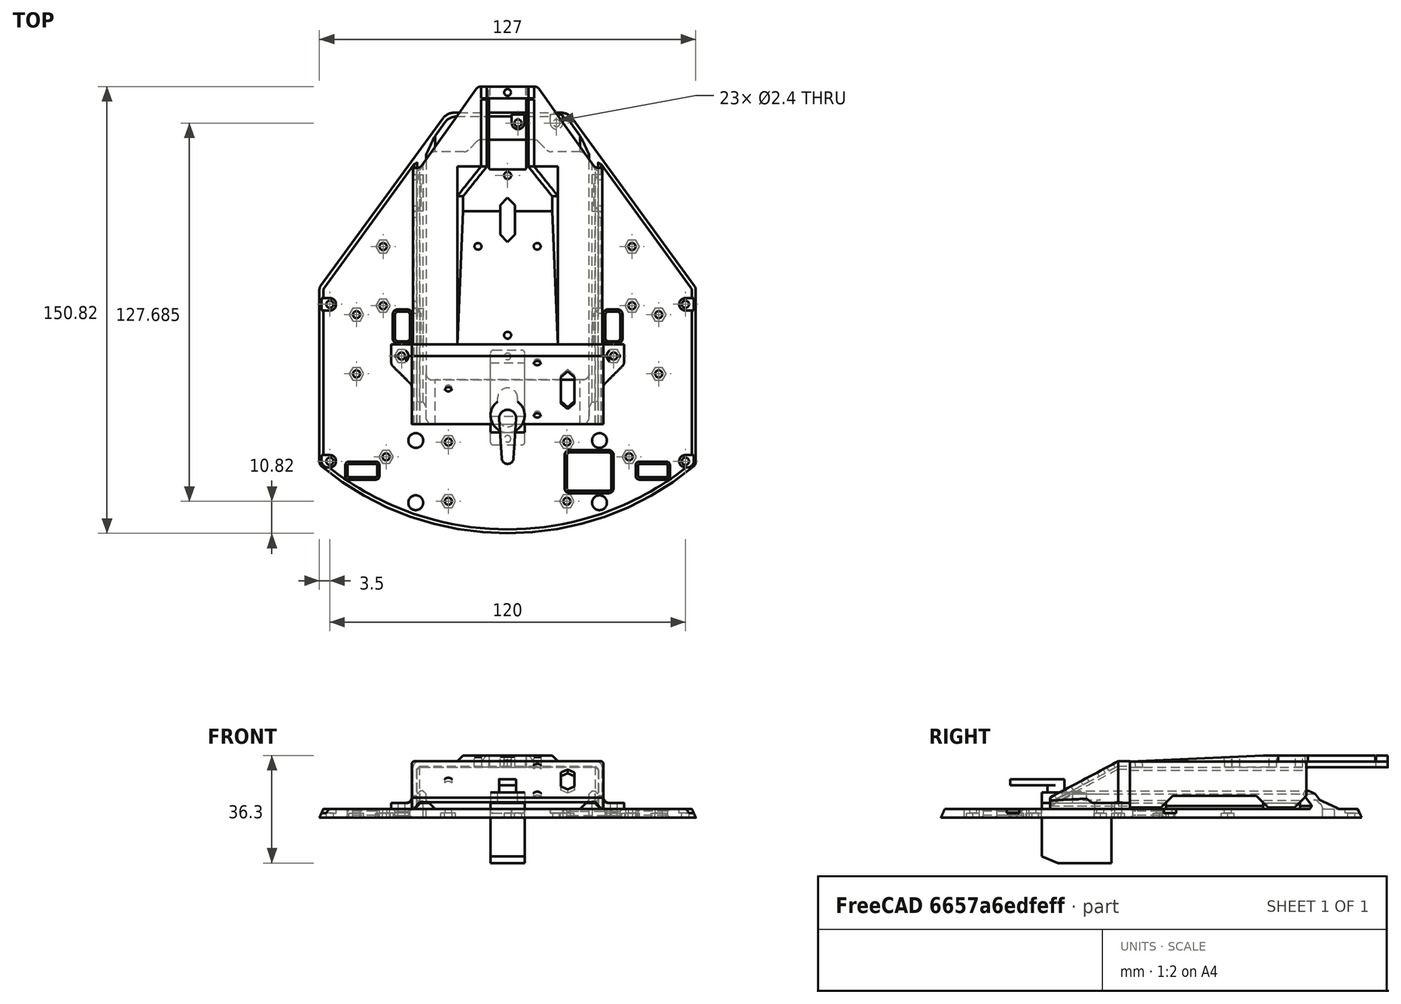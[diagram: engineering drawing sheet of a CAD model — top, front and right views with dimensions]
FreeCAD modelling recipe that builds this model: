
FCSTD DOCUMENT  (FreeCAD 0.19R24276 (Git))
Label: PB3D_TriPlate_Top
License: All rights reserved
LicenseURL: http://en.wikipedia.org/wiki/All_rights_reserved
objects: Sketcher::SketchObject×49, PartDesign::Pocket×31, PartDesign::Plane×10, PartDesign::Pad×9, PartDesign::Body×6, PartDesign::AdditiveLoft×2, PartDesign::SubtractiveLoft×2, App::Part×2, Spreadsheet::Sheet×1, PartDesign::Fillet×1, PartDesign::Chamfer×1, Mesh::Feature×1
note: 157 computed .brp shape members not serialized (recipe doc carries the construction recipe); baked Part::Feature solids carry a one-line shape summary decoded from their .brp

FEATURE [Spreadsheet::Sheet] Spreadsheet  label="params"
  cells = A2=Bottom Plate Main Params; C2=Shell Main Params; E2=Shell Top Bracket Params; G2=Sensor Mounts; A3=Plate Length; B3(plate_length)==170mm; C3=Shell Height; D3(shell_totheight)==42mm; E3=Top Brack Width; F3(shell_topbrack_width)==7mm; G3=Touch Sens Offset; H3(sens_touch_offset_leng)==25mm; I3=Gr Mt 1 W Offset; J3(grmt1_w_offset)==32mm; K3=Gr Mt CableSlot W Offset; L3(grmt_cable_slot_w_offset)==33mm; A4=Plate Width; B4(plate_width)==155mm; C4=Shell Vert Height; D4(shell_vertheight)==10mm; E4=Top Brack Front Split; F4(shell_topbrack_frontsplit)==50mm; G4=Ear Mt Hole Spacing; H4(ear_mt_hole_spacing)==82mm; I4=Gr Mt 1 L Offset; J4(grmt1_l_offset)==31mm; K4=Gr Mt CableSlot L Offset; L4(grmt_cable_slot_l_offset)==19mm; A5=Front Diameter; B5(front_diameter)==225mm; C5=Shell Overhang Length; D5(shell_overhang_leng)==14mm; E5=Top Brack Hole Offset; F5(shell_topbrack_hole_offset)==3.5mm; G5=Ear Mt Hole Loc; H5(ear_mt_holes_loc)==20mm; I5=Gr Mt 2 W Offset; J5(grmt2_w_offset)==41mm; A6=Tail Width; B6(tail_width)==50mm; C6=Shell Wall Thickness; D6(shell_wall_thick)==2mm; E6=Top Brack Fr Leng; F6(top_brack_front_leng)==10mm; G6=Ear Cable Slot Offset From Mt; H6(ear_cable_slot_offset)==2.4mm; I6=Gr Mt 2 L Offset; J6(grmt2_l_offset)==8mm; A7=Plate Thickness; B7(plate_thick)==3mm; C7=Shell Wall Slope; D7(shell_wall_slope)==(shell_totheight - shell_vertheight) / shell_overhang_leng; G7=Ear Cable Slot WidthSpace; H7(ear_cable_slot_offset_width)==8mm; C8=TopPlate Dims; E8=Rails - Shield Cover; G8=Front Cover; I8=Shield Cover; A9=Front Vert. Edge; B9(front_vert_edge)==2mm; C9=Top Thickness; D9(top_thickness)==3mm; E9=Rail Width; F9(rail_width)==3mm; G9=FrCov Leng; H9(coverfront_leng)==27mm; I9=ShCov Leng Side; J9(shieldcov_leng_side)==59.5mm; A10=Back Vert. Edge; B10(back_vert_edge)==15mm; C10=Top Chamfer Width; D10(top_chamfer_width)==top_thickness / shell_wall_slope; E10=Rail Height; F10(rail_height)==6mm; G10=FrCov Height (underneath); H10(coverfront_under_height)==coverfront_angle_leng * tan(rail_front_angle) + rail_front_vert_height + coverfront_tol; I10=SheCov Leng Tot W Tail; J10(shieldcov_leng_tot_wtail)==87mm; A11=Std. Chamfer; B11(std_chamf)==1mm; E11=Rail Front Angle; F11(rail_front_angle)=28; G11=FrCov Wall Thick; H11(coverfront_wall_thick)==1.6mm; I11=ShCov Height; J11(shieldcov_height)==12mm; A12=Std. Radius; B12(std_rad)==2mm; C12=Arduino CutOut; E12=Rail Front Offset Leng; F12(rail_front_offset_leng)==9mm; G12=FrCov Angle Leng; H12(coverfront_angle_leng)==23mm; I12=ShCov Width Inner; J12(shieldcov_width_inner)==ardcut_width + 2 * (rail_width + shieldcov_tol); A13=Wheel Well Radius; B13(wheel_well_rad)==7mm; C13=ArdCut Width; D13(ardcut_width)==55mm; E13=Rail Front Vert Height; F13(rail_front_vert_height)==2mm; G13=FrCov Std Rad; H13(coverfront_std_rad)==coverfront_wall_thick / 2; I13=ShCov Thick Top; J13(shieldcov_thick_top)==2mm; A14=Tail Radius; B14(tail_rad)==5mm; C14=ArdCut Length; D14(ardcut_length)==77mm; E14=Rail Clip Mt Width; F14(rail_clip_mt_width)==2mm; G14=FrCov Tol; H14(coverfront_tol)==0.2mm; I14=ShCov Thick Side; J14(shieldcov_thick_side)==1.2mm; C15=ArdCut Offset LEng; D15(ardcut_offset_leng)==6mm; E15=Rail Clip Mt Loc Front Y; F15(rail_clip_mt_loc_front)==rail_clip_mt_offset + shieldcov_clip_leng / 2; G15=FrCov Foot Width; H15(coverfront_foot_width)==7mm; I15=ShCov Tol; J15(shieldcov_tol)==0.2mm; A16=Wheel Well Plate Width; B16(wheel_well_plate_width)==115mm; C16=ArdCut Rear Angle Leng; D16(ardcut_rear_angle_leng)==3mm; E16=Rail Clip Mt Tol; F16(rail_clip_mt_tol)==0.3mm; G16=FrCov Foot Height; H16(coverfront_foot_height)==2mm; I16=ShCov Clip Hook Width; J16(shieldcov_clip_hook_width)==1.6mm; A17=Wheel Well Clearance; B17(wheel_well_clearance)==48mm; C17=ArdCut Cable Slot Width; D17(ardcut_cableslot_width)==18mm; E17=Rail Clip Mt Loc Back; F17(rail_clip_mt_loc_back)==rail_clip_mt_offset + shieldcov_leng_side - (shieldcov_clip_cut_height - shieldcov_clip_hook_width) - shieldcov_clip_leng / 2; G17=FrCov Foot Leng; H17(coverfront_foot_leng)==6mm; A18=Wheel Well Vert; B18(wheel_well_vert)==7mm; C18=ArdCut Cable Slot Leng; D18(ardcut_cableslot_leng)==4mm; E18=Rail Clip Mt Offset; F18(rail_clip_mt_offset)==18mm; G18=FrCov Outer Wall Width; H18(coverfront_outer_wall_width)==ardcut_width + 2 * (rail_width + coverfront_tol + coverfront_wall_thick); I18=ShCov PreSen AngLeng; J18(shieldcov_pressens_angle_leng)==45mm; E19=Rail Clip Mt Height; F19(rail_clip_mt_height)==2.75mm; G19=FrCov Outer Foot Width; H19(coverfront_outer_foot_width)==coverfront_outer_wall_width + 2 * coverfront_foot_width; I19=ShCov PresSens Height; J19(shieldcov_pressens_height)==2mm; A20=M2 Bolt Clearances; C20=M2.5 Bolt Clearances; I20=ShCov PresSens Width; J20(shieldcov_pressens_width)==30mm; A21=Hole Clear Diam; B21(m2_hole_clear_diam)==2.4mm; C21=Hole Clear Diam; D21(m25_hole_clear_diam)==2.8mm; G21=FrCov W Hole Offset; H21(coverfront_hole_offset_width)==coverfront_foot_width / 2; I21=ShCov PresSens Angle; J21(shieldcov_pressens_angle)==asin(shieldcov_pressens_height / shieldcov_pressens_angle_leng); A22=Head Clear Diam; B22(m2_head_clear_diam)==4.2mm; C22=Head Clear Diam; D22(m25_head_clear_diam)==5.3mm; G22=FrCov L Hole Offset; H22(coverfront_hole_offset_leng)==coverfront_foot_leng / 2 + 1mm; I22=ShCov PresSens Hole Offset; J22(shieldcov_pressens_hole_offset)==3mm; A23=Head Min Depth; B23(m2_head_min_depth)==1.6mm; C23=Head Min Depth; D23(m25_head_min_depth)==2.3mm; I23=ShCov PresSens Grove Cable Slot Offset; J23(shieldcov_pressens_grovecableslot_offset)==42mm; A24=Nut Clear Flat; B24(m2_nut_clear_flat)==4.3mm; C24=Nut Clear Flat; D24(m25_nut_clear_flat)==5.2mm; G24=FrCov Speaker Mt Offset; H24(frontcover_speaker_mt_offset)==3mm; A25=Nut Min Depth; B25(m2_nut_min_depth)==1.75mm; C25=Nut Min Depth; D25(m25_nut_min_depth)==2mm; I25=ShCov Servo Tail Width; J25(shieldcov_servotail_width)==18mm; G26=PlateToFrCov Offset Y; H26(plate_to_frontcov_offset_y)==9mm; I26=ShCov Servo Mt Slot Offset; J26(shieldcov_servomt_slot_offset)==57mm; A27=Std Small Chamf; +17 more cells
FEATURE [Sketcher::SketchObject] Sketch014  label="Sketch_OuterShell_Template"
  FullyConstrained = true
  MapMode = 5
  Support = -> [XY_Plane001]
  expr: Constraints[23] = <<params>>.std_rad
  expr: Constraints[61] = <<params>>.wheel_well_clearance
  expr: Constraints[30] = <<params>>.back_vert_edge
  expr: Constraints[31] = <<params>>.std_rad
  expr: Constraints[12] = <<params>>.plate_length
  expr: Constraints[29] = <<params>>.front_vert_edge
  expr: Constraints[32] = <<params>>.front_diameter
  expr: Constraints[13] = <<params>>.tail_rad
  expr: Constraints[14] = <<params>>.tail_width
  expr: Constraints[41] = <<params>>.plate_width
  expr: Constraints[59] = <<params>>.std_rad
  sketch-geometry (24):
    g0: ArcOfCircle CenterX=0 CenterY=52.6846 CenterZ=0 NormalX=0 NormalY=0 NormalZ=1 AngleXU=0 Radius=112.5 StartAngle=3.96017 EndAngle=5.4646
    g1: LineSegment StartX=-77.1162 StartY=42.1781 StartZ=0 EndX=-29.0404 EndY=108.13 EndZ=0
    g2: LineSegment StartX=-25 StartY=110.185 StartZ=0 EndX=25 EndY=110.185 EndZ=0
    g3: LineSegment StartX=29.0404 StartY=108.13 StartZ=0 EndX=77.1162 EndY=42.1781 EndZ=0
    g4: LineSegment StartX=0 StartY=0 StartZ=0 EndX=0 EndY=110.185 EndZ=0
    g5: ArcOfCircle CenterX=-25 CenterY=105.185 CenterZ=0 NormalX=0 NormalY=0 NormalZ=1 AngleXU=0 Radius=5 StartAngle=1.5708 EndAngle=2.5117
    g6: ArcOfCircle CenterX=25 CenterY=105.185 CenterZ=0 NormalX=0 NormalY=0 NormalZ=1 AngleXU=0 Radius=5 StartAngle=0.629895 EndAngle=1.5708
    g7: GeomPoint X=0 Y=-59.8154 Z=0
    g8: LineSegment StartX=77.5 StartY=26 StartZ=0 EndX=77.5 EndY=41 EndZ=0
    g9: LineSegment StartX=77.5 StartY=-26 StartZ=0 EndX=77.5 EndY=-28 EndZ=0
    g10: LineSegment StartX=-77.5 StartY=26 StartZ=0 EndX=-77.5 EndY=41 EndZ=0
    g11: ArcOfCircle CenterX=75.5 CenterY=-28 CenterZ=0 NormalX=0 NormalY=0 NormalZ=1 AngleXU=0 Radius=2 StartAngle=5.4646 EndAngle=6.28319
    g12: ArcOfCircle CenterX=-75.5 CenterY=-28 CenterZ=0 NormalX=0 NormalY=0 NormalZ=1 AngleXU=0 Radius=2 StartAngle=3.14159 EndAngle=3.96017
    g13: ArcOfCircle CenterX=75.5 CenterY=41 CenterZ=0 NormalX=0 NormalY=0 NormalZ=1 AngleXU=0 Radius=2 StartAngle=-9e-16 EndAngle=0.629895
    g14: ArcOfCircle CenterX=-75.5 CenterY=41 CenterZ=0 NormalX=0 NormalY=0 NormalZ=1 AngleXU=0 Radius=2 StartAngle=2.5117 EndAngle=3.14159
    g15: GeomPoint X=77.5 Y=0 Z=0
    g16: GeomPoint X=-77.5 Y=0 Z=0
    g17: LineSegment StartX=-77.5 StartY=-28 StartZ=0 EndX=-77.5 EndY=-26 EndZ=0
    g18: LineSegment StartX=-77.5 StartY=26 StartZ=0 EndX=-77.5 EndY=24 EndZ=0
    g19: LineSegment StartX=-77.5 StartY=24 StartZ=0 EndX=-77.5 EndY=-24 EndZ=0
    g20: LineSegment StartX=-77.5 StartY=-26 StartZ=0 EndX=-77.5 EndY=-24 EndZ=0
    g21: LineSegment StartX=77.5 StartY=26 StartZ=0 EndX=77.5 EndY=24 EndZ=0
    g22: LineSegment StartX=77.5 StartY=24 StartZ=0 EndX=77.5 EndY=-24 EndZ=0
    g23: LineSegment StartX=77.5 StartY=-24 StartZ=0 EndX=77.5 EndY=-26 EndZ=0
  constraints (62):
    c: PointOnObject(g0,g-2)
    c: Horizontal(g2)
    c: Coincident(g4,g-1)
    c: PointOnObject(g4,g-2)
    c: Tangent(g1,g5) = 1.5708
    c: Tangent(g2,g5) = 1.5708
    c: Tangent(g2,g6) = 1.5708
    c: Tangent(g3,g6) = 1.5708
    c: Equal(g6,g5)
    c: Symmetric(g2,g2,g4)
    c: PointOnObject(g7,g-2)
    c: PointOnObject(g7,g0)
    c: DistanceY(g7,g2) = 170
    c: Radius(g6) = 5
    c: DistanceX(g2,g2) = 50
    c: Vertical(g8)
    c: Vertical(g9)
    c: Vertical(g10)
    c: Equal(g1,g3)
    c: Tangent(g0,g11) = -1.5708
    c: Tangent(g9,g11) = 1.5708
    c: Tangent(g0,g12) = -1.5708
    c: Equal(g11,g12)
    c: Radius(g11) = 2
    c: Tangent(g8,g13) = -1.5708
    c: Tangent(g3,g13) = 1.5708
    c: Tangent(g1,g14) = 1.5708
    c: Tangent(g10,g14) = 1.5708
    c: Equal(g13,g14)
    c: DistanceY(g9,g9) = 2
    c: DistanceY(g8,g8) = 15
    c: Radius(g13) = 2
    c: Diameter(g0) = 225
    c: PointOnObject(g15,g-1)
    c: PointOnObject(g16,g-1)
    c: Symmetric(g10,g17,g16)
    c: Symmetric(g8,g9,g15)
    c: Coincident(g17,g12)
    c: Vertical(g17)
    c: Equal(g10,g8)
    c: Equal(g9,g17)
    c: DistanceX(g12,g9) = 155
    c: Coincident(g18,g10)
    c: Vertical(g18)
    c: Coincident(g19,g18)
    c: Vertical(g19)
    c: Coincident(g20,g17)
    c: Vertical(g20)
    c: Equal(g20,g18)
    c: Coincident(g19,g20)
    c: Tangent(g12,g17)
    c: Coincident(g21,g8)
    c: Vertical(g21)
    c: Coincident(g22,g21)
    c: Vertical(g22)
    c: Coincident(g23,g22)
    c: Coincident(g23,g9)
    c: Equal(g23,g21)
    c: Vertical(g23)
    c: DistanceY(g21,g8) = 2
    c: Equal(g18,g21)
    c: DistanceY(g22,g21) = 48
FEATURE [Sketcher::SketchObject] Sketch015  label="Sketch_TopPlate_Bot"
  FullyConstrained = true
  MapMode = 5
  Support = -> [XY_Plane001]
  expr: Constraints[59] = <<params>>.std_rad
  expr: Constraints[14] = <<params>>.tail_width
  expr: Constraints[41] = <<params>>.plate_width
  expr: Constraints[13] = <<params>>.tail_rad
  expr: Constraints[29] = <<params>>.front_vert_edge
  expr: Constraints[95] = <<params>>.shell_overhang_leng
  expr: Constraints[89] = <<params>>.shell_overhang_leng
  expr: Constraints[32] = <<params>>.front_diameter
  expr: Constraints[88] = <<params>>.shell_overhang_leng
  expr: Constraints[12] = <<params>>.plate_length
  expr: Constraints[30] = <<params>>.back_vert_edge
  expr: Constraints[31] = <<params>>.std_rad
  expr: Constraints[80] = <<params>>.shell_overhang_leng
  expr: Constraints[23] = <<params>>.std_rad
  expr: Constraints[61] = <<params>>.wheel_well_clearance
  expr: Constraints[90] = <<params>>.shell_overhang_leng
  sketch-geometry (39):
    g0: ArcOfCircle CenterX=0 CenterY=52.6846 CenterZ=0 NormalX=0 NormalY=0 NormalZ=1 AngleXU=0 Radius=112.5 StartAngle=3.96017 EndAngle=5.4646
    g1: LineSegment StartX=-77.1162 StartY=42.1781 StartZ=0 EndX=-29.0404 EndY=108.13 EndZ=0
    g2: LineSegment StartX=-25 StartY=110.185 StartZ=0 EndX=25 EndY=110.185 EndZ=0
    g3: LineSegment StartX=29.0404 StartY=108.13 StartZ=0 EndX=77.1162 EndY=42.1781 EndZ=0
    g4: LineSegment StartX=0 StartY=0 StartZ=0 EndX=0 EndY=110.185 EndZ=0
    g5: ArcOfCircle CenterX=-25 CenterY=105.185 CenterZ=0 NormalX=0 NormalY=0 NormalZ=1 AngleXU=0 Radius=5 StartAngle=1.5708 EndAngle=2.5117
    g6: ArcOfCircle CenterX=25 CenterY=105.185 CenterZ=0 NormalX=0 NormalY=0 NormalZ=1 AngleXU=0 Radius=5 StartAngle=0.629894 EndAngle=1.5708
    g7: GeomPoint X=0 Y=-59.8154 Z=0
    g8: LineSegment StartX=77.5 StartY=26 StartZ=0 EndX=77.5 EndY=41 EndZ=0
    g9: LineSegment StartX=77.5 StartY=-26 StartZ=0 EndX=77.5 EndY=-28 EndZ=0
    g10: LineSegment StartX=-77.5 StartY=26 StartZ=0 EndX=-77.5 EndY=41 EndZ=0
    g11: ArcOfCircle CenterX=75.5 CenterY=-28 CenterZ=0 NormalX=0 NormalY=0 NormalZ=1 AngleXU=0 Radius=2 StartAngle=5.4646 EndAngle=6.28319
    g12: ArcOfCircle CenterX=-75.5 CenterY=-28 CenterZ=0 NormalX=0 NormalY=0 NormalZ=1 AngleXU=0 Radius=2 StartAngle=3.14159 EndAngle=3.96017
    g13: ArcOfCircle CenterX=75.5 CenterY=41 CenterZ=0 NormalX=0 NormalY=0 NormalZ=1 AngleXU=0 Radius=2 StartAngle=-9e-16 EndAngle=0.629894
    g14: ArcOfCircle CenterX=-75.5 CenterY=41 CenterZ=0 NormalX=0 NormalY=0 NormalZ=1 AngleXU=0 Radius=2 StartAngle=2.5117 EndAngle=3.14159
    g15: GeomPoint X=77.5 Y=0 Z=0
    g16: GeomPoint X=-77.5 Y=0 Z=0
    g17: LineSegment StartX=-77.5 StartY=-28 StartZ=0 EndX=-77.5 EndY=-26 EndZ=0
    g18: LineSegment StartX=-77.5 StartY=26 StartZ=0 EndX=-77.5 EndY=24 EndZ=0
    g19: LineSegment StartX=-77.5 StartY=24 StartZ=0 EndX=-77.5 EndY=-24 EndZ=0
    g20: LineSegment StartX=-77.5 StartY=-26 StartZ=0 EndX=-77.5 EndY=-24 EndZ=0
    g21: LineSegment StartX=77.5 StartY=26 StartZ=0 EndX=77.5 EndY=24 EndZ=0
    g22: LineSegment StartX=77.5 StartY=24 StartZ=0 EndX=77.5 EndY=-24 EndZ=0
    g23: LineSegment StartX=77.5 StartY=-24 StartZ=0 EndX=77.5 EndY=-26 EndZ=0
    g24: LineSegment StartX=-17.8805 StartY=96.1846 StartZ=0 EndX=17.8805 EndY=96.1846 EndZ=0
    g25: GeomPoint X=0 Y=96.1846 Z=0
    g26: LineSegment StartX=21.921 StartY=94.1299 StartZ=0 EndX=63.1162 EndY=37.617 EndZ=0
    g27: LineSegment StartX=63.5 StartY=36.4389 StartZ=0 EndX=63.5 EndY=-21.6794 EndZ=0
    g28: LineSegment StartX=-21.921 StartY=94.1299 StartZ=0 EndX=-63.1162 EndY=37.617 EndZ=0
    g29: LineSegment StartX=-63.5 StartY=36.4389 StartZ=0 EndX=-63.5 EndY=-21.6794 EndZ=0
    g30: ArcOfCircle CenterX=-17.8805 CenterY=91.1846 CenterZ=0 NormalX=0 NormalY=0 NormalZ=1 AngleXU=0 Radius=5 StartAngle=1.5708 EndAngle=2.5117
    g31: ArcOfCircle CenterX=17.8805 CenterY=91.1846 CenterZ=0 NormalX=0 NormalY=0 NormalZ=1 AngleXU=0 Radius=5 StartAngle=0.629894 EndAngle=1.5708
    g32: ArcOfCircle CenterX=61.5 CenterY=36.4389 CenterZ=0 NormalX=0 NormalY=0 NormalZ=1 AngleXU=0 Radius=2 StartAngle=0 EndAngle=0.629894
    g33: ArcOfCircle CenterX=-61.5 CenterY=36.4389 CenterZ=0 NormalX=0 NormalY=0 NormalZ=1 AngleXU=0 Radius=2 StartAngle=2.5117 EndAngle=3.14159
    g34: ArcOfCircle CenterX=0 CenterY=52.6846 CenterZ=0 NormalX=0 NormalY=0 NormalZ=1 AngleXU=0 Radius=98.5 StartAngle=4.02139 EndAngle=5.40339
    g35: GeomPoint X=0 Y=-45.8154 Z=0
    g36: ArcOfCircle CenterX=-61.5 CenterY=-21.6794 CenterZ=0 NormalX=0 NormalY=0 NormalZ=1 AngleXU=0 Radius=2 StartAngle=3.14159 EndAngle=4.02139
    g37: ArcOfCircle CenterX=61.5 CenterY=-21.6794 CenterZ=0 NormalX=0 NormalY=0 NormalZ=1 AngleXU=0 Radius=2 StartAngle=5.40339 EndAngle=6.28319
    g38: LineSegment StartX=-21.921 StartY=94.1299 StartZ=0 EndX=-33.2342 EndY=102.377 EndZ=0
  constraints (98):
    c: PointOnObject(g0,g-2)
    c: Horizontal(g2)
    c: Coincident(g4,g-1)
    c: PointOnObject(g4,g-2)
    c: Tangent(g1,g5) = 1.5708
    c: Tangent(g2,g5) = 1.5708
    c: Tangent(g2,g6) = 1.5708
    c: Tangent(g3,g6) = 1.5708
    c: Equal(g6,g5)
    c: Symmetric(g2,g2,g4)
    c: PointOnObject(g7,g-2)
    c: PointOnObject(g7,g0)
    c: DistanceY(g7,g2) = 170
    c: Radius(g6) = 5
    c: DistanceX(g2,g2) = 50
    c: Vertical(g8)
    c: Vertical(g9)
    c: Vertical(g10)
    c: Equal(g1,g3)
    c: Tangent(g0,g11) = -1.5708
    c: Tangent(g9,g11) = 1.5708
    c: Tangent(g0,g12) = -1.5708
    c: Equal(g11,g12)
    c: Radius(g11) = 2
    c: Tangent(g8,g13) = -1.5708
    c: Tangent(g3,g13) = 1.5708
    c: Tangent(g1,g14) = 1.5708
    c: Tangent(g10,g14) = 1.5708
    c: Equal(g13,g14)
    c: DistanceY(g9,g9) = 2
    c: DistanceY(g8,g8) = 15
    c: Radius(g13) = 2
    c: Diameter(g0) = 225
    c: PointOnObject(g15,g-1)
    c: PointOnObject(g16,g-1)
    c: Symmetric(g10,g17,g16)
    c: Symmetric(g8,g9,g15)
    c: Coincident(g17,g12)
    c: Vertical(g17)
    c: Equal(g10,g8)
    c: Equal(g9,g17)
    c: DistanceX(g12,g9) = 155
    c: Coincident(g18,g10)
    c: Vertical(g18)
    c: Coincident(g19,g18)
    c: Vertical(g19)
    c: Coincident(g20,g17)
    c: Vertical(g20)
    c: Equal(g20,g18)
    c: Coincident(g19,g20)
    c: Tangent(g12,g17)
    c: Coincident(g21,g8)
    c: Vertical(g21)
    c: Coincident(g22,g21)
    c: Vertical(g22)
    c: Coincident(g23,g22)
    c: Coincident(g23,g9)
    c: Equal(g23,g21)
    c: Vertical(g23)
    c: DistanceY(g21,g8) = 2
    c: Equal(g18,g21)
    c: DistanceY(g22,g21) = 48
    c: Horizontal(g24)
    c: PointOnObject(g25,g-2)
    c: Vertical(g27)
    c: Vertical(g29)
    c: Tangent(g28,g30) = -1.5708
    c: Tangent(g24,g30) = 1.5708
    c: Tangent(g24,g31) = 1.5708
    c: Tangent(g26,g31) = 1.5708
    c: Tangent(g27,g32) = 1.5708
    c: Tangent(g26,g32) = 1.5708
    c: Tangent(g29,g33) = -1.5708
    c: Tangent(g28,g33) = -1.5708
    c: PointOnObject(g35,g-2)
    c: PointOnObject(g35,g34)
    c: Tangent(g34,g36) = -1.5708
    c: Tangent(g29,g36) = -1.5708
    c: Tangent(g34,g37) = -1.5708
    c: Tangent(g27,g37) = 1.5708
    c: DistanceY(g7,g35) = 14
    c: Equal(g11,g37)
    c: Equal(g37,g32)
    c: Equal(g36,g37)
    c: Equal(g36,g33)
    c: Equal(g30,g31)
    c: Equal(g31,g6)
    c: Symmetric(g24,g24,g25)
    c: DistanceY(g25,g4) = 14
    c: DistanceX(g27,g15) = 14
    c: DistanceX(g16,g29) = 14
    c: Coincident(g38,g28)
    c: PointOnObject(g38,g1)
    c: Perpendicular(g1,g38)
    c: Perpendicular(g28,g38)
    c: Distance(g38) = 14
    c: Parallel(g26,g3)
    c: Coincident(g34,g0)
FEATURE [PartDesign::Plane] DatumPlane  label="Datum_TopOfPlate"
  AttachmentOffset = pos=(0,0,3) rot=(0,0,1;0rad)
  Length = 153.84
  MapMode = 5
  Placement = pos=(0,0,3) rot=(0,0,1;0rad)
  ResizeMode = 0
  Support = -> [XY_Plane001]
  Width = 168.645
  expr: .AttachmentOffset.Base.z = <<params>>.top_thickness
FEATURE [Sketcher::SketchObject] Sketch016  label="Sketch_TopPlate_Top"
  FullyConstrained = true
  MapMode = 5
  Placement = pos=(0,0,3) rot=(0,0,1;0rad)
  Support = -> [DatumPlane]
  expr: Constraints[90] = <<params>>.shell_overhang_leng + <<params>>.top_chamfer_width
  expr: Constraints[32] = <<params>>.front_diameter
  expr: Constraints[89] = <<params>>.shell_overhang_leng + <<params>>.top_chamfer_width
  expr: Constraints[95] = <<params>>.shell_overhang_leng + <<params>>.top_chamfer_width
  expr: Constraints[29] = <<params>>.front_vert_edge
  expr: Constraints[23] = <<params>>.std_rad
  expr: Constraints[61] = <<params>>.wheel_well_clearance
  expr: Constraints[80] = <<params>>.shell_overhang_leng + <<params>>.top_chamfer_width
  expr: Constraints[30] = <<params>>.back_vert_edge
  expr: Constraints[31] = <<params>>.std_rad
  expr: Constraints[12] = <<params>>.plate_length
  expr: Constraints[88] = <<params>>.shell_overhang_leng + <<params>>.top_chamfer_width
  expr: Constraints[13] = <<params>>.tail_rad
  expr: Constraints[14] = <<params>>.tail_width
  expr: Constraints[41] = <<params>>.plate_width
  expr: Constraints[59] = <<params>>.std_rad
  sketch-geometry (39):
    g0: ArcOfCircle CenterX=0 CenterY=52.6846 CenterZ=0 NormalX=0 NormalY=0 NormalZ=1 AngleXU=0 Radius=112.5 StartAngle=3.96017 EndAngle=5.4646
    g1: LineSegment StartX=-77.1162 StartY=42.1781 StartZ=0 EndX=-29.0404 EndY=108.13 EndZ=0
    g2: LineSegment StartX=-25 StartY=110.185 StartZ=0 EndX=25 EndY=110.185 EndZ=0
    g3: LineSegment StartX=29.0404 StartY=108.13 StartZ=0 EndX=77.1162 EndY=42.1781 EndZ=0
    g4: LineSegment StartX=0 StartY=0 StartZ=0 EndX=0 EndY=110.185 EndZ=0
    g5: ArcOfCircle CenterX=-25 CenterY=105.185 CenterZ=0 NormalX=0 NormalY=0 NormalZ=1 AngleXU=0 Radius=5 StartAngle=1.5708 EndAngle=2.5117
    g6: ArcOfCircle CenterX=25 CenterY=105.185 CenterZ=0 NormalX=0 NormalY=0 NormalZ=1 AngleXU=0 Radius=5 StartAngle=0.629894 EndAngle=1.5708
    g7: GeomPoint X=0 Y=-59.8154 Z=0
    g8: LineSegment StartX=77.5 StartY=26 StartZ=0 EndX=77.5 EndY=41 EndZ=0
    g9: LineSegment StartX=77.5 StartY=-26 StartZ=0 EndX=77.5 EndY=-28 EndZ=0
    g10: LineSegment StartX=-77.5 StartY=26 StartZ=0 EndX=-77.5 EndY=41 EndZ=0
    g11: ArcOfCircle CenterX=75.5 CenterY=-28 CenterZ=0 NormalX=0 NormalY=0 NormalZ=1 AngleXU=0 Radius=2 StartAngle=5.4646 EndAngle=6.28319
    g12: ArcOfCircle CenterX=-75.5 CenterY=-28 CenterZ=0 NormalX=0 NormalY=0 NormalZ=1 AngleXU=0 Radius=2 StartAngle=3.14159 EndAngle=3.96017
    g13: ArcOfCircle CenterX=75.5 CenterY=41 CenterZ=0 NormalX=0 NormalY=0 NormalZ=1 AngleXU=0 Radius=2 StartAngle=9e-16 EndAngle=0.629894
    g14: ArcOfCircle CenterX=-75.5 CenterY=41 CenterZ=0 NormalX=0 NormalY=0 NormalZ=1 AngleXU=0 Radius=2 StartAngle=2.5117 EndAngle=3.14159
    g15: GeomPoint X=77.5 Y=0 Z=0
    g16: GeomPoint X=-77.5 Y=0 Z=0
    g17: LineSegment StartX=-77.5 StartY=-28 StartZ=0 EndX=-77.5 EndY=-26 EndZ=0
    g18: LineSegment StartX=-77.5 StartY=26 StartZ=0 EndX=-77.5 EndY=24 EndZ=0
    g19: LineSegment StartX=-77.5 StartY=24 StartZ=0 EndX=-77.5 EndY=-24 EndZ=0
    g20: LineSegment StartX=-77.5 StartY=-26 StartZ=0 EndX=-77.5 EndY=-24 EndZ=0
    g21: LineSegment StartX=77.5 StartY=26 StartZ=0 EndX=77.5 EndY=24 EndZ=0
    g22: LineSegment StartX=77.5 StartY=24 StartZ=0 EndX=77.5 EndY=-24 EndZ=0
    g23: LineSegment StartX=77.5 StartY=-24 StartZ=0 EndX=77.5 EndY=-26 EndZ=0
    g24: LineSegment StartX=-17.2131 StartY=94.8721 StartZ=0 EndX=17.2131 EndY=94.8721 EndZ=0
    g25: GeomPoint X=0 Y=94.8721 Z=0
    g26: LineSegment StartX=21.2535 StartY=92.8174 StartZ=0 EndX=61.8037 EndY=37.1894 EndZ=0
    g27: LineSegment StartX=62.1875 StartY=36.0113 StartZ=0 EndX=62.1875 EndY=-21.0591 EndZ=0
    g28: LineSegment StartX=-21.2535 StartY=92.8174 StartZ=0 EndX=-61.8037 EndY=37.1894 EndZ=0
    g29: LineSegment StartX=-62.1875 StartY=36.0113 StartZ=0 EndX=-62.1875 EndY=-21.0591 EndZ=0
    g30: ArcOfCircle CenterX=-17.2131 CenterY=89.8721 CenterZ=0 NormalX=0 NormalY=0 NormalZ=1 AngleXU=0 Radius=5 StartAngle=1.5708 EndAngle=2.5117
    g31: ArcOfCircle CenterX=17.2131 CenterY=89.8721 CenterZ=0 NormalX=0 NormalY=0 NormalZ=1 AngleXU=0 Radius=5 StartAngle=0.629894 EndAngle=1.5708
    g32: ArcOfCircle CenterX=60.1875 CenterY=36.0113 CenterZ=0 NormalX=0 NormalY=0 NormalZ=1 AngleXU=0 Radius=2 StartAngle=-1.8e-15 EndAngle=0.629894
    g33: ArcOfCircle CenterX=-60.1875 CenterY=36.0113 CenterZ=0 NormalX=0 NormalY=0 NormalZ=1 AngleXU=0 Radius=2 StartAngle=2.5117 EndAngle=3.14159
    g34: ArcOfCircle CenterX=0 CenterY=52.6846 CenterZ=0 NormalX=0 NormalY=0 NormalZ=1 AngleXU=0 Radius=97.1875 StartAngle=4.02786 EndAngle=5.39691
    g35: GeomPoint X=0 Y=-44.5029 Z=0
    g36: ArcOfCircle CenterX=-60.1875 CenterY=-21.0591 CenterZ=0 NormalX=0 NormalY=0 NormalZ=1 AngleXU=0 Radius=2 StartAngle=3.14159 EndAngle=4.02786
    g37: ArcOfCircle CenterX=60.1875 CenterY=-21.0591 CenterZ=0 NormalX=0 NormalY=0 NormalZ=1 AngleXU=0 Radius=2 StartAngle=5.39691 EndAngle=6.28319
    g38: LineSegment StartX=-21.2535 StartY=92.8174 StartZ=0 EndX=-33.6274 EndY=101.837 EndZ=0
  constraints (98):
    c: PointOnObject(g0,g-2)
    c: Horizontal(g2)
    c: Coincident(g4,g-1)
    c: PointOnObject(g4,g-2)
    c: Tangent(g1,g5) = 1.5708
    c: Tangent(g2,g5) = 1.5708
    c: Tangent(g2,g6) = 1.5708
    c: Tangent(g3,g6) = 1.5708
    c: Equal(g6,g5)
    c: Symmetric(g2,g2,g4)
    c: PointOnObject(g7,g-2)
    c: PointOnObject(g7,g0)
    c: DistanceY(g7,g2) = 170
    c: Radius(g6) = 5
    c: DistanceX(g2,g2) = 50
    c: Vertical(g8)
    c: Vertical(g9)
    c: Vertical(g10)
    c: Equal(g1,g3)
    c: Tangent(g0,g11) = -1.5708
    c: Tangent(g9,g11) = 1.5708
    c: Tangent(g0,g12) = -1.5708
    c: Equal(g11,g12)
    c: Radius(g11) = 2
    c: Tangent(g8,g13) = -1.5708
    c: Tangent(g3,g13) = 1.5708
    c: Tangent(g1,g14) = 1.5708
    c: Tangent(g10,g14) = 1.5708
    c: Equal(g13,g14)
    c: DistanceY(g9,g9) = 2
    c: DistanceY(g8,g8) = 15
    c: Radius(g13) = 2
    c: Diameter(g0) = 225
    c: PointOnObject(g15,g-1)
    c: PointOnObject(g16,g-1)
    c: Symmetric(g10,g17,g16)
    c: Symmetric(g8,g9,g15)
    c: Coincident(g17,g12)
    c: Vertical(g17)
    c: Equal(g10,g8)
    c: Equal(g9,g17)
    c: DistanceX(g12,g9) = 155
    c: Coincident(g18,g10)
    c: Vertical(g18)
    c: Coincident(g19,g18)
    c: Vertical(g19)
    c: Coincident(g20,g17)
    c: Vertical(g20)
    c: Equal(g20,g18)
    c: Coincident(g19,g20)
    c: Tangent(g12,g17)
    c: Coincident(g21,g8)
    c: Vertical(g21)
    c: Coincident(g22,g21)
    c: Vertical(g22)
    c: Coincident(g23,g22)
    c: Coincident(g23,g9)
    c: Equal(g23,g21)
    c: Vertical(g23)
    c: DistanceY(g21,g8) = 2
    c: Equal(g18,g21)
    c: DistanceY(g22,g21) = 48
    c: Horizontal(g24)
    c: PointOnObject(g25,g-2)
    c: Vertical(g27)
    c: Vertical(g29)
    c: Tangent(g28,g30) = -1.5708
    c: Tangent(g24,g30) = 1.5708
    c: Tangent(g24,g31) = 1.5708
    c: Tangent(g26,g31) = 1.5708
    c: Tangent(g27,g32) = 1.5708
    c: Tangent(g26,g32) = 1.5708
    c: Tangent(g29,g33) = -1.5708
    c: Tangent(g28,g33) = -1.5708
    c: PointOnObject(g35,g-2)
    c: PointOnObject(g35,g34)
    c: Tangent(g34,g36) = -1.5708
    c: Tangent(g29,g36) = -1.5708
    c: Tangent(g34,g37) = -1.5708
    c: Tangent(g27,g37) = 1.5708
    c: DistanceY(g7,g35) = 15.3125
    c: Equal(g11,g37)
    c: Equal(g37,g32)
    c: Equal(g36,g37)
    c: Equal(g36,g33)
    c: Equal(g30,g31)
    c: Equal(g31,g6)
    c: Symmetric(g24,g24,g25)
    c: DistanceY(g25,g4) = 15.3125
    c: DistanceX(g27,g15) = 15.3125
    c: DistanceX(g16,g29) = 15.3125
    c: Coincident(g38,g28)
    c: PointOnObject(g38,g1)
    c: Perpendicular(g1,g38)
    c: Perpendicular(g28,g38)
    c: Distance(g38) = 15.3125
    c: Parallel(g26,g3)
    c: Coincident(g34,g0)
FEATURE [PartDesign::AdditiveLoft] AdditiveLoft  label="MainTopPlate_ChamfExt"
  Closed = false
  Profile = -> Sketch015
  Ruled = false
  Sections = -> [Sketch016]
FEATURE [Sketcher::SketchObject] Sketch021  label="Sketch_ShellTopMountHoles"
  FullyConstrained = true
  MapMode = 5
  Support = -> [XY_Plane001]
  expr: Constraints[91] = <<params>>.top_brack_front_leng - <<params>>.shell_topbrack_hole_offset
  expr: Constraints[86] = <<params>>.shell_topbrack_width * 2 - <<params>>.std_rad - <<params>>.shell_topbrack_hole_offset
  expr: Constraints[84] = <<params>>.m2_hole_clear_diam
  expr: Constraints[82] = <<params>>.shell_overhang_leng + <<params>>.shell_topbrack_width - <<params>>.shell_topbrack_hole_offset
  expr: Constraints[59] = <<params>>.std_rad
  expr: Constraints[14] = <<params>>.tail_width
  expr: Constraints[41] = <<params>>.plate_width
  expr: Constraints[13] = <<params>>.tail_rad
  expr: Constraints[83] = <<params>>.shell_overhang_leng + <<params>>.shell_topbrack_width - <<params>>.shell_topbrack_hole_offset
  expr: Constraints[85] = <<params>>.shell_topbrack_hole_offset + <<params>>.std_rad
  expr: Constraints[32] = <<params>>.front_diameter
  expr: Constraints[29] = <<params>>.front_vert_edge
  expr: Constraints[12] = <<params>>.plate_length
  expr: Constraints[30] = <<params>>.back_vert_edge
  expr: Constraints[31] = <<params>>.std_rad
  expr: Constraints[61] = <<params>>.wheel_well_clearance
  expr: Constraints[23] = <<params>>.std_rad
  expr: Constraints[90] = <<params>>.shell_topbrack_hole_offset
  sketch-geometry (37):
    g0: ArcOfCircle CenterX=0 CenterY=52.6846 CenterZ=0 NormalX=0 NormalY=0 NormalZ=1 AngleXU=0 Radius=112.5 StartAngle=3.96017 EndAngle=5.4646
    g1: LineSegment StartX=-77.1162 StartY=42.1781 StartZ=0 EndX=-29.0404 EndY=108.13 EndZ=0
    g2: LineSegment StartX=-25 StartY=110.185 StartZ=0 EndX=25 EndY=110.185 EndZ=0
    g3: LineSegment StartX=29.0404 StartY=108.13 StartZ=0 EndX=77.1162 EndY=42.1781 EndZ=0
    g4: LineSegment StartX=0 StartY=0 StartZ=0 EndX=0 EndY=110.185 EndZ=0
    g5: ArcOfCircle CenterX=-25 CenterY=105.185 CenterZ=0 NormalX=0 NormalY=0 NormalZ=1 AngleXU=0 Radius=5 StartAngle=1.5708 EndAngle=2.5117
    g6: ArcOfCircle CenterX=25 CenterY=105.185 CenterZ=0 NormalX=0 NormalY=0 NormalZ=1 AngleXU=0 Radius=5 StartAngle=0.629894 EndAngle=1.5708
    g7: GeomPoint X=0 Y=-59.8154 Z=0
    g8: LineSegment StartX=77.5 StartY=26 StartZ=0 EndX=77.5 EndY=41 EndZ=0
    g9: LineSegment StartX=77.5 StartY=-26 StartZ=0 EndX=77.5 EndY=-28 EndZ=0
    g10: LineSegment StartX=-77.5 StartY=26 StartZ=0 EndX=-77.5 EndY=41 EndZ=0
    g11: ArcOfCircle CenterX=75.5 CenterY=-28 CenterZ=0 NormalX=0 NormalY=0 NormalZ=1 AngleXU=0 Radius=2 StartAngle=5.4646 EndAngle=6.28319
    g12: ArcOfCircle CenterX=-75.5 CenterY=-28 CenterZ=0 NormalX=0 NormalY=0 NormalZ=1 AngleXU=0 Radius=2 StartAngle=3.1416 EndAngle=3.96017
    g13: ArcOfCircle CenterX=75.5 CenterY=41 CenterZ=0 NormalX=0 NormalY=0 NormalZ=1 AngleXU=0 Radius=2 StartAngle=1.4e-15 EndAngle=0.629894
    g14: ArcOfCircle CenterX=-75.5 CenterY=41 CenterZ=0 NormalX=0 NormalY=0 NormalZ=1 AngleXU=0 Radius=2 StartAngle=2.5117 EndAngle=3.14159
    g15: GeomPoint X=77.5 Y=0 Z=0
    g16: GeomPoint X=-77.5 Y=0 Z=0
    g17: LineSegment StartX=-77.5 StartY=-28 StartZ=0 EndX=-77.5 EndY=-26 EndZ=0
    g18: LineSegment StartX=-77.5 StartY=26 StartZ=0 EndX=-77.5 EndY=24 EndZ=0
    g19: LineSegment StartX=-77.5 StartY=24 StartZ=0 EndX=-77.5 EndY=-24 EndZ=0
    g20: LineSegment StartX=-77.5 StartY=-26 StartZ=0 EndX=-77.5 EndY=-24 EndZ=0
    g21: LineSegment StartX=77.5 StartY=26 StartZ=0 EndX=77.5 EndY=24 EndZ=0
    g22: LineSegment StartX=77.5 StartY=24 StartZ=0 EndX=77.5 EndY=-24 EndZ=0
    g23: LineSegment StartX=77.5 StartY=-24 StartZ=0 EndX=77.5 EndY=-26 EndZ=0
    g24: Circle CenterX=16.5 CenterY=92.6846 CenterZ=0 NormalX=0 NormalY=0 NormalZ=1 AngleXU=0 Radius=1.2
    g25: Circle CenterX=60 CenterY=31.5 CenterZ=0 NormalX=0 NormalY=0 NormalZ=1 AngleXU=0 Radius=1.2
    g26: Circle CenterX=-60 CenterY=31.5 CenterZ=0 NormalX=0 NormalY=0 NormalZ=1 AngleXU=0 Radius=1.2
    g27: Circle CenterX=-60 CenterY=-21.5 CenterZ=0 NormalX=0 NormalY=0 NormalZ=1 AngleXU=0 Radius=1.2
    g28: Circle CenterX=60 CenterY=-21.5 CenterZ=0 NormalX=0 NormalY=0 NormalZ=1 AngleXU=0 Radius=1.2
    g29: LineSegment StartX=-60 StartY=-21.5 StartZ=0 EndX=60 EndY=-21.5 EndZ=0
    g30: LineSegment StartX=-60 StartY=31.5 StartZ=0 EndX=60 EndY=31.5 EndZ=0
    g31: LineSegment StartX=-16.5 StartY=92.6846 StartZ=0 EndX=16.5 EndY=92.6846 EndZ=0
    g32: GeomPoint X=0 Y=92.6846 Z=0
    g33: GeomPoint X=0 Y=31.5 Z=0
    g34: GeomPoint X=0 Y=-21.5 Z=0
    g35: LineSegment StartX=-60 StartY=31.5 StartZ=0 EndX=-60 EndY=-21.5 EndZ=0
    g36: Circle CenterX=3.5 CenterY=92.6846 CenterZ=0 NormalX=0 NormalY=0 NormalZ=1 AngleXU=0 Radius=1.2
  constraints (92):
    c: PointOnObject(g0,g-2)
    c: Horizontal(g2)
    c: Coincident(g4,g-1)
    c: PointOnObject(g4,g-2)
    c: Tangent(g1,g5) = 1.5708
    c: Tangent(g2,g5) = 1.5708
    c: Tangent(g2,g6) = 1.5708
    c: Tangent(g3,g6) = 1.5708
    c: Equal(g6,g5)
    c: Symmetric(g2,g2,g4)
    c: PointOnObject(g7,g-2)
    c: PointOnObject(g7,g0)
    c: DistanceY(g7,g2) = 170
    c: Radius(g6) = 5
    c: DistanceX(g2,g2) = 50
    c: Vertical(g8)
    c: Vertical(g9)
    c: Vertical(g10)
    c: Equal(g1,g3)
    c: Tangent(g0,g11) = -1.5708
    c: Tangent(g9,g11) = 1.5708
    c: Tangent(g0,g12) = -1.5708
    c: Equal(g11,g12)
    c: Radius(g11) = 2
    c: Tangent(g8,g13) = -1.5708
    c: Tangent(g3,g13) = 1.5708
    c: Tangent(g1,g14) = 1.5708
    c: Tangent(g10,g14) = 1.5708
    c: Equal(g13,g14)
    c: DistanceY(g9,g9) = 2
    c: DistanceY(g8,g8) = 15
    c: Radius(g13) = 2
    c: Diameter(g0) = 225
    c: PointOnObject(g15,g-1)
    c: PointOnObject(g16,g-1)
    c: Symmetric(g10,g17,g16)
    c: Symmetric(g8,g9,g15)
    c: Coincident(g17,g12)
    c: Vertical(g17)
    c: Equal(g10,g8)
    c: Equal(g9,g17)
    c: DistanceX(g12,g9) = 155
    c: Coincident(g18,g10)
    c: Vertical(g18)
    c: Coincident(g19,g18)
    c: Vertical(g19)
    c: Coincident(g20,g17)
    c: Vertical(g20)
    c: Equal(g20,g18)
    c: Coincident(g19,g20)
    c: Tangent(g12,g17)
    c: Coincident(g21,g8)
    c: Vertical(g21)
    c: Coincident(g22,g21)
    c: Vertical(g22)
    c: Coincident(g23,g22)
    c: Coincident(g23,g9)
    c: Equal(g23,g21)
    c: Vertical(g23)
    c: DistanceY(g21,g8) = 2
    c: Equal(g18,g21)
    c: DistanceY(g22,g21) = 48
    c: Coincident(g29,g27)
    c: Coincident(g29,g28)
    c: Horizontal(g29)
    c: Coincident(g30,g26)
    c: Coincident(g30,g25)
    c: Horizontal(g30)
    c: Equal(g27,g28)
    c: Equal(g28,g25)
    c: Equal(g25,g24)
    c: Equal(g25,g26)
    c: Coincident(g31,g24)
    c: Horizontal(g31)
    c: PointOnObject(g32,g4)
    c: PointOnObject(g33,g4)
    c: PointOnObject(g34,g-2)
    c: Symmetric(g26,g25,g33)
    c: Symmetric(g27,g28,g34)
    c: Coincident(g35,g26)
    c: Coincident(g35,g27)
    c: Vertical(g35)
    c: DistanceX(g25,g8) = 17.5
    c: DistanceY(g24,g2) = 17.5
    c: Diameter(g28) = 2.4
    c: DistanceY(g8,g25) = 5.5
    c: DistanceX(g24,g2) = 8.5
    c: Symmetric(g31,g24,g32)
    c: PointOnObject(g36,g31)
    c: Equal(g24,g36)
    c: DistanceX(g32,g36) = 3.5
    c: DistanceY(g9,g28) = 6.5
FEATURE [Sketcher::SketchObject] Sketch  label="Sketch_ArduinoCutOut"
  FullyConstrained = true
  MapMode = 5
  Support = -> [XY_Plane001]
  expr: Constraints[55] = <<params>>.ardcut_cableslot_leng
  expr: Constraints[56] = <<params>>.ardcut_cableslot_width
  expr: Constraints[11] = <<params>>.std_rad
  expr: Constraints[30] = <<params>>.ardcut_rear_angle_leng
  expr: Constraints[31] = <<params>>.ardcut_length
  expr: Constraints[32] = <<params>>.ardcut_width
  expr: Constraints[33] = <<params>>.ardcut_offset_leng
  sketch-geometry (25):
    g0: LineSegment StartX=-26.9142 StartY=81.4142 StartZ=0 EndX=-25.9142 EndY=82.4142 EndZ=0
    g1: LineSegment StartX=-24.5 StartY=83 StartZ=0 EndX=24.5 EndY=83 EndZ=0
    g2: LineSegment StartX=25.9142 StartY=82.4142 StartZ=0 EndX=26.9142 EndY=81.4142 EndZ=0
    g3: LineSegment StartX=-27.5 StartY=80 StartZ=0 EndX=-27.5 EndY=8 EndZ=0
    g4: LineSegment StartX=-25.5 StartY=6 StartZ=0 EndX=25.5 EndY=6 EndZ=0
    g5: LineSegment StartX=27.5 StartY=8 StartZ=0 EndX=27.5 EndY=80 EndZ=0
    g6: LineSegment StartX=-27.5 StartY=80 StartZ=0 EndX=27.5 EndY=80 EndZ=0
    g7: GeomPoint X=0 Y=83 Z=0
    g8: GeomPoint X=0 Y=6 Z=0
    g9: ArcOfCircle CenterX=-25.5 CenterY=8 CenterZ=0 NormalX=0 NormalY=0 NormalZ=1 AngleXU=0 Radius=2 StartAngle=3.14159 EndAngle=4.71239
    g10: ArcOfCircle CenterX=25.5 CenterY=8 CenterZ=0 NormalX=0 NormalY=0 NormalZ=1 AngleXU=0 Radius=2 StartAngle=4.71239 EndAngle=6.28319
    g11: ArcOfCircle CenterX=-25.5 CenterY=80 CenterZ=0 NormalX=0 NormalY=0 NormalZ=1 AngleXU=0 Radius=2 StartAngle=2.35619 EndAngle=3.14159
    g12: ArcOfCircle CenterX=25.5 CenterY=80 CenterZ=0 NormalX=0 NormalY=0 NormalZ=1 AngleXU=0 Radius=2 StartAngle=1.2e-15 EndAngle=0.785398
    g13: ArcOfCircle CenterX=-24.5 CenterY=81 CenterZ=0 NormalX=0 NormalY=0 NormalZ=1 AngleXU=0 Radius=2 StartAngle=1.5708 EndAngle=2.35619
    g14: ArcOfCircle CenterX=24.5 CenterY=81 CenterZ=0 NormalX=0 NormalY=0 NormalZ=1 AngleXU=0 Radius=2 StartAngle=0.785398 EndAngle=1.5708
    g15: LineSegment StartX=-9 StartY=87 StartZ=0 EndX=9 EndY=87 EndZ=0
    g16: GeomPoint X=0 Y=87 Z=0
    g17: LineSegment StartX=-10.4142 StartY=86.4142 StartZ=0 EndX=-13.2426 EndY=83.5858 EndZ=0
    g18: LineSegment StartX=10.4142 StartY=86.4142 StartZ=0 EndX=13.2426 EndY=83.5858 EndZ=0
    g19: LineSegment StartX=-14.6569 StartY=83 StartZ=0 EndX=-24.5 EndY=83 EndZ=0
    g20: ArcOfCircle CenterX=-14.6569 CenterY=85 CenterZ=0 NormalX=0 NormalY=0 NormalZ=1 AngleXU=0 Radius=2 StartAngle=4.71239 EndAngle=5.49779
    g21: ArcOfCircle CenterX=-9 CenterY=85 CenterZ=0 NormalX=0 NormalY=0 NormalZ=1 AngleXU=0 Radius=2 StartAngle=1.5708 EndAngle=2.35619
    g22: ArcOfCircle CenterX=9 CenterY=85 CenterZ=0 NormalX=0 NormalY=0 NormalZ=1 AngleXU=0 Radius=2 StartAngle=0.785398 EndAngle=1.5708
    g23: LineSegment StartX=24.5 StartY=83 StartZ=0 EndX=14.6569 EndY=83 EndZ=0
    g24: ArcOfCircle CenterX=14.6569 CenterY=85 CenterZ=0 NormalX=0 NormalY=0 NormalZ=1 AngleXU=0 Radius=2 StartAngle=3.92699 EndAngle=4.71239
  constraints (57):
    c: Horizontal(g1)
    c: Vertical(g3)
    c: Horizontal(g4)
    c: Vertical(g5)
    c: Horizontal(g6)
    c: PointOnObject(g7,g-2)
    c: PointOnObject(g8,g-2)
    c: Tangent(g3,g9) = -1.5708
    c: Tangent(g4,g9) = -1.5708
    c: Tangent(g4,g10) = -1.5708
    c: Tangent(g5,g10) = -1.5708
    c: Radius(g10) = 2
    c: Tangent(g3,g11) = -1.5708
    c: Tangent(g0,g11) = 1.5708
    c: Tangent(g2,g12) = 1.5708
    c: Tangent(g5,g12) = -1.5708
    c: Tangent(g1,g13) = 1.5708
    c: Tangent(g0,g13) = 1.5708
    c: Tangent(g1,g14) = 1.5708
    c: Tangent(g2,g14) = 1.5708
    c: Equal(g10,g9)
    c: Equal(g10,g12)
    c: Equal(g12,g14)
    c: Equal(g14,g13)
    c: Equal(g13,g11)
    c: Coincident(g6,g5)
    c: Coincident(g6,g3)
    c: Angle(g2,g6) = 0.785398
    c: Symmetric(g1,g1,g7)
    c: Symmetric(g4,g4,g8)
    c: DistanceY(g5,g1) = 3
    c: DistanceY(g4,g1) = 77
    c: DistanceX(g3,g5) = 55
    c: DistanceY(g-1,g8) = 6
    c: Horizontal(g15)
    c: PointOnObject(g16,g-2)
    c: Coincident(g19,g13)
    c: Tangent(g17,g20) = 1.5708
    c: Tangent(g19,g20) = 1.5708
    c: Tangent(g17,g21) = -1.5708
    c: Tangent(g15,g21) = 1.5708
    c: Tangent(g15,g22) = 1.5708
    c: Tangent(g18,g22) = 1.5708
    c: Coincident(g23,g14)
    c: Tangent(g23,g24) = 1.5708
    c: Tangent(g18,g24) = -1.5708
    c: Angle(g18,g1) = 0.785398
    c: Angle(g1,g17) = 0.785398
    c: PointOnObject(g19,g1)
    c: PointOnObject(g23,g1)
    c: Equal(g14,g24)
    c: Equal(g14,g22)
    c: Equal(g14,g21)
    c: Equal(g14,g20)
    c: Symmetric(g15,g15,g16)
    c: DistanceY(g23,g15) = 4
    c: DistanceX(g15,g15) = 18
FEATURE [Sketcher::SketchObject] Sketch022  label="Sketch_ShieldCoverRails"
  FullyConstrained = true
  MapMode = 5
  Placement = pos=(0,0,0) rot=(0.57735,0.57735,0.57735;2.0944rad)
  Support = -> [YZ_Plane001]
  expr: Constraints[6] = <<params>>.rail_height
  expr: Constraints[5] = <<params>>.plate_thick
  expr: Constraints[8] = <<params>>.rail_front_offset_leng
  expr: Constraints[13] = <<params>>.rail_front_vert_height
  expr: Constraints[17] = <<params>>.rail_front_angle
  sketch-geometry (6):
    g0: LineSegment StartX=-1.47709 StartY=9 StartZ=0 EndX=98.5229 EndY=9 EndZ=0
    g1: LineSegment StartX=-9 StartY=3 StartZ=0 EndX=98.5229 EndY=3 EndZ=0
    g2: LineSegment StartX=98.5229 StartY=9 StartZ=0 EndX=98.5229 EndY=3 EndZ=0
    g3: LineSegment StartX=-9 StartY=3 StartZ=0 EndX=-9 EndY=5 EndZ=0
    g4: LineSegment StartX=-9 StartY=5 StartZ=0 EndX=-1.47709 EndY=9 EndZ=0
    g5: LineSegment StartX=-9 StartY=5 StartZ=0 EndX=98.5229 EndY=5 EndZ=0
  constraints (18):
    c: Horizontal(g0)
    c: Horizontal(g1)
    c: Coincident(g2,g0)
    c: Coincident(g2,g1)
    c: Vertical(g2)
    c: DistanceY(g-1,g1) = 3
    c: DistanceY(g1,g0) = 6
    c: DistanceX(g0,g0) = 100
    c: DistanceX(g1,g-1) = 9
    c: Coincident(g3,g1)
    c: Vertical(g3)
    c: Coincident(g4,g3)
    c: Coincident(g4,g0)
    c: DistanceY(g1,g3) = 2
    c: Coincident(g5,g3)
    c: PointOnObject(g5,g2)
    c: Horizontal(g5)
    c: Angle(g5,g4) = 0.488692
FEATURE [PartDesign::Pad] Pad  label="ShieldCoverRails"
  BaseFeature = -> AdditiveLoft
  Direction = (1,1,1)
  Length = 63
  Length2 = 100
  Midplane = true
  Profile = -> Sketch022
  Type = 0
  expr: Length = <<params>>.ardcut_width + (<<params>>.rail_width + <<params>>.std_chamf) * 2
FEATURE [Sketcher::SketchObject] Sketch023  label="Sketch_RailSubLoft_Bot"
  FullyConstrained = true
  MapMode = 5
  Placement = pos=(0,0,3) rot=(0,0,1;0rad)
  Support = -> [DatumPlane]
  expr: Constraints[59] = <<params>>.std_rad
  expr: Constraints[41] = <<params>>.plate_width
  expr: Constraints[14] = <<params>>.tail_width
  expr: Constraints[13] = <<params>>.tail_rad
  expr: Constraints[29] = <<params>>.front_vert_edge
  expr: Constraints[32] = <<params>>.front_diameter
  expr: Constraints[89] = <<params>>.shell_overhang_leng + <<params>>.top_chamfer_width
  expr: Constraints[95] = <<params>>.shell_overhang_leng + <<params>>.top_chamfer_width
  expr: Constraints[88] = <<params>>.shell_overhang_leng + <<params>>.top_chamfer_width
  expr: Constraints[12] = <<params>>.plate_length
  expr: Constraints[31] = <<params>>.std_rad
  expr: Constraints[30] = <<params>>.back_vert_edge
  expr: Constraints[80] = <<params>>.shell_overhang_leng + <<params>>.top_chamfer_width
  expr: Constraints[61] = <<params>>.wheel_well_clearance
  expr: Constraints[23] = <<params>>.std_rad
  expr: Constraints[90] = <<params>>.shell_overhang_leng + <<params>>.top_chamfer_width
  sketch-geometry (44):
    g0: ArcOfCircle CenterX=0 CenterY=52.6846 CenterZ=0 NormalX=0 NormalY=0 NormalZ=1 AngleXU=0 Radius=112.5 StartAngle=3.96017 EndAngle=5.4646
    g1: LineSegment StartX=-77.1162 StartY=42.1781 StartZ=0 EndX=-29.0404 EndY=108.13 EndZ=0
    g2: LineSegment StartX=-25 StartY=110.185 StartZ=0 EndX=25 EndY=110.185 EndZ=0
    g3: LineSegment StartX=29.0404 StartY=108.13 StartZ=0 EndX=77.1162 EndY=42.1781 EndZ=0
    g4: LineSegment StartX=0 StartY=0 StartZ=0 EndX=0 EndY=110.185 EndZ=0
    g5: ArcOfCircle CenterX=-25 CenterY=105.185 CenterZ=0 NormalX=0 NormalY=0 NormalZ=1 AngleXU=0 Radius=5 StartAngle=1.5708 EndAngle=2.5117
    g6: ArcOfCircle CenterX=25 CenterY=105.185 CenterZ=0 NormalX=0 NormalY=0 NormalZ=1 AngleXU=0 Radius=5 StartAngle=0.629894 EndAngle=1.5708
    g7: GeomPoint X=0 Y=-59.8154 Z=0
    g8: LineSegment StartX=77.5 StartY=26 StartZ=0 EndX=77.5 EndY=41 EndZ=0
    g9: LineSegment StartX=77.5 StartY=-26 StartZ=0 EndX=77.5 EndY=-28 EndZ=0
    g10: LineSegment StartX=-77.5 StartY=26 StartZ=0 EndX=-77.5 EndY=41 EndZ=0
    g11: ArcOfCircle CenterX=75.5 CenterY=-28 CenterZ=0 NormalX=0 NormalY=0 NormalZ=1 AngleXU=0 Radius=2 StartAngle=5.4646 EndAngle=6.28319
    g12: ArcOfCircle CenterX=-75.5 CenterY=-28 CenterZ=0 NormalX=0 NormalY=0 NormalZ=1 AngleXU=0 Radius=2 StartAngle=3.14159 EndAngle=3.96017
    g13: ArcOfCircle CenterX=75.5 CenterY=41 CenterZ=0 NormalX=0 NormalY=0 NormalZ=1 AngleXU=0 Radius=2 StartAngle=1.4e-15 EndAngle=0.629894
    g14: ArcOfCircle CenterX=-75.5 CenterY=41 CenterZ=0 NormalX=0 NormalY=0 NormalZ=1 AngleXU=0 Radius=2 StartAngle=2.5117 EndAngle=3.14159
    g15: GeomPoint X=77.5 Y=0 Z=0
    g16: GeomPoint X=-77.5 Y=0 Z=0
    g17: LineSegment StartX=-77.5 StartY=-28 StartZ=0 EndX=-77.5 EndY=-26 EndZ=0
    g18: LineSegment StartX=-77.5 StartY=26 StartZ=0 EndX=-77.5 EndY=24 EndZ=0
    g19: LineSegment StartX=-77.5 StartY=24 StartZ=0 EndX=-77.5 EndY=-24 EndZ=0
    g20: LineSegment StartX=-77.5 StartY=-26 StartZ=0 EndX=-77.5 EndY=-24 EndZ=0
    g21: LineSegment StartX=77.5 StartY=26 StartZ=0 EndX=77.5 EndY=24 EndZ=0
    g22: LineSegment StartX=77.5 StartY=24 StartZ=0 EndX=77.5 EndY=-24 EndZ=0
    g23: LineSegment StartX=77.5 StartY=-24 StartZ=0 EndX=77.5 EndY=-26 EndZ=0
    g24: LineSegment StartX=-17.2131 StartY=94.8721 StartZ=0 EndX=17.2131 EndY=94.8721 EndZ=0
    g25: GeomPoint X=0 Y=94.8721 Z=0
    g26: LineSegment StartX=21.2535 StartY=92.8174 StartZ=0 EndX=61.8037 EndY=37.1894 EndZ=0
    g27: LineSegment StartX=62.1875 StartY=36.0113 StartZ=0 EndX=62.1875 EndY=-21.0591 EndZ=0
    g28: LineSegment StartX=-21.2535 StartY=92.8174 StartZ=0 EndX=-61.8037 EndY=37.1894 EndZ=0
    g29: LineSegment StartX=-62.1875 StartY=36.0113 StartZ=0 EndX=-62.1875 EndY=-21.0591 EndZ=0
    g30: ArcOfCircle CenterX=-17.2131 CenterY=89.8721 CenterZ=0 NormalX=0 NormalY=0 NormalZ=1 AngleXU=0 Radius=5 StartAngle=1.5708 EndAngle=2.5117
    g31: ArcOfCircle CenterX=17.2131 CenterY=89.8721 CenterZ=0 NormalX=0 NormalY=0 NormalZ=1 AngleXU=0 Radius=5 StartAngle=0.629894 EndAngle=1.5708
    g32: ArcOfCircle CenterX=60.1875 CenterY=36.0113 CenterZ=0 NormalX=0 NormalY=0 NormalZ=1 AngleXU=0 Radius=2 StartAngle=1.6e-15 EndAngle=0.629894
    g33: ArcOfCircle CenterX=-60.1875 CenterY=36.0113 CenterZ=0 NormalX=0 NormalY=0 NormalZ=1 AngleXU=0 Radius=2 StartAngle=2.5117 EndAngle=3.14159
    g34: ArcOfCircle CenterX=0 CenterY=52.6846 CenterZ=0 NormalX=0 NormalY=0 NormalZ=1 AngleXU=0 Radius=97.1875 StartAngle=4.02786 EndAngle=5.39691
    g35: GeomPoint X=0 Y=-44.5029 Z=0
    g36: ArcOfCircle CenterX=-60.1875 CenterY=-21.0591 CenterZ=0 NormalX=0 NormalY=0 NormalZ=1 AngleXU=0 Radius=2 StartAngle=3.14159 EndAngle=4.02786
    g37: ArcOfCircle CenterX=60.1875 CenterY=-21.0591 CenterZ=0 NormalX=0 NormalY=0 NormalZ=1 AngleXU=0 Radius=2 StartAngle=5.39691 EndAngle=6.28319
    g38: LineSegment StartX=-21.2535 StartY=92.8174 StartZ=0 EndX=-33.6274 EndY=101.837 EndZ=0
    g39: LineSegment StartX=-62.1875 StartY=36.0113 StartZ=0 EndX=-77.5 EndY=36.0113 EndZ=0
    g40: LineSegment StartX=-77.5 StartY=36.0113 StartZ=0 EndX=-77.5 EndY=110.185 EndZ=0
    g41: LineSegment StartX=62.1875 StartY=36.0113 StartZ=0 EndX=77.5 EndY=36.0113 EndZ=0
    g42: LineSegment StartX=77.5 StartY=36.0113 StartZ=0 EndX=77.5 EndY=110.185 EndZ=0
    g43: LineSegment StartX=-77.5 StartY=110.185 StartZ=0 EndX=77.5 EndY=110.185 EndZ=0
  constraints (112):
    c: PointOnObject(g0,g-2)
    c: Horizontal(g2)
    c: Coincident(g4,g-1)
    c: PointOnObject(g4,g-2)
    c: Tangent(g1,g5) = 1.5708
    c: Tangent(g2,g5) = 1.5708
    c: Tangent(g2,g6) = 1.5708
    c: Tangent(g3,g6) = 1.5708
    c: Equal(g6,g5)
    c: Symmetric(g2,g2,g4)
    c: PointOnObject(g7,g-2)
    c: PointOnObject(g7,g0)
    c: DistanceY(g7,g2) = 170
    c: Radius(g6) = 5
    c: DistanceX(g2,g2) = 50
    c: Vertical(g8)
    c: Vertical(g9)
    c: Vertical(g10)
    c: Equal(g1,g3)
    c: Tangent(g0,g11) = -1.5708
    c: Tangent(g9,g11) = 1.5708
    c: Tangent(g0,g12) = -1.5708
    c: Equal(g11,g12)
    c: Radius(g11) = 2
    c: Tangent(g8,g13) = -1.5708
    c: Tangent(g3,g13) = 1.5708
    c: Tangent(g1,g14) = 1.5708
    c: Tangent(g10,g14) = 1.5708
    c: Equal(g13,g14)
    c: DistanceY(g9,g9) = 2
    c: DistanceY(g8,g8) = 15
    c: Radius(g13) = 2
    c: Diameter(g0) = 225
    c: PointOnObject(g15,g-1)
    c: PointOnObject(g16,g-1)
    c: Symmetric(g10,g17,g16)
    c: Symmetric(g8,g9,g15)
    c: Coincident(g17,g12)
    c: Vertical(g17)
    c: Equal(g10,g8)
    c: Equal(g9,g17)
    c: DistanceX(g12,g9) = 155
    c: Coincident(g18,g10)
    c: Vertical(g18)
    c: Coincident(g19,g18)
    c: Vertical(g19)
    c: Coincident(g20,g17)
    c: Vertical(g20)
    c: Equal(g20,g18)
    c: Coincident(g19,g20)
    c: Tangent(g12,g17)
    c: Coincident(g21,g8)
    c: Vertical(g21)
    c: Coincident(g22,g21)
    c: Vertical(g22)
    c: Coincident(g23,g22)
    c: Coincident(g23,g9)
    c: Equal(g23,g21)
    c: Vertical(g23)
    c: DistanceY(g21,g8) = 2
    c: Equal(g18,g21)
    c: DistanceY(g22,g21) = 48
    c: Horizontal(g24)
    c: PointOnObject(g25,g-2)
    c: Vertical(g27)
    c: Vertical(g29)
    c: Tangent(g28,g30) = -1.5708
    c: Tangent(g24,g30) = 1.5708
    c: Tangent(g24,g31) = 1.5708
    c: Tangent(g26,g31) = 1.5708
    c: Tangent(g27,g32) = 1.5708
    c: Tangent(g26,g32) = 1.5708
    c: Tangent(g29,g33) = -1.5708
    c: Tangent(g28,g33) = -1.5708
    c: PointOnObject(g35,g-2)
    c: PointOnObject(g35,g34)
    c: Tangent(g34,g36) = -1.5708
    c: Tangent(g29,g36) = -1.5708
    c: Tangent(g34,g37) = -1.5708
    c: Tangent(g27,g37) = 1.5708
    c: DistanceY(g7,g35) = 15.3125
    c: Equal(g11,g37)
    c: Equal(g37,g32)
    c: Equal(g36,g37)
    c: Equal(g36,g33)
    c: Equal(g30,g31)
    c: Equal(g31,g6)
    c: Symmetric(g24,g24,g25)
    c: DistanceY(g25,g4) = 15.3125
    c: DistanceX(g27,g15) = 15.3125
    c: DistanceX(g16,g29) = 15.3125
    c: Coincident(g38,g28)
    c: PointOnObject(g38,g1)
    c: Perpendicular(g1,g38)
    c: Perpendicular(g28,g38)
    c: Distance(g38) = 15.3125
    c: Parallel(g26,g3)
    c: Coincident(g39,g29)
    c: PointOnObject(g39,g10)
    c: Horizontal(g39)
    c: Coincident(g40,g39)
    c: Vertical(g40)
    c: Coincident(g41,g27)
    c: PointOnObject(g41,g8)
    c: Horizontal(g41)
    c: Coincident(g42,g41)
    c: Vertical(g42)
    c: Coincident(g43,g40)
    c: Coincident(g43,g42)
    c: Horizontal(g43)
    c: Tangent(g43,g5)
    c: Coincident(g34,g0)
FEATURE [PartDesign::Plane] DatumPlane001  label="Datum_TopOfRails"
  AttachmentOffset = pos=(0,0,9) rot=(0,0,1;0rad)
  Length = 153.84
  MapMode = 5
  Placement = pos=(0,0,9) rot=(0,0,1;0rad)
  ResizeMode = 0
  Support = -> [XY_Plane001]
  Width = 168.645
  expr: .AttachmentOffset.Base.z = <<params>>.rail_height + <<params>>.plate_thick
FEATURE [Sketcher::SketchObject] Sketch024  label="Sketch_RailSubLoft_Top"
  FullyConstrained = true
  MapMode = 5
  Placement = pos=(0,0,9) rot=(0,0,1;0rad)
  Support = -> [DatumPlane001]
  expr: Constraints[90] = <<params>>.shell_overhang_leng + <<params>>.top_chamfer_width + <<params>>.rail_height / <<params>>.shell_wall_slope
  expr: Constraints[95] = <<params>>.shell_overhang_leng + <<params>>.top_chamfer_width + <<params>>.rail_height / <<params>>.shell_wall_slope
  expr: Constraints[89] = <<params>>.shell_overhang_leng + <<params>>.top_chamfer_width + <<params>>.rail_height / <<params>>.shell_wall_slope
  expr: Constraints[32] = <<params>>.front_diameter
  expr: Constraints[29] = <<params>>.front_vert_edge
  expr: Constraints[61] = <<params>>.wheel_well_clearance
  expr: Constraints[23] = <<params>>.std_rad
  expr: Constraints[80] = <<params>>.shell_overhang_leng + <<params>>.top_chamfer_width + <<params>>.rail_height / <<params>>.shell_wall_slope
  expr: Constraints[31] = <<params>>.std_rad
  expr: Constraints[30] = <<params>>.back_vert_edge
  expr: Constraints[12] = <<params>>.plate_length
  expr: Constraints[88] = <<params>>.shell_overhang_leng + <<params>>.top_chamfer_width + <<params>>.rail_height / <<params>>.shell_wall_slope
  expr: Constraints[13] = <<params>>.tail_rad
  expr: Constraints[41] = <<params>>.plate_width
  expr: Constraints[14] = <<params>>.tail_width
  expr: Constraints[59] = <<params>>.std_rad
  sketch-geometry (44):
    g0: ArcOfCircle CenterX=0 CenterY=52.6846 CenterZ=0 NormalX=0 NormalY=0 NormalZ=1 AngleXU=0 Radius=112.5 StartAngle=3.96017 EndAngle=5.4646
    g1: LineSegment StartX=-77.1162 StartY=42.1781 StartZ=0 EndX=-29.0404 EndY=108.13 EndZ=0
    g2: LineSegment StartX=-25 StartY=110.185 StartZ=0 EndX=25 EndY=110.185 EndZ=0
    g3: LineSegment StartX=29.0404 StartY=108.13 StartZ=0 EndX=77.1162 EndY=42.1781 EndZ=0
    g4: LineSegment StartX=0 StartY=0 StartZ=0 EndX=0 EndY=110.185 EndZ=0
    g5: ArcOfCircle CenterX=-25 CenterY=105.185 CenterZ=0 NormalX=0 NormalY=0 NormalZ=1 AngleXU=0 Radius=5 StartAngle=1.5708 EndAngle=2.5117
    g6: ArcOfCircle CenterX=25 CenterY=105.185 CenterZ=0 NormalX=0 NormalY=0 NormalZ=1 AngleXU=0 Radius=5 StartAngle=0.629894 EndAngle=1.5708
    g7: GeomPoint X=0 Y=-59.8154 Z=0
    g8: LineSegment StartX=77.5 StartY=26 StartZ=0 EndX=77.5 EndY=41 EndZ=0
    g9: LineSegment StartX=77.5 StartY=-26 StartZ=0 EndX=77.5 EndY=-28 EndZ=0
    g10: LineSegment StartX=-77.5 StartY=26 StartZ=0 EndX=-77.5 EndY=41 EndZ=0
    g11: ArcOfCircle CenterX=75.5 CenterY=-28 CenterZ=0 NormalX=0 NormalY=0 NormalZ=1 AngleXU=0 Radius=2 StartAngle=5.4646 EndAngle=6.28319
    g12: ArcOfCircle CenterX=-75.5 CenterY=-28 CenterZ=0 NormalX=0 NormalY=0 NormalZ=1 AngleXU=0 Radius=2 StartAngle=3.14159 EndAngle=3.96017
    g13: ArcOfCircle CenterX=75.5 CenterY=41 CenterZ=0 NormalX=0 NormalY=0 NormalZ=1 AngleXU=0 Radius=2 StartAngle=1.3e-15 EndAngle=0.629894
    g14: ArcOfCircle CenterX=-75.5 CenterY=41 CenterZ=0 NormalX=0 NormalY=0 NormalZ=1 AngleXU=0 Radius=2 StartAngle=2.5117 EndAngle=3.14159
    g15: GeomPoint X=77.5 Y=0 Z=0
    g16: GeomPoint X=-77.5 Y=0 Z=0
    g17: LineSegment StartX=-77.5 StartY=-28 StartZ=0 EndX=-77.5 EndY=-26 EndZ=0
    g18: LineSegment StartX=-77.5 StartY=26 StartZ=0 EndX=-77.5 EndY=24 EndZ=0
    g19: LineSegment StartX=-77.5 StartY=24 StartZ=0 EndX=-77.5 EndY=-24 EndZ=0
    g20: LineSegment StartX=-77.5 StartY=-26 StartZ=0 EndX=-77.5 EndY=-24 EndZ=0
    g21: LineSegment StartX=77.5 StartY=26 StartZ=0 EndX=77.5 EndY=24 EndZ=0
    g22: LineSegment StartX=77.5 StartY=24 StartZ=0 EndX=77.5 EndY=-24 EndZ=0
    g23: LineSegment StartX=77.5 StartY=-24 StartZ=0 EndX=77.5 EndY=-26 EndZ=0
    g24: LineSegment StartX=-15.8782 StartY=92.2471 StartZ=0 EndX=15.8782 EndY=92.2471 EndZ=0
    g25: GeomPoint X=0 Y=92.2471 Z=0
    g26: LineSegment StartX=19.9186 StartY=90.1924 StartZ=0 EndX=59.1787 EndY=36.3342 EndZ=0
    g27: LineSegment StartX=59.5625 StartY=35.1561 StartZ=0 EndX=59.5625 EndY=-19.8025 EndZ=0
    g28: LineSegment StartX=-19.9186 StartY=90.1924 StartZ=0 EndX=-59.1787 EndY=36.3342 EndZ=0
    g29: LineSegment StartX=-59.5625 StartY=35.1561 StartZ=0 EndX=-59.5625 EndY=-19.8025 EndZ=0
    g30: ArcOfCircle CenterX=-15.8782 CenterY=87.2471 CenterZ=0 NormalX=0 NormalY=0 NormalZ=1 AngleXU=0 Radius=5 StartAngle=1.5708 EndAngle=2.5117
    g31: ArcOfCircle CenterX=15.8782 CenterY=87.2471 CenterZ=0 NormalX=0 NormalY=0 NormalZ=1 AngleXU=0 Radius=5 StartAngle=0.629894 EndAngle=1.5708
    g32: ArcOfCircle CenterX=57.5625 CenterY=35.1561 CenterZ=0 NormalX=0 NormalY=0 NormalZ=1 AngleXU=0 Radius=2 StartAngle=3e-16 EndAngle=0.629894
    g33: ArcOfCircle CenterX=-57.5625 CenterY=35.1561 CenterZ=0 NormalX=0 NormalY=0 NormalZ=1 AngleXU=0 Radius=2 StartAngle=2.5117 EndAngle=3.14159
    g34: ArcOfCircle CenterX=0 CenterY=52.6846 CenterZ=0 NormalX=0 NormalY=0 NormalZ=1 AngleXU=0 Radius=94.5625 StartAngle=4.04125 EndAngle=5.38353
    g35: GeomPoint X=0 Y=-41.8779 Z=0
    g36: ArcOfCircle CenterX=-57.5625 CenterY=-19.8025 CenterZ=0 NormalX=0 NormalY=0 NormalZ=1 AngleXU=0 Radius=2 StartAngle=3.14159 EndAngle=4.04125
    g37: ArcOfCircle CenterX=57.5625 CenterY=-19.8025 CenterZ=0 NormalX=0 NormalY=0 NormalZ=1 AngleXU=0 Radius=2 StartAngle=5.38353 EndAngle=6.28319
    g38: LineSegment StartX=-19.9186 StartY=90.1924 StartZ=0 EndX=-34.4137 EndY=100.759 EndZ=0
    g39: LineSegment StartX=-59.5625 StartY=35.1561 StartZ=0 EndX=-77.5 EndY=35.1561 EndZ=0
    g40: LineSegment StartX=-77.5 StartY=35.1561 StartZ=0 EndX=-77.5 EndY=110.185 EndZ=0
    g41: LineSegment StartX=59.5625 StartY=35.1561 StartZ=0 EndX=77.5 EndY=35.1561 EndZ=0
    g42: LineSegment StartX=77.5 StartY=35.1561 StartZ=0 EndX=77.5 EndY=110.185 EndZ=0
    g43: LineSegment StartX=-77.5 StartY=110.185 StartZ=0 EndX=77.5 EndY=110.185 EndZ=0
  constraints (112):
    c: PointOnObject(g0,g-2)
    c: Horizontal(g2)
    c: Coincident(g4,g-1)
    c: PointOnObject(g4,g-2)
    c: Tangent(g1,g5) = 1.5708
    c: Tangent(g2,g5) = 1.5708
    c: Tangent(g2,g6) = 1.5708
    c: Tangent(g3,g6) = 1.5708
    c: Equal(g6,g5)
    c: Symmetric(g2,g2,g4)
    c: PointOnObject(g7,g-2)
    c: PointOnObject(g7,g0)
    c: DistanceY(g7,g2) = 170
    c: Radius(g6) = 5
    c: DistanceX(g2,g2) = 50
    c: Vertical(g8)
    c: Vertical(g9)
    c: Vertical(g10)
    c: Equal(g1,g3)
    c: Tangent(g0,g11) = -1.5708
    c: Tangent(g9,g11) = 1.5708
    c: Tangent(g0,g12) = -1.5708
    c: Equal(g11,g12)
    c: Radius(g11) = 2
    c: Tangent(g8,g13) = -1.5708
    c: Tangent(g3,g13) = 1.5708
    c: Tangent(g1,g14) = 1.5708
    c: Tangent(g10,g14) = 1.5708
    c: Equal(g13,g14)
    c: DistanceY(g9,g9) = 2
    c: DistanceY(g8,g8) = 15
    c: Radius(g13) = 2
    c: Diameter(g0) = 225
    c: PointOnObject(g15,g-1)
    c: PointOnObject(g16,g-1)
    c: Symmetric(g10,g17,g16)
    c: Symmetric(g8,g9,g15)
    c: Coincident(g17,g12)
    c: Vertical(g17)
    c: Equal(g10,g8)
    c: Equal(g9,g17)
    c: DistanceX(g12,g9) = 155
    c: Coincident(g18,g10)
    c: Vertical(g18)
    c: Coincident(g19,g18)
    c: Vertical(g19)
    c: Coincident(g20,g17)
    c: Vertical(g20)
    c: Equal(g20,g18)
    c: Coincident(g19,g20)
    c: Tangent(g12,g17)
    c: Coincident(g21,g8)
    c: Vertical(g21)
    c: Coincident(g22,g21)
    c: Vertical(g22)
    c: Coincident(g23,g22)
    c: Coincident(g23,g9)
    c: Equal(g23,g21)
    c: Vertical(g23)
    c: DistanceY(g21,g8) = 2
    c: Equal(g18,g21)
    c: DistanceY(g22,g21) = 48
    c: Horizontal(g24)
    c: PointOnObject(g25,g-2)
    c: Vertical(g27)
    c: Vertical(g29)
    c: Tangent(g28,g30) = -1.5708
    c: Tangent(g24,g30) = 1.5708
    c: Tangent(g24,g31) = 1.5708
    c: Tangent(g26,g31) = 1.5708
    c: Tangent(g27,g32) = 1.5708
    c: Tangent(g26,g32) = 1.5708
    c: Tangent(g29,g33) = -1.5708
    c: Tangent(g28,g33) = -1.5708
    c: PointOnObject(g35,g-2)
    c: PointOnObject(g35,g34)
    c: Tangent(g34,g36) = -1.5708
    c: Tangent(g29,g36) = -1.5708
    c: Tangent(g34,g37) = -1.5708
    c: Tangent(g27,g37) = 1.5708
    c: DistanceY(g7,g35) = 17.9375
    c: Equal(g11,g37)
    c: Equal(g37,g32)
    c: Equal(g36,g37)
    c: Equal(g36,g33)
    c: Equal(g30,g31)
    c: Equal(g31,g6)
    c: Symmetric(g24,g24,g25)
    c: DistanceY(g25,g4) = 17.9375
    c: DistanceX(g27,g15) = 17.9375
    c: DistanceX(g16,g29) = 17.9375
    c: Coincident(g38,g28)
    c: PointOnObject(g38,g1)
    c: Perpendicular(g1,g38)
    c: Perpendicular(g28,g38)
    c: Distance(g38) = 17.9375
    c: Parallel(g26,g3)
    c: Coincident(g39,g29)
    c: PointOnObject(g39,g10)
    c: Horizontal(g39)
    c: Coincident(g40,g39)
    c: Vertical(g40)
    c: Coincident(g41,g27)
    c: PointOnObject(g41,g8)
    c: Horizontal(g41)
    c: Coincident(g42,g41)
    c: Vertical(g42)
    c: Coincident(g43,g40)
    c: Coincident(g43,g42)
    c: Horizontal(g43)
    c: Tangent(g43,g5)
    c: Coincident(g34,g0)
FEATURE [PartDesign::SubtractiveLoft] SubtractiveLoft  label="TrimRails"
  BaseFeature = -> Pad
  Closed = false
  Profile = -> Sketch023
  Ruled = false
  Sections = -> [Sketch024]
FEATURE [PartDesign::Pocket] Pocket  label="ArduinoCutOut"
  BaseFeature = -> SubtractiveLoft
  Length = 5
  Length2 = 100
  Profile = -> Sketch
  Reversed = true
  Type = 1
FEATURE [PartDesign::Pocket] Pocket001  label="ShellMountHoles"
  BaseFeature = -> Pocket
  Length = 5
  Length2 = 100
  Midplane = true
  Profile = -> Sketch021
  Reversed = true
  Type = 1
FEATURE [Sketcher::SketchObject] Sketch025
  FullyConstrained = true
  MapMode = 5
  Placement = pos=(0,0,0) rot=(1,0,0;1.5708rad)
  Support = -> [XZ_Plane001]
  expr: Constraints[50] = <<params>>.std_chamf
  expr: Constraints[14] = <<params>>.std_chamf * 3
  expr: Constraints[49] = <<params>>.rail_height
  expr: Constraints[15] = <<params>>.ardcut_width
  expr: Constraints[48] = <<params>>.rail_height * 2
  expr: Constraints[16] = <<params>>.plate_thick
  expr: Constraints[68] = <<params>>.std_chamf
  expr: Constraints[47] = <<params>>.rail_width
  expr: Constraints[67] = <<params>>.std_chamf
  sketch-geometry (26):
    g0: LineSegment StartX=-24.5 StartY=3 StartZ=0 EndX=24.5 EndY=3 EndZ=0
    g1: LineSegment StartX=24.5 StartY=3 StartZ=0 EndX=27.5 EndY=6 EndZ=0
    g2: LineSegment StartX=-24.5 StartY=3 StartZ=0 EndX=-27.5 EndY=6 EndZ=0
    g3: LineSegment StartX=-27.5 StartY=6 StartZ=0 EndX=-27.5 EndY=8 EndZ=0
    g4: LineSegment StartX=27.5 StartY=8 StartZ=0 EndX=27.5 EndY=6 EndZ=0
    g5: LineSegment StartX=-27.5 StartY=6 StartZ=0 EndX=27.5 EndY=6 EndZ=0
    g6: GeomPoint X=0 Y=3 Z=0
    g7: LineSegment StartX=-27.5 StartY=8 StartZ=0 EndX=27.5 EndY=8 EndZ=0
    g8: LineSegment StartX=-29.5 StartY=9 StartZ=0 EndX=-30.5 EndY=8 EndZ=0
    g9: LineSegment StartX=-30.5 StartY=8 StartZ=0 EndX=-30.5 EndY=4 EndZ=0
    g10: LineSegment StartX=-30.5 StartY=4 StartZ=0 EndX=-31.5 EndY=3 EndZ=0
    g11: LineSegment StartX=-31.5 StartY=3 StartZ=0 EndX=-31.5 EndY=15 EndZ=0
    g12: LineSegment StartX=29.5 StartY=9 StartZ=0 EndX=30.5 EndY=8 EndZ=0
    g13: LineSegment StartX=30.5 StartY=8 StartZ=0 EndX=30.5 EndY=4 EndZ=0
    g14: LineSegment StartX=30.5 StartY=4 StartZ=0 EndX=31.5 EndY=3 EndZ=0
    g15: LineSegment StartX=31.5 StartY=3 StartZ=0 EndX=31.5 EndY=15 EndZ=0
    g16: LineSegment StartX=-31.5 StartY=15 StartZ=0 EndX=31.5 EndY=15 EndZ=0
    g17: LineSegment StartX=24.5 StartY=3 StartZ=0 EndX=31.5 EndY=3 EndZ=0
    g18: LineSegment StartX=30.5 StartY=8 StartZ=0 EndX=27.5 EndY=8 EndZ=0
    g19: LineSegment StartX=-30.5 StartY=8 StartZ=0 EndX=-27.5 EndY=8 EndZ=0
    g20: LineSegment StartX=-31.5 StartY=3 StartZ=0 EndX=-24.5 EndY=3 EndZ=0
    g21: LineSegment StartX=-29.5 StartY=9 StartZ=0 EndX=-28.5 EndY=9 EndZ=0
    g22: LineSegment StartX=-28.5 StartY=9 StartZ=0 EndX=-27.5 EndY=8 EndZ=0
    g23: LineSegment StartX=27.5 StartY=8 StartZ=0 EndX=28.5 EndY=9 EndZ=0
    g24: LineSegment StartX=28.5 StartY=9 StartZ=0 EndX=29.5 EndY=9 EndZ=0
    g25: LineSegment StartX=-28.5 StartY=9 StartZ=0 EndX=28.5 EndY=9 EndZ=0
  constraints (71):
    c: Horizontal(g0)
    c: Coincident(g1,g0)
    c: Coincident(g2,g0)
    c: Coincident(g3,g2)
    c: Vertical(g3)
    c: Coincident(g4,g1)
    c: Vertical(g4)
    c: Coincident(g5,g2)
    c: Coincident(g5,g1)
    c: Horizontal(g5)
    c: Angle(g2,g5) = 0.785398
    c: Angle(g5,g1) = 0.785398
    c: PointOnObject(g6,g-2)
    c: Symmetric(g0,g0,g6)
    c: DistanceY(g0,g1) = 3
    c: DistanceX(g2,g1) = 55
    c: DistanceY(g-1,g6) = 3
    c: Coincident(g7,g3)
    c: Coincident(g7,g4)
    c: Horizontal(g7)
    c: Coincident(g9,g8)
    c: Vertical(g9)
    c: Coincident(g10,g9)
    c: Coincident(g11,g10)
    c: Vertical(g11)
    c: Vertical(g13)
    c: Coincident(g14,g13)
    c: Coincident(g15,g14)
    c: Vertical(g15)
    c: Coincident(g16,g11)
    c: Coincident(g16,g15)
    c: Horizontal(g16)
    c: Coincident(g17,g0)
    c: Horizontal(g17)
    c: Coincident(g17,g14)
    c: Coincident(g18,g13)
    c: PointOnObject(g18,g4)
    c: Horizontal(g18)
    c: Coincident(g19,g8)
    c: PointOnObject(g19,g3)
    c: Horizontal(g19)
    c: Coincident(g20,g10)
    c: Coincident(g20,g0)
    c: Horizontal(g20)
    c: Coincident(g12,g13)
    c: Angle(g12,g18) = 0.785398
    c: Angle(g19,g8) = 0.785398
    c: DistanceX(g4,g12) = 3
    c: DistanceY(g14,g15) = 12
    c: DistanceY(g14,g12) = 6
    c: DistanceY(g12,g12) = 1
    c: Equal(g8,g12)
    c: Coincident(g21,g8)
    c: Horizontal(g21)
    c: Coincident(g22,g21)
    c: Coincident(g22,g3)
    c: PointOnObject(g3,g19)
    c: Equal(g22,g8)
    c: Coincident(g23,g4)
    c: Coincident(g24,g23)
    c: Coincident(g24,g12)
    c: Horizontal(g24)
    c: PointOnObject(g4,g18)
    c: Equal(g12,g23)
    c: Coincident(g25,g23)
    c: Coincident(g25,g21)
    c: Equal(g20,g17)
    c: DistanceY(g14,g13) = 1
    c: DistanceY(g10,g9) = 1
    c: Angle(g20,g10) = 0.785398
    c: Angle(g14,g17) = 0.785398
FEATURE [PartDesign::Pocket] Pocket002  label="SculptRails"
  BaseFeature = -> Pocket001
  Length = 5
  Length2 = 100
  Midplane = true
  Profile = -> Sketch025
  Type = 1
FEATURE [Sketcher::SketchObject] Sketch026  label="Sketch_TouchSensMount"
  FullyConstrained = true
  MapMode = 5
  Support = -> [XY_Plane001]
  expr: Constraints[21] = <<params>>.m2_hole_clear_diam
  expr: Constraints[56] = <<params>>.std_rad / 2
  expr: Constraints[64] = <<params>>.sens_touch_offset_leng
  sketch-geometry (28):
    g0: LineSegment StartX=-20 StartY=-15 StartZ=0 EndX=20 EndY=-15 EndZ=0
    g1: LineSegment StartX=20 StartY=-15 StartZ=0 EndX=20 EndY=-35 EndZ=0
    g2: LineSegment StartX=20 StartY=-35 StartZ=0 EndX=-20 EndY=-35 EndZ=0
    g3: LineSegment StartX=-20 StartY=-35 StartZ=0 EndX=-20 EndY=-15 EndZ=0
    g4: LineSegment StartX=0 StartY=0 StartZ=0 EndX=0 EndY=-15 EndZ=0
    g5: Circle CenterX=20 CenterY=-15 CenterZ=0 NormalX=0 NormalY=0 NormalZ=1 AngleXU=0 Radius=1.2
    g6: Circle CenterX=20 CenterY=-35 CenterZ=0 NormalX=0 NormalY=0 NormalZ=1 AngleXU=0 Radius=1.2
    g7: Circle CenterX=-20 CenterY=-35 CenterZ=0 NormalX=0 NormalY=0 NormalZ=1 AngleXU=0 Radius=1.2
    g8: Circle CenterX=-20 CenterY=-15 CenterZ=0 NormalX=0 NormalY=0 NormalZ=1 AngleXU=0 Radius=1.2
    g9: GeomPoint X=-1.1e-15 Y=-25 Z=0
    g10: LineSegment StartX=-31 StartY=-14.5 StartZ=0 EndX=31 EndY=-14.5 EndZ=0
    g11: LineSegment StartX=31 StartY=-14.5 StartZ=0 EndX=31 EndY=-35.5 EndZ=0
    g12: LineSegment StartX=31 StartY=-35.5 StartZ=0 EndX=-31 EndY=-35.5 EndZ=0
    g13: LineSegment StartX=-31 StartY=-35.5 StartZ=0 EndX=-31 EndY=-14.5 EndZ=0
    g14: Circle CenterX=-31 CenterY=-14.5 CenterZ=0 NormalX=0 NormalY=0 NormalZ=1 AngleXU=0 Radius=2.5
    g15: Circle CenterX=31 CenterY=-14.5 CenterZ=0 NormalX=0 NormalY=0 NormalZ=1 AngleXU=0 Radius=2.5
    g16: Circle CenterX=31 CenterY=-35.5 CenterZ=0 NormalX=0 NormalY=0 NormalZ=1 AngleXU=0 Radius=2.5
    g17: Circle CenterX=-31 CenterY=-35.5 CenterZ=0 NormalX=0 NormalY=0 NormalZ=1 AngleXU=0 Radius=2.5
    g18: LineSegment StartX=21 StartY=-18.5 StartZ=0 EndX=34 EndY=-18.5 EndZ=0
    g19: LineSegment StartX=35 StartY=-19.5 StartZ=0 EndX=35 EndY=-30.5 EndZ=0
    g20: LineSegment StartX=34 StartY=-31.5 StartZ=0 EndX=21 EndY=-31.5 EndZ=0
    g21: LineSegment StartX=20 StartY=-30.5 StartZ=0 EndX=20 EndY=-19.5 EndZ=0
    g22: ArcOfCircle CenterX=21 CenterY=-19.5 CenterZ=0 NormalX=0 NormalY=0 NormalZ=1 AngleXU=0 Radius=1 StartAngle=1.5708 EndAngle=3.14159
    g23: ArcOfCircle CenterX=34 CenterY=-19.5 CenterZ=0 NormalX=0 NormalY=0 NormalZ=1 AngleXU=0 Radius=1 StartAngle=5e-16 EndAngle=1.5708
    g24: ArcOfCircle CenterX=34 CenterY=-30.5 CenterZ=0 NormalX=0 NormalY=0 NormalZ=1 AngleXU=0 Radius=1 StartAngle=4.71239 EndAngle=6.28319
    g25: ArcOfCircle CenterX=21 CenterY=-30.5 CenterZ=0 NormalX=0 NormalY=0 NormalZ=1 AngleXU=0 Radius=1 StartAngle=3.14159 EndAngle=4.71239
    g26: GeomPoint X=20 Y=-25 Z=0
    g27: LineSegment StartX=-1.1e-15 StartY=-25 StartZ=0 EndX=20 EndY=-25 EndZ=0
  constraints (65):
    c: Coincident(g0,g1)
    c: Coincident(g1,g2)
    c: Coincident(g2,g3)
    c: Coincident(g3,g0)
    c: Horizontal(g0)
    c: Horizontal(g2)
    c: Vertical(g1)
    c: Vertical(g3)
    c: Coincident(g4,g-1)
    c: PointOnObject(g4,g-2)
    c: Symmetric(g0,g0,g4)
    c: Distance(g1) = 20
    c: Distance(g0) = 40
    c: Coincident(g5,g0)
    c: Coincident(g6,g1)
    c: Coincident(g7,g2)
    c: Coincident(g8,g0)
    c: Symmetric(g5,g7,g9)
    c: Equal(g5,g8)
    c: Equal(g8,g7)
    c: Equal(g7,g6)
    c: Diameter(g5) = 2.4
    c: Coincident(g10,g11)
    c: Coincident(g11,g12)
    c: Coincident(g12,g13)
    c: Coincident(g13,g10)
    c: Horizontal(g10)
    c: Horizontal(g12)
    c: Vertical(g11)
    c: Vertical(g13)
    c: Symmetric(g12,g10,g9)
    c: Distance(g10) = 62
    c: Distance(g11) = 21
    c: Coincident(g14,g10)
    c: Coincident(g15,g10)
    c: Coincident(g16,g11)
    c: Coincident(g17,g12)
    c: Equal(g15,g16)
    c: Equal(g16,g17)
    c: Equal(g17,g14)
    c: Diameter(g15) = 5
    c: Horizontal(g18)
    c: Horizontal(g20)
    c: Vertical(g19)
    c: Vertical(g21)
    c: Tangent(g21,g22) = 1.5708
    c: Tangent(g18,g22) = 1.5708
    c: Tangent(g18,g23) = 1.5708
    c: Tangent(g19,g23) = 1.5708
    c: Tangent(g19,g24) = 1.5708
    c: Tangent(g20,g24) = 1.5708
    c: Tangent(g20,g25) = 1.5708
    c: Tangent(g21,g25) = 1.5708
    c: Equal(g24,g23)
    c: Equal(g24,g25)
    c: Equal(g25,g22)
    c: Radius(g23) = 1
    c: DistanceX(g21,g19) = 15
    c: DistanceY(g20,g18) = 13
    c: Symmetric(g21,g21,g26)
    c: Coincident(g27,g9)
    c: Coincident(g27,g26)
    c: Horizontal(g27)
    c: Distance(g27) = 20
    c: DistanceY(g9,g-1) = 25
FEATURE [PartDesign::Pocket] Pocket003  label="TouchSens_HoleMts"
  BaseFeature = -> Pocket002
  Length = 5
  Length2 = 100
  Profile = -> Sketch026
  Reversed = true
  Type = 1
FEATURE [PartDesign::Plane] DatumPlane002  label="Datum_ChamfRailSlope"
  AttachmentOffset = pos=(0,5,9) rot=(1,0,0;0.488692rad)
  Length = 150.716
  MapMode = 5
  Placement = pos=(0,-9,5) rot=(1,0,0;2.05949rad)
  ResizeMode = 0
  Support = -> [XZ_Plane001]
  Width = 134.437
  expr: .AttachmentOffset.Base.z = <<params>>.rail_front_offset_leng
  expr: .AttachmentOffset.Rotation.Roll = <<params>>.rail_front_angle
  expr: .AttachmentOffset.Base.y = <<params>>.plate_thick + <<params>>.rail_front_vert_height
FEATURE [Sketcher::SketchObject] Sketch027  label="Sketch_ChamfFrontRail"
  FullyConstrained = true
  MapMode = 5
  Placement = pos=(0,-9,5) rot=(1,0,0;2.05949rad)
  Support = -> [DatumPlane002]
  expr: Constraints[14] = <<params>>.ardcut_width + <<params>>.rail_width * 2
  expr: Constraints[27] = <<params>>.rail_width
  expr: Constraints[15] = <<params>>.std_chamf
  expr: Constraints[16] = <<params>>.rail_height
  sketch-geometry (12):
    g0: LineSegment StartX=-29.5 StartY=0 StartZ=0 EndX=-30.5 EndY=-1 EndZ=0
    g1: LineSegment StartX=-30.5 StartY=-1 StartZ=0 EndX=-30.5 EndY=5 EndZ=0
    g2: LineSegment StartX=-30.5 StartY=5 StartZ=0 EndX=30.5 EndY=5 EndZ=0
    g3: LineSegment StartX=30.5 StartY=5 StartZ=0 EndX=30.5 EndY=-1 EndZ=0
    g4: LineSegment StartX=30.5 StartY=-1 StartZ=0 EndX=29.5 EndY=0 EndZ=0
    g5: LineSegment StartX=-30.5 StartY=-1 StartZ=0 EndX=30.5 EndY=-1 EndZ=0
    g6: LineSegment StartX=-29.5 StartY=0 StartZ=0 EndX=-28.5 EndY=0 EndZ=0
    g7: LineSegment StartX=-28.5 StartY=0 StartZ=0 EndX=-27.5 EndY=-1 EndZ=0
    g8: LineSegment StartX=29.5 StartY=0 StartZ=0 EndX=28.5 EndY=0 EndZ=0
    g9: LineSegment StartX=28.5 StartY=0 StartZ=0 EndX=27.5 EndY=-1 EndZ=0
    g10: LineSegment StartX=27.5 StartY=-1 StartZ=0 EndX=-27.5 EndY=-1 EndZ=0
    g11: LineSegment StartX=28.5 StartY=0 StartZ=0 EndX=-28.5 EndY=0 EndZ=0
  constraints (33):
    c: Coincident(g1,g0)
    c: Vertical(g1)
    c: Coincident(g2,g1)
    c: Horizontal(g2)
    c: Coincident(g3,g2)
    c: Vertical(g3)
    c: Coincident(g4,g3)
    c: PointOnObject(g4,g-1)
    c: Coincident(g5,g0)
    c: Coincident(g5,g3)
    c: Horizontal(g5)
    c: Angle(g4,g5) = 0.785398
    c: Angle(g5,g0) = 0.785398
    c: Symmetric(g0,g4,g-1)
    c: DistanceX(g0,g3) = 61
    c: DistanceY(g3,g4) = 1
    c: DistanceY(g3,g2) = 6
    c: Coincident(g6,g0)
    c: PointOnObject(g6,g-1)
    c: Coincident(g7,g6)
    c: PointOnObject(g7,g5)
    c: Coincident(g8,g4)
    c: PointOnObject(g8,g-1)
    c: Coincident(g9,g8)
    c: PointOnObject(g9,g5)
    c: Coincident(g10,g9)
    c: Coincident(g10,g7)
    c: DistanceX(g9,g3) = 3
    c: Equal(g9,g4)
    c: Equal(g7,g0)
    c: Equal(g6,g8)
    c: Coincident(g11,g8)
    c: Coincident(g11,g6)
FEATURE [PartDesign::Pocket] Pocket004  label="ChamfFrontOfRail"
  BaseFeature = -> Pocket003
  Length = 50
  Length2 = 1
  Profile = -> Sketch027
  Type = 4
FEATURE [PartDesign::Plane] DatumPlane003  label="Datum_AngleEnd"
  AttachmentOffset = pos=(0,0,-23) rot=(0,0,1;0rad)
  Length = 91.1379
  MapMode = 5
  Placement = pos=(0,23,5.1e-15) rot=(1,0,0;1.5708rad)
  ResizeMode = 0
  Support = -> [XZ_Plane002]
  Width = 62.5379
  expr: .AttachmentOffset.Base.z = Spreadsheet.coverfront_angle_leng * -1
FEATURE [Sketcher::SketchObject] Sketch028  label="Sketch_Cover_Front"
  FullyConstrained = true
  MapMode = 5
  Placement = pos=(0,0,0) rot=(1,0,0;1.5708rad)
  Support = -> [XZ_Plane003]
  expr: Constraints[38] = Spreadsheet.coverfront_std_rad
  expr: Constraints[39] = Spreadsheet.coverfront_std_rad
  expr: Constraints[64] = Spreadsheet.coverfront_foot_width
  expr: Constraints[63] = <<params>>.ardcut_width + (<<params>>.rail_width + Spreadsheet.coverfront_tol) * 2
  expr: Constraints[40] = <<params>>.std_chamf
  expr: Constraints[59] = <<params>>.std_chamf
  expr: Constraints[42] = Spreadsheet.coverfront_wall_thick
  expr: Constraints[43] = <<params>>.coverfront_wall_thick
  expr: Constraints[46] = <<params>>.front_vert_edge + <<params>>.coverfront_tol
  expr: Constraints[41] = Spreadsheet.coverfront_foot_height
  sketch-geometry (30):
    g0: LineSegment StartX=-39.3 StartY=0 StartZ=0 EndX=-39.3 EndY=1.2 EndZ=0
    g1: LineSegment StartX=-38.5 StartY=2 StartZ=0 EndX=-33.1 EndY=2 EndZ=0
    g2: LineSegment StartX=-32.3 StartY=2.8 StartZ=0 EndX=-32.3 EndY=3 EndZ=0
    g3: LineSegment StartX=-31.5 StartY=3.8 StartZ=0 EndX=31.5 EndY=3.8 EndZ=0
    g4: LineSegment StartX=32.3 StartY=3 StartZ=0 EndX=32.3 EndY=2.8 EndZ=0
    g5: LineSegment StartX=33.1 StartY=2 StartZ=0 EndX=38.5 EndY=2 EndZ=0
    g6: LineSegment StartX=39.3 StartY=1.2 StartZ=0 EndX=39.3 EndY=0 EndZ=0
    g7: LineSegment StartX=-39.3 StartY=0 StartZ=0 EndX=-31.7 EndY=0 EndZ=0
    g8: LineSegment StartX=31.7 StartY=0 StartZ=0 EndX=39.3 EndY=0 EndZ=0
    g9: ArcOfCircle CenterX=-31.5 CenterY=3 CenterZ=0 NormalX=0 NormalY=0 NormalZ=1 AngleXU=0 Radius=0.8 StartAngle=1.5708 EndAngle=3.14159
    g10: ArcOfCircle CenterX=31.5 CenterY=3 CenterZ=0 NormalX=0 NormalY=0 NormalZ=1 AngleXU=0 Radius=0.8 StartAngle=0 EndAngle=1.5708
    g11: ArcOfCircle CenterX=38.5 CenterY=1.2 CenterZ=0 NormalX=0 NormalY=0 NormalZ=1 AngleXU=0 Radius=0.8 StartAngle=0 EndAngle=1.5708
    g12: ArcOfCircle CenterX=-38.5 CenterY=1.2 CenterZ=0 NormalX=0 NormalY=0 NormalZ=1 AngleXU=0 Radius=0.8 StartAngle=1.5708 EndAngle=3.14159
    g13: ArcOfCircle CenterX=-33.1 CenterY=2.8 CenterZ=0 NormalX=0 NormalY=0 NormalZ=1 AngleXU=0 Radius=0.8 StartAngle=4.71239 EndAngle=6.28319
    g14: ArcOfCircle CenterX=33.1 CenterY=2.8 CenterZ=0 NormalX=0 NormalY=0 NormalZ=1 AngleXU=0 Radius=0.8 StartAngle=3.14159 EndAngle=4.71239
    g15: LineSegment StartX=-30.7 StartY=1.2 StartZ=0 EndX=-29.7 EndY=2.2 EndZ=0
    g16: LineSegment StartX=-29.7 StartY=2.2 StartZ=0 EndX=29.7 EndY=2.2 EndZ=0
    g17: LineSegment StartX=29.7 StartY=2.2 StartZ=0 EndX=30.7 EndY=1.2 EndZ=0
    g18: LineSegment StartX=-30.7 StartY=1.2 StartZ=0 EndX=30.7 EndY=1.2 EndZ=0
    g19: GeomPoint X=0 Y=3.8 Z=0
    g20: GeomPoint X=-1.1e-15 Y=2.2 Z=0
    g21: LineSegment StartX=-30.7 StartY=1.2 StartZ=0 EndX=-30.7 EndY=1 EndZ=0
    g22: LineSegment StartX=-31.7 StartY=0 StartZ=0 EndX=-30.7 EndY=1 EndZ=0
    g23: LineSegment StartX=31.7 StartY=0 StartZ=0 EndX=30.7 EndY=1 EndZ=0
    g24: LineSegment StartX=30.7 StartY=1 StartZ=0 EndX=30.7 EndY=1.2 EndZ=0
    g25: LineSegment StartX=-30.7 StartY=1 StartZ=0 EndX=30.7 EndY=1 EndZ=0
    g26: LineSegment StartX=-39.3 StartY=1.2 StartZ=0 EndX=-39.3 EndY=2 EndZ=0
    g27: LineSegment StartX=-38.5 StartY=2 StartZ=0 EndX=-39.3 EndY=2 EndZ=0
    g28: LineSegment StartX=38.5 StartY=2 StartZ=0 EndX=39.3 EndY=2 EndZ=0
    g29: LineSegment StartX=39.3 StartY=1.2 StartZ=0 EndX=39.3 EndY=2 EndZ=0
  constraints (75):
    c: PointOnObject(g0,g-1)
    c: Vertical(g0)
    c: Horizontal(g1)
    c: Vertical(g2)
    c: Horizontal(g3)
    c: Vertical(g4)
    c: Horizontal(g5)
    c: PointOnObject(g6,g-1)
    c: Vertical(g6)
    c: Coincident(g7,g0)
    c: PointOnObject(g7,g-1)
    c: Coincident(g8,g6)
    c: Symmetric(g7,g8,g-1)
    c: Tangent(g2,g9) = 1.5708
    c: Tangent(g3,g9) = 1.5708
    c: Tangent(g4,g10) = 1.5708
    c: Tangent(g3,g10) = 1.5708
    c: Tangent(g5,g11) = 1.5708
    c: Tangent(g6,g11) = 1.5708
    c: Tangent(g0,g12) = 1.5708
    c: Tangent(g1,g12) = 1.5708
    c: Tangent(g1,g13) = -1.5708
    c: Tangent(g2,g13) = -1.5708
    c: Tangent(g5,g14) = -1.5708
    c: Tangent(g4,g14) = -1.5708
    c: Coincident(g16,g15)
    c: Horizontal(g16)
    c: Coincident(g17,g16)
    c: Horizontal(g18)
    c: Angle(g18,g15) = 0.785398
    c: Angle(g17,g18) = 0.785398
    c: PointOnObject(g19,g-2)
    c: Symmetric(g15,g16,g20)
    c: Symmetric(g3,g3,g19)
    c: Equal(g9,g10)
    c: Equal(g14,g11)
    c: Equal(g13,g12)
    c: Equal(g13,g14)
    c: Radius(g11) = 0.8
    c: Radius(g10) = 0.8
    c: DistanceY(g17,g16) = 1
    c: DistanceY(g6,g5) = 2
    c: DistanceX(g17,g4) = 1.6
    c: DistanceY(g20,g19) = 1.6
    c: Equal(g6,g0)
    c: Equal(g5,g1)
    c: DistanceY(g-1,g20) = 2.2
    c: Coincident(g18,g17)
    c: Coincident(g15,g18)
    c: Coincident(g21,g15)
    c: Vertical(g21)
    c: Coincident(g22,g7)
    c: Coincident(g22,g21)
    c: Coincident(g23,g8)
    c: Coincident(g24,g23)
    c: Coincident(g24,g17)
    c: Vertical(g24)
    c: Angle(g23,g-1) = 0.785398
    c: Angle(g-1,g22) = 0.785398
    c: DistanceY(g7,g21) = 1
    c: Coincident(g25,g21)
    c: Coincident(g25,g23)
    c: Horizontal(g25)
    c: DistanceX(g21,g23) = 61.4
    c: DistanceX(g4,g6) = 7
    c: Coincident(g26,g0)
    c: Vertical(g26)
    c: Coincident(g27,g1)
    c: Coincident(g27,g26)
    c: Horizontal(g27)
    c: Coincident(g28,g5)
    c: Horizontal(g28)
    c: Coincident(g29,g6)
    c: Coincident(g29,g28)
    c: Vertical(g29)
FEATURE [Sketcher::SketchObject] Sketch029  label="Sketch_Cover_Back"
  FullyConstrained = true
  MapMode = 5
  Placement = pos=(0,23,5.1e-15) rot=(1,0,0;1.5708rad)
  Support = -> [DatumPlane003]
  expr: Constraints[39] = Spreadsheet.coverfront_foot_height
  expr: Constraints[62] = Spreadsheet.coverfront_foot_width
  expr: Constraints[44] = <<params>>.coverfront_under_height
  expr: Constraints[57] = <<params>>.std_chamf
  expr: Constraints[41] = Spreadsheet.coverfront_wall_thick
  expr: Constraints[40] = Spreadsheet.coverfront_wall_thick
  expr: Constraints[38] = <<params>>.std_chamf
  expr: Constraints[61] = <<params>>.ardcut_width + (<<params>>.rail_width + Spreadsheet.coverfront_tol) * 2
  expr: Constraints[73] = <<params>>.std_rad
  expr: Constraints[37] = Spreadsheet.coverfront_std_rad
  expr: Constraints[36] = Spreadsheet.coverfront_std_rad
  sketch-geometry (30):
    g0: LineSegment StartX=-39.3 StartY=0 StartZ=0 EndX=-39.3 EndY=1.2 EndZ=0
    g1: LineSegment StartX=-38.5 StartY=2 StartZ=0 EndX=-34.3 EndY=2 EndZ=0
    g2: LineSegment StartX=-32.3 StartY=4 StartZ=0 EndX=-32.3 EndY=15.2293 EndZ=0
    g3: LineSegment StartX=-31.5 StartY=16.0293 StartZ=0 EndX=31.5 EndY=16.0293 EndZ=0
    g4: LineSegment StartX=32.3 StartY=15.2293 StartZ=0 EndX=32.3 EndY=4 EndZ=0
    g5: LineSegment StartX=34.3 StartY=2 StartZ=0 EndX=38.5 EndY=2 EndZ=0
    g6: LineSegment StartX=39.3 StartY=1.2 StartZ=0 EndX=39.3 EndY=0 EndZ=0
    g7: LineSegment StartX=-39.3 StartY=0 StartZ=0 EndX=-31.7 EndY=0 EndZ=0
    g8: LineSegment StartX=31.7 StartY=0 StartZ=0 EndX=39.3 EndY=0 EndZ=0
    g9: ArcOfCircle CenterX=-31.5 CenterY=15.2293 CenterZ=0 NormalX=0 NormalY=0 NormalZ=1 AngleXU=0 Radius=0.8 StartAngle=1.5708 EndAngle=3.14159
    g10: ArcOfCircle CenterX=31.5 CenterY=15.2293 CenterZ=0 NormalX=0 NormalY=0 NormalZ=1 AngleXU=0 Radius=0.8 StartAngle=8e-16 EndAngle=1.5708
    g11: ArcOfCircle CenterX=38.5 CenterY=1.2 CenterZ=0 NormalX=0 NormalY=0 NormalZ=1 AngleXU=0 Radius=0.8 StartAngle=0 EndAngle=1.5708
    g12: ArcOfCircle CenterX=-38.5 CenterY=1.2 CenterZ=0 NormalX=0 NormalY=0 NormalZ=1 AngleXU=0 Radius=0.8 StartAngle=1.5708 EndAngle=3.14159
    g13: ArcOfCircle CenterX=-34.3 CenterY=4 CenterZ=0 NormalX=0 NormalY=0 NormalZ=1 AngleXU=0 Radius=2 StartAngle=4.71239 EndAngle=6.28319
    g14: ArcOfCircle CenterX=34.3 CenterY=4 CenterZ=0 NormalX=0 NormalY=0 NormalZ=1 AngleXU=0 Radius=2 StartAngle=3.14159 EndAngle=4.71239
    g15: LineSegment StartX=-30.7 StartY=13.4293 StartZ=0 EndX=-29.7 EndY=14.4293 EndZ=0
    g16: LineSegment StartX=-29.7 StartY=14.4293 StartZ=0 EndX=29.7 EndY=14.4293 EndZ=0
    g17: LineSegment StartX=29.7 StartY=14.4293 StartZ=0 EndX=30.7 EndY=13.4293 EndZ=0
    g18: LineSegment StartX=-30.7 StartY=13.4293 StartZ=0 EndX=30.7 EndY=13.4293 EndZ=0
    g19: GeomPoint X=0 Y=16.0293 Z=0
    g20: GeomPoint X=-4e-16 Y=14.4293 Z=0
    g21: LineSegment StartX=-30.7 StartY=13.4293 StartZ=0 EndX=-30.7 EndY=1 EndZ=0
    g22: LineSegment StartX=-31.7 StartY=0 StartZ=0 EndX=-30.7 EndY=1 EndZ=0
    g23: LineSegment StartX=31.7 StartY=0 StartZ=0 EndX=30.7 EndY=1 EndZ=0
    g24: LineSegment StartX=30.7 StartY=1 StartZ=0 EndX=30.7 EndY=13.4293 EndZ=0
    g25: LineSegment StartX=-30.7 StartY=1 StartZ=0 EndX=30.7 EndY=1 EndZ=0
    g26: LineSegment StartX=-39.3 StartY=1.2 StartZ=0 EndX=-39.3 EndY=2 EndZ=0
    g27: LineSegment StartX=-38.5 StartY=2 StartZ=0 EndX=-39.3 EndY=2 EndZ=0
    g28: LineSegment StartX=39.3 StartY=1.2 StartZ=0 EndX=39.3 EndY=2 EndZ=0
    g29: LineSegment StartX=38.5 StartY=2 StartZ=0 EndX=39.3 EndY=2 EndZ=0
  constraints (75):
    c: PointOnObject(g0,g-1)
    c: Vertical(g0)
    c: Horizontal(g1)
    c: Vertical(g2)
    c: Horizontal(g3)
    c: Vertical(g4)
    c: Horizontal(g5)
    c: PointOnObject(g6,g-1)
    c: Vertical(g6)
    c: Coincident(g7,g0)
    c: PointOnObject(g7,g-1)
    c: Coincident(g8,g6)
    c: Symmetric(g7,g8,g-1)
    c: Tangent(g2,g9) = 1.5708
    c: Tangent(g3,g9) = 1.5708
    c: Tangent(g4,g10) = 1.5708
    c: Tangent(g3,g10) = 1.5708
    c: Tangent(g5,g11) = 1.5708
    c: Tangent(g6,g11) = 1.5708
    c: Tangent(g0,g12) = 1.5708
    c: Tangent(g1,g12) = 1.5708
    c: Tangent(g1,g13) = -1.5708
    c: Tangent(g2,g13) = -1.5708
    c: Tangent(g5,g14) = -1.5708
    c: Tangent(g4,g14) = -1.5708
    c: Coincident(g16,g15)
    c: Horizontal(g16)
    c: Coincident(g17,g16)
    c: Horizontal(g18)
    c: Angle(g18,g15) = 0.785398
    c: Angle(g17,g18) = 0.785398
    c: PointOnObject(g19,g-2)
    c: Symmetric(g15,g16,g20)
    c: Symmetric(g3,g3,g19)
    c: Equal(g9,g10)
    c: Equal(g13,g14)
    c: Radius(g11) = 0.8
    c: Radius(g10) = 0.8
    c: DistanceY(g17,g16) = 1
    c: DistanceY(g6,g5) = 2
    c: DistanceX(g17,g4) = 1.6
    c: DistanceY(g20,g19) = 1.6
    c: Equal(g6,g0)
    c: Equal(g5,g1)
    c: DistanceY(g-1,g20) = 14.4293
    c: Coincident(g18,g17)
    c: Coincident(g15,g18)
    c: Coincident(g21,g15)
    c: Vertical(g21)
    c: Coincident(g22,g7)
    c: Coincident(g22,g21)
    c: Coincident(g23,g8)
    c: Coincident(g24,g23)
    c: Coincident(g24,g17)
    c: Vertical(g24)
    c: Angle(g23,g-1) = 0.785398
    c: Angle(g-1,g22) = 0.785398
    c: DistanceY(g7,g21) = 1
    c: Coincident(g25,g21)
    c: Coincident(g25,g23)
    c: Horizontal(g25)
    c: DistanceX(g21,g23) = 61.4
    c: DistanceX(g4,g6) = 7
    c: Coincident(g26,g0)
    c: Tangent(g26,g12)
    c: Coincident(g27,g1)
    c: Coincident(g27,g26)
    c: Horizontal(g27)
    c: Coincident(g28,g6)
    c: Vertical(g28)
    c: Coincident(g29,g5)
    c: Coincident(g29,g28)
    c: Horizontal(g29)
    c: Radius(g14) = 2
    c: Equal(g9,g12)
FEATURE [PartDesign::AdditiveLoft] AdditiveLoft001  label="MainAngledLoft"
  Closed = false
  Placement = pos=(0,0,0) rot=(1,0,0;1.5708rad)
  Profile = -> Sketch028
  Ruled = false
  Sections = -> [Sketch029]
FEATURE [Sketcher::SketchObject] Sketch030  label="Sketch_Cover_Back_Str"
  FullyConstrained = true
  MapMode = 5
  Placement = pos=(0,23,5.1e-15) rot=(1,0,0;1.5708rad)
  Support = -> [DatumPlane003]
  expr: Constraints[36] = Spreadsheet.coverfront_std_rad
  expr: Constraints[73] = <<params>>.std_rad
  expr: Constraints[37] = Spreadsheet.coverfront_std_rad
  expr: Constraints[62] = Spreadsheet.coverfront_foot_width
  expr: Constraints[39] = Spreadsheet.coverfront_foot_height
  expr: Constraints[57] = <<params>>.std_chamf
  expr: Constraints[44] = Spreadsheet.coverfront_under_height
  expr: Constraints[61] = <<params>>.ardcut_width + (<<params>>.rail_width + Spreadsheet.coverfront_tol) * 2
  expr: Constraints[38] = <<params>>.std_chamf
  expr: Constraints[40] = Spreadsheet.coverfront_wall_thick
  expr: Constraints[41] = Spreadsheet.coverfront_wall_thick
  sketch-geometry (30):
    g0: LineSegment StartX=-39.3 StartY=0 StartZ=0 EndX=-39.3 EndY=1.2 EndZ=0
    g1: LineSegment StartX=-38.5 StartY=2 StartZ=0 EndX=-34.3 EndY=2 EndZ=0
    g2: LineSegment StartX=-32.3 StartY=4 StartZ=0 EndX=-32.3 EndY=15.2293 EndZ=0
    g3: LineSegment StartX=-31.5 StartY=16.0293 StartZ=0 EndX=31.5 EndY=16.0293 EndZ=0
    g4: LineSegment StartX=32.3 StartY=15.2293 StartZ=0 EndX=32.3 EndY=4 EndZ=0
    g5: LineSegment StartX=34.3 StartY=2 StartZ=0 EndX=38.5 EndY=2 EndZ=0
    g6: LineSegment StartX=39.3 StartY=1.2 StartZ=0 EndX=39.3 EndY=0 EndZ=0
    g7: LineSegment StartX=-39.3 StartY=0 StartZ=0 EndX=-31.7 EndY=0 EndZ=0
    g8: LineSegment StartX=31.7 StartY=0 StartZ=0 EndX=39.3 EndY=0 EndZ=0
    g9: ArcOfCircle CenterX=-31.5 CenterY=15.2293 CenterZ=0 NormalX=0 NormalY=0 NormalZ=1 AngleXU=0 Radius=0.8 StartAngle=1.5708 EndAngle=3.14159
    g10: ArcOfCircle CenterX=31.5 CenterY=15.2293 CenterZ=0 NormalX=0 NormalY=0 NormalZ=1 AngleXU=0 Radius=0.8 StartAngle=0 EndAngle=1.5708
    g11: ArcOfCircle CenterX=38.5 CenterY=1.2 CenterZ=0 NormalX=0 NormalY=0 NormalZ=1 AngleXU=0 Radius=0.8 StartAngle=0 EndAngle=1.5708
    g12: ArcOfCircle CenterX=-38.5 CenterY=1.2 CenterZ=0 NormalX=0 NormalY=0 NormalZ=1 AngleXU=0 Radius=0.8 StartAngle=1.5708 EndAngle=3.14159
    g13: ArcOfCircle CenterX=-34.3 CenterY=4 CenterZ=0 NormalX=0 NormalY=0 NormalZ=1 AngleXU=0 Radius=2 StartAngle=4.71239 EndAngle=6.28319
    g14: ArcOfCircle CenterX=34.3 CenterY=4 CenterZ=0 NormalX=0 NormalY=0 NormalZ=1 AngleXU=0 Radius=2 StartAngle=3.14159 EndAngle=4.71239
    g15: LineSegment StartX=-30.7 StartY=13.4293 StartZ=0 EndX=-29.7 EndY=14.4293 EndZ=0
    g16: LineSegment StartX=-29.7 StartY=14.4293 StartZ=0 EndX=29.7 EndY=14.4293 EndZ=0
    g17: LineSegment StartX=29.7 StartY=14.4293 StartZ=0 EndX=30.7 EndY=13.4293 EndZ=0
    g18: LineSegment StartX=-30.7 StartY=13.4293 StartZ=0 EndX=30.7 EndY=13.4293 EndZ=0
    g19: GeomPoint X=0 Y=16.0293 Z=0
    g20: GeomPoint X=5e-16 Y=14.4293 Z=0
    g21: LineSegment StartX=-30.7 StartY=13.4293 StartZ=0 EndX=-30.7 EndY=1 EndZ=0
    g22: LineSegment StartX=-31.7 StartY=0 StartZ=0 EndX=-30.7 EndY=1 EndZ=0
    g23: LineSegment StartX=31.7 StartY=0 StartZ=0 EndX=30.7 EndY=1 EndZ=0
    g24: LineSegment StartX=30.7 StartY=1 StartZ=0 EndX=30.7 EndY=13.4293 EndZ=0
    g25: LineSegment StartX=-30.7 StartY=1 StartZ=0 EndX=30.7 EndY=1 EndZ=0
    g26: LineSegment StartX=-39.3 StartY=1.2 StartZ=0 EndX=-39.3 EndY=2 EndZ=0
    g27: LineSegment StartX=-38.5 StartY=2 StartZ=0 EndX=-39.3 EndY=2 EndZ=0
    g28: LineSegment StartX=39.3 StartY=1.2 StartZ=0 EndX=39.3 EndY=2 EndZ=0
    g29: LineSegment StartX=38.5 StartY=2 StartZ=0 EndX=39.3 EndY=2 EndZ=0
  constraints (75):
    c: PointOnObject(g0,g-1)
    c: Vertical(g0)
    c: Horizontal(g1)
    c: Vertical(g2)
    c: Horizontal(g3)
    c: Vertical(g4)
    c: Horizontal(g5)
    c: PointOnObject(g6,g-1)
    c: Vertical(g6)
    c: Coincident(g7,g0)
    c: PointOnObject(g7,g-1)
    c: Coincident(g8,g6)
    c: Symmetric(g7,g8,g-1)
    c: Tangent(g2,g9) = 1.5708
    c: Tangent(g3,g9) = 1.5708
    c: Tangent(g4,g10) = 1.5708
    c: Tangent(g3,g10) = 1.5708
    c: Tangent(g5,g11) = 1.5708
    c: Tangent(g6,g11) = 1.5708
    c: Tangent(g0,g12) = 1.5708
    c: Tangent(g1,g12) = 1.5708
    c: Tangent(g1,g13) = -1.5708
    c: Tangent(g2,g13) = -1.5708
    c: Tangent(g5,g14) = -1.5708
    c: Tangent(g4,g14) = -1.5708
    c: Coincident(g16,g15)
    c: Horizontal(g16)
    c: Coincident(g17,g16)
    c: Horizontal(g18)
    c: Angle(g18,g15) = 0.785398
    c: Angle(g17,g18) = 0.785398
    c: PointOnObject(g19,g-2)
    c: Symmetric(g15,g16,g20)
    c: Symmetric(g3,g3,g19)
    c: Equal(g9,g10)
    c: Equal(g13,g14)
    c: Radius(g11) = 0.8
    c: Radius(g10) = 0.8
    c: DistanceY(g17,g16) = 1
    c: DistanceY(g6,g5) = 2
    c: DistanceX(g17,g4) = 1.6
    c: DistanceY(g20,g19) = 1.6
    c: Equal(g6,g0)
    c: Equal(g5,g1)
    c: DistanceY(g-1,g20) = 14.4293
    c: Coincident(g18,g17)
    c: Coincident(g15,g18)
    c: Coincident(g21,g15)
    c: Vertical(g21)
    c: Coincident(g22,g7)
    c: Coincident(g22,g21)
    c: Coincident(g23,g8)
    c: Coincident(g24,g23)
    c: Coincident(g24,g17)
    c: Vertical(g24)
    c: Angle(g23,g-1) = 0.785398
    c: Angle(g-1,g22) = 0.785398
    c: DistanceY(g7,g21) = 1
    c: Coincident(g25,g21)
    c: Coincident(g25,g23)
    c: Horizontal(g25)
    c: DistanceX(g21,g23) = 61.4
    c: DistanceX(g4,g6) = 7
    c: Coincident(g26,g0)
    c: Vertical(g26)
    c: Coincident(g27,g1)
    c: Coincident(g27,g26)
    c: Horizontal(g27)
    c: Coincident(g28,g6)
    c: Vertical(g28)
    c: Coincident(g29,g5)
    c: Coincident(g29,g28)
    c: Horizontal(g29)
    c: Radius(g14) = 2
    c: Equal(g12,g9)
FEATURE [PartDesign::Pad] Pad001  label="MainStrExt"
  BaseFeature = -> AdditiveLoft001
  Direction = (1,1,1)
  Length = 4
  Length2 = 100
  Placement = pos=(0,0,0) rot=(1,0,0;1.5708rad)
  Profile = -> Sketch030
  Reversed = true
  Type = 0
  expr: Length = Spreadsheet.coverfront_leng - Spreadsheet.coverfront_angle_leng
FEATURE [Sketcher::SketchObject] Sketch031
  FullyConstrained = true
  MapMode = 5
  Support = -> [XY_Plane002]
  expr: Constraints[54] = <<params>>.coverfront_foot_leng
  expr: Constraints[53] = <<params>>.coverfront_leng
  expr: Constraints[52] = <<params>>.coverfront_foot_width
  expr: Constraints[41] = <<params>>.coverfront_foot_width
  expr: Constraints[39] = <<params>>.std_rad
  expr: Constraints[10] = Spreadsheet.coverfront_outer_wall_width
  sketch-geometry (21):
    g0: LineSegment StartX=-32.3 StartY=0 StartZ=0 EndX=32.3 EndY=0 EndZ=0
    g1: LineSegment StartX=32.3 StartY=0 StartZ=0 EndX=32.3 EndY=12.3431 EndZ=0
    g2: LineSegment StartX=32.8858 StartY=13.7574 StartZ=0 EndX=38.7142 EndY=19.5858 EndZ=0
    g3: LineSegment StartX=46.3 StartY=-10 StartZ=0 EndX=-46.3 EndY=-10 EndZ=0
    g4: LineSegment StartX=-32.3 StartY=0 StartZ=0 EndX=-32.3 EndY=12.3431 EndZ=0
    g5: LineSegment StartX=-32.8858 StartY=13.7574 StartZ=0 EndX=-38.7142 EndY=19.5858 EndZ=0
    g6: LineSegment StartX=-34.3 StartY=12.3431 StartZ=0 EndX=34.3 EndY=12.3431 EndZ=0
    g7: LineSegment StartX=-37.3 StartY=21 StartZ=0 EndX=37.3 EndY=21 EndZ=0
    g8: LineSegment StartX=-39.3 StartY=21 StartZ=0 EndX=-39.3 EndY=27 EndZ=0
    g9: LineSegment StartX=39.3 StartY=21 StartZ=0 EndX=39.3 EndY=27 EndZ=0
    g10: LineSegment StartX=39.3 StartY=27 StartZ=0 EndX=-39.3 EndY=27 EndZ=0
    g11: LineSegment StartX=-39.3 StartY=27 StartZ=0 EndX=-46.3 EndY=27 EndZ=0
    g12: LineSegment StartX=39.3 StartY=27 StartZ=0 EndX=46.3 EndY=27 EndZ=0
    g13: LineSegment StartX=46.3 StartY=27 StartZ=0 EndX=46.3 EndY=-10 EndZ=0
    g14: LineSegment StartX=-46.3 StartY=27 StartZ=0 EndX=-46.3 EndY=-10 EndZ=0
    g15: ArcOfCircle CenterX=34.3 CenterY=12.3431 CenterZ=0 NormalX=0 NormalY=0 NormalZ=1 AngleXU=0 Radius=2 StartAngle=2.35619 EndAngle=3.14159
    g16: ArcOfCircle CenterX=37.3 CenterY=21 CenterZ=0 NormalX=0 NormalY=0 NormalZ=1 AngleXU=0 Radius=2 StartAngle=5.49779 EndAngle=6.28319
    g17: ArcOfCircle CenterX=-37.3 CenterY=21 CenterZ=0 NormalX=0 NormalY=0 NormalZ=1 AngleXU=0 Radius=2 StartAngle=3.14159 EndAngle=3.92699
    g18: ArcOfCircle CenterX=-34.3 CenterY=12.3431 CenterZ=0 NormalX=0 NormalY=0 NormalZ=1 AngleXU=0 Radius=2 StartAngle=0 EndAngle=0.785398
    g19: LineSegment StartX=32.8858 StartY=13.7574 StartZ=0 EndX=46.3 EndY=13.7574 EndZ=0
    g20: LineSegment StartX=-32.8858 StartY=13.7574 StartZ=0 EndX=-46.3 EndY=13.7574 EndZ=0
  constraints (55):
    c: Horizontal(g0)
    c: Coincident(g1,g0)
    c: Vertical(g1)
    c: Horizontal(g3)
    c: Coincident(g4,g0)
    c: Vertical(g4)
    c: Horizontal(g6)
    c: Horizontal(g7)
    c: Symmetric(g0,g0,g-1)
    c: DistanceY(g3,g0) = 10
    c: DistanceX(g0,g0) = 64.6
    c: Vertical(g8)
    c: Vertical(g9)
    c: Coincident(g10,g9)
    c: Coincident(g10,g8)
    c: Horizontal(g10)
    c: Coincident(g11,g8)
    c: Horizontal(g11)
    c: Coincident(g12,g9)
    c: Horizontal(g12)
    c: Coincident(g13,g12)
    c: Vertical(g13)
    c: Coincident(g14,g11)
    c: Vertical(g14)
    c: Coincident(g3,g14)
    c: Coincident(g3,g13)
    c: Equal(g12,g11)
    c: Tangent(g1,g15) = 1.5708
    c: Tangent(g2,g15) = 1.5708
    c: Tangent(g2,g16) = -1.5708
    c: Tangent(g9,g16) = -1.5708
    c: Tangent(g5,g17) = 1.5708
    c: Tangent(g8,g17) = 1.5708
    c: Tangent(g4,g18) = -1.5708
    c: Tangent(g5,g18) = -1.5708
    c: Coincident(g7,g17)
    c: Equal(g15,g16)
    c: Equal(g15,g18)
    c: Equal(g18,g17)
    c: Radius(g16) = 2
    c: Coincident(g7,g16)
    c: DistanceX(g1,g9) = 7
    c: Coincident(g19,g2)
    c: PointOnObject(g19,g13)
    c: Horizontal(g19)
    c: Coincident(g6,g18)
    c: Coincident(g6,g15)
    c: Coincident(g20,g5)
    c: PointOnObject(g20,g14)
    c: Horizontal(g20)
    c: Angle(g5,g20) = 0.785398
    c: Angle(g19,g2) = 0.785398
    c: DistanceX(g9,g12) = 7
    c: DistanceY(g-1,g12) = 27
    c: DistanceY(g9,g9) = 6
FEATURE [PartDesign::Pocket] Pocket005  label="AngledTrimFeet"
  BaseFeature = -> Pad001
  Length = 5
  Length2 = 100
  Placement = pos=(0,0,0) rot=(1,0,0;1.5708rad)
  Profile = -> Sketch031
  Reversed = true
  Type = 1
FEATURE [Sketcher::SketchObject] Sketch032  label="Sketch_FeetMt"
  FullyConstrained = true
  MapMode = 5
  Support = -> [XY_Plane002]
  expr: Constraints[3] = Spreadsheet.coverfront_leng - Spreadsheet.coverfront_hole_offset_leng
  expr: Constraints[4] = Spreadsheet.coverfront_outer_foot_width - 2 * Spreadsheet.coverfront_hole_offset_width
  expr: Constraints[8] = <<params>>.m2_hole_clear_diam
  sketch-geometry (4):
    g0: LineSegment StartX=-35.8 StartY=23 StartZ=0 EndX=35.8 EndY=23 EndZ=0
    g1: GeomPoint X=0 Y=23 Z=0
    g2: Circle CenterX=35.8 CenterY=23 CenterZ=0 NormalX=0 NormalY=0 NormalZ=1 AngleXU=0 Radius=1.2
    g3: Circle CenterX=-35.8 CenterY=23 CenterZ=0 NormalX=0 NormalY=0 NormalZ=1 AngleXU=0 Radius=1.2
  constraints (9):
    c: Horizontal(g0)
    c: PointOnObject(g1,g-2)
    c: Symmetric(g0,g0,g1)
    c: DistanceY(g-1,g1) = 23
    c: DistanceX(g0,g0) = 71.6
    c: Coincident(g2,g0)
    c: Coincident(g3,g0)
    c: Equal(g2,g3)
    c: Diameter(g2) = 2.4
FEATURE [PartDesign::Pocket] Pocket006  label="MtHoles"
  BaseFeature = -> Pocket005
  Length = 5
  Length2 = 100
  Placement = pos=(0,0,0) rot=(1,0,0;1.5708rad)
  Profile = -> Sketch032
  Reversed = true
  Type = 1
FEATURE [Sketcher::SketchObject] Sketch033  label="Sketch_ShieldCover"
  FullyConstrained = true
  MapMode = 5
  Placement = pos=(0,0,0) rot=(1,0,0;1.5708rad)
  Support = -> [XZ_Plane003]
  expr: Constraints[56] = <<params>>.shieldcov_height
  expr: Constraints[49] = <<params>>.shieldcov_thick_top
  expr: Constraints[51] = <<params>>.shieldcov_thick_side
  expr: Constraints[55] = <<params>>.shieldcov_clip_hook_width
  expr: Constraints[57] = <<params>>.shieldcov_width_inner
  expr: Constraints[54] = <<params>>.std_chamf
  expr: Constraints[53] = <<params>>.shieldcov_thick_side / 2
  expr: Constraints[50] = <<params>>.shieldcov_clip_hook_width
  expr: Constraints[46] = <<params>>.std_rad
  sketch-geometry (24):
    g0: LineSegment StartX=-30.7 StartY=11 StartZ=0 EndX=30.7 EndY=11 EndZ=0
    g1: LineSegment StartX=-30.7 StartY=11 StartZ=0 EndX=-30.7 EndY=0 EndZ=0
    g2: LineSegment StartX=30.7 StartY=11 StartZ=0 EndX=30.7 EndY=0 EndZ=0
    g3: LineSegment StartX=-30.7 StartY=0 StartZ=0 EndX=-29.1 EndY=0 EndZ=0
    g4: LineSegment StartX=30.7 StartY=0 StartZ=0 EndX=29.1 EndY=0 EndZ=0
    g5: LineSegment StartX=29.1 StartY=0 StartZ=0 EndX=30.7 EndY=-1.6 EndZ=0
    g6: LineSegment StartX=30.7 StartY=-1.6 StartZ=0 EndX=31.3 EndY=-1.6 EndZ=0
    g7: LineSegment StartX=31.9 StartY=-1 StartZ=0 EndX=31.9 EndY=12 EndZ=0
    g8: LineSegment StartX=-29.1 StartY=0 StartZ=0 EndX=-30.7 EndY=-1.6 EndZ=0
    g9: LineSegment StartX=-30.7 StartY=-1.6 StartZ=0 EndX=-31.3 EndY=-1.6 EndZ=0
    g10: LineSegment StartX=-31.9 StartY=-1 StartZ=0 EndX=-31.9 EndY=12 EndZ=0
    g11: LineSegment StartX=-29.9 StartY=14 StartZ=0 EndX=29.9 EndY=14 EndZ=0
    g12: LineSegment StartX=-30.7 StartY=11 StartZ=0 EndX=-29.7 EndY=12 EndZ=0
    g13: LineSegment StartX=-29.7 StartY=12 StartZ=0 EndX=29.7 EndY=12 EndZ=0
    g14: LineSegment StartX=29.7 StartY=12 StartZ=0 EndX=30.7 EndY=11 EndZ=0
    g15: ArcOfCircle CenterX=-31.3 CenterY=-1 CenterZ=0 NormalX=0 NormalY=0 NormalZ=1 AngleXU=0 Radius=0.6 StartAngle=3.14159 EndAngle=4.71239
    g16: ArcOfCircle CenterX=-29.9 CenterY=12 CenterZ=0 NormalX=0 NormalY=0 NormalZ=1 AngleXU=0 Radius=2 StartAngle=1.5708 EndAngle=3.14159
    g17: ArcOfCircle CenterX=29.9 CenterY=12 CenterZ=0 NormalX=0 NormalY=0 NormalZ=1 AngleXU=0 Radius=2 StartAngle=0 EndAngle=1.5708
    g18: LineSegment StartX=30.7 StartY=0 StartZ=0 EndX=31.9 EndY=0 EndZ=0
    g19: LineSegment StartX=-30.7 StartY=0 StartZ=0 EndX=-31.9 EndY=0 EndZ=0
    g20: ArcOfCircle CenterX=31.3 CenterY=-1 CenterZ=0 NormalX=0 NormalY=0 NormalZ=1 AngleXU=0 Radius=0.6 StartAngle=4.71239 EndAngle=6.28319
    g21: GeomPoint X=-1e-16 Y=12 Z=0
    g22: GeomPoint X=1.7e-15 Y=14 Z=0
    g23: LineSegment StartX=30.7 StartY=-1.6 StartZ=0 EndX=-30.7 EndY=-1.6 EndZ=0
  constraints (61):
    c: Horizontal(g0)
    c: Coincident(g1,g0)
    c: PointOnObject(g1,g-1)
    c: Vertical(g1)
    c: Coincident(g2,g0)
    c: PointOnObject(g2,g-1)
    c: Vertical(g2)
    c: Coincident(g3,g1)
    c: Horizontal(g3)
    c: Coincident(g4,g2)
    c: Coincident(g5,g4)
    c: Coincident(g6,g5)
    c: Horizontal(g6)
    c: Vertical(g7)
    c: Coincident(g8,g3)
    c: Coincident(g9,g8)
    c: Horizontal(g9)
    c: Vertical(g10)
    c: Horizontal(g11)
    c: Coincident(g12,g1)
    c: Coincident(g13,g12)
    c: Horizontal(g13)
    c: Coincident(g14,g13)
    c: Coincident(g14,g2)
    c: Tangent(g9,g15) = 1.5708
    c: Tangent(g10,g15) = 1.5708
    c: Tangent(g11,g16) = 1.5708
    c: Tangent(g10,g16) = 1.5708
    c: Tangent(g7,g17) = -1.5708
    c: Tangent(g11,g17) = 1.5708
    c: Symmetric(g3,g4,g-1)
    c: Equal(g4,g3)
    c: Coincident(g18,g2)
    c: PointOnObject(g18,g7)
    c: Horizontal(g18)
    c: Coincident(g19,g1)
    c: PointOnObject(g19,g10)
    c: Horizontal(g19)
    c: Tangent(g6,g20) = -1.5708
    c: Tangent(g7,g20) = -1.5708
    c: Equal(g20,g15)
    c: Equal(g9,g6)
    c: Equal(g18,g19)
    c: Equal(g12,g14)
    c: Equal(g17,g16)
    c: Angle(g14,g0) = 0.785398
    c: Radius(g17) = 2
    c: Symmetric(g11,g11,g22)
    c: Symmetric(g12,g13,g21)
    c: DistanceY(g21,g22) = 2
    c: DistanceX(g4,g2) = 1.6
    c: DistanceX(g2,g18) = 1.2
    c: Angle(g5,g4) = 0.785398
    c: Radius(g20) = 0.6
    c: DistanceY(g2,g13) = 1
    c: DistanceY(g6,g2) = 1.6
    c: DistanceY(g-1,g21) = 12
    c: DistanceX(g1,g2) = 61.4
    c: Coincident(g23,g5)
    c: Coincident(g23,g8)
    c: Horizontal(g23)
FEATURE [PartDesign::Pad] Pad002  label="MainDoubleExt"
  Direction = (1,1,1)
  Length = 119
  Length2 = 100
  Placement = pos=(0,0,0) rot=(1,0,0;1.5708rad)
  Profile = -> Sketch033
  Reversed = true
  Type = 0
  expr: Length = Spreadsheet.shieldcov_leng_side * 2
FEATURE [Sketcher::SketchObject] Sketch034  label="Sketch_PresSens_Servo_Wedge"
  FullyConstrained = true
  MapMode = 5
  Placement = pos=(0,0,0) rot=(0.57735,0.57735,0.57735;2.0944rad)
  Support = -> [YZ_Plane003]
  expr: Constraints[11] = Spreadsheet.shieldcov_leng_side * 2
  expr: Constraints[10] = <<params>>.shieldcov_pressens_height
  expr: Constraints[9] = <<params>>.shieldcov_height + <<params>>.shieldcov_thick_top
  expr: Constraints[8] = <<params>>.shieldcov_pressens_angle_leng
  sketch-geometry (4):
    g0: LineSegment StartX=0 StartY=14 StartZ=0 EndX=119 EndY=14 EndZ=0
    g1: LineSegment StartX=0 StartY=14 StartZ=0 EndX=44.9555 EndY=16 EndZ=0
    g2: LineSegment StartX=44.9555 StartY=16 StartZ=0 EndX=119 EndY=16 EndZ=0
    g3: LineSegment StartX=119 StartY=16 StartZ=0 EndX=119 EndY=14 EndZ=0
  constraints (12):
    c: PointOnObject(g0,g-2)
    c: Horizontal(g0)
    c: Coincident(g1,g0)
    c: Coincident(g2,g1)
    c: Horizontal(g2)
    c: Coincident(g3,g2)
    c: Coincident(g3,g0)
    c: Vertical(g3)
    c: Distance(g1) = 45
    c: DistanceY(g-1,g0) = 14
    c: DistanceY(g0,g1) = 2
    c: DistanceX(g0,g0) = 119
FEATURE [PartDesign::Pad] Pad003  label="Wedge_PresSens_Servo_Mt"
  BaseFeature = -> Pad002
  Direction = (1,1,1)
  Length = 34
  Length2 = 100
  Midplane = true
  Placement = pos=(0,0,0) rot=(1,0,0;1.5708rad)
  Profile = -> Sketch034
  Type = 0
  expr: Length = <<params>>.shieldcov_pressens_width + 2 * <<params>>.shieldcov_pressens_height
FEATURE [Sketcher::SketchObject] Sketch035
  FullyConstrained = true
  MapMode = 5
  Support = -> [XY_Plane006]
  sketch-geometry (4):
    g0: Circle CenterX=0 CenterY=13.9 CenterZ=0 NormalX=0 NormalY=0 NormalZ=1 AngleXU=0 Radius=1.1
    g1: Circle CenterX=0 CenterY=-13.9 CenterZ=0 NormalX=0 NormalY=0 NormalZ=1 AngleXU=0 Radius=1.1
    g2: GeomPoint X=0 Y=12.8 Z=0
    g3: GeomPoint X=0 Y=-12.8 Z=0
  constraints (9):
    c: PointOnObject(g0,g-2)
    c: Symmetric(g0,g1,g-1)
    c: Equal(g0,g1)
    c: Diameter(g0) = 2.2
    c: PointOnObject(g2,g-2)
    c: PointOnObject(g3,g-2)
    c: PointOnObject(g2,g0)
    c: PointOnObject(g3,g1)
    c: DistanceY(g3,g2) = 25.6
FEATURE [Sketcher::SketchObject] Sketch036
  FullyConstrained = true
  MapMode = 5
  Support = -> [XY_Plane004]
  sketch-geometry (1):
    g0: Circle CenterX=0 CenterY=0 CenterZ=0 NormalX=0 NormalY=0 NormalZ=1 AngleXU=0 Radius=2.9
  constraints (2):
    c: Coincident(g0,g-1)
    c: Diameter(g0) = 5.8
FEATURE [Sketcher::SketchObject] Sketch037
  FullyConstrained = true
  MapMode = 5
  Placement = pos=(0,0,0) rot=(0.57735,0.57735,0.57735;2.0944rad)
  Support = -> [YZ_Plane006]
  sketch-geometry (17):
    g0: LineSegment StartX=-16 StartY=0 StartZ=0 EndX=-16 EndY=1.6 EndZ=0
    g1: LineSegment StartX=-16 StartY=1.6 StartZ=0 EndX=-11.75 EndY=1.6 EndZ=0
    g2: LineSegment StartX=-11.75 StartY=1.6 StartZ=0 EndX=-11.75 EndY=5 EndZ=0
    g3: LineSegment StartX=-11.75 StartY=5 StartZ=0 EndX=11.75 EndY=5 EndZ=0
    g4: LineSegment StartX=11.75 StartY=5 StartZ=0 EndX=11.75 EndY=1.6 EndZ=0
    g5: LineSegment StartX=11.75 StartY=1.6 StartZ=0 EndX=16 EndY=1.6 EndZ=0
    g6: LineSegment StartX=16 StartY=1.6 StartZ=0 EndX=16 EndY=0 EndZ=0
    g7: LineSegment StartX=-16 StartY=0 StartZ=0 EndX=-11.75 EndY=0 EndZ=0
    g8: LineSegment StartX=-11.75 StartY=1.6 StartZ=0 EndX=11.75 EndY=1.6 EndZ=0
    g9: LineSegment StartX=-11.75 StartY=0 StartZ=0 EndX=-11.75 EndY=-13 EndZ=0
    g10: LineSegment StartX=-11.75 StartY=-13 StartZ=0 EndX=-6.25 EndY=-15.3 EndZ=0
    g11: LineSegment StartX=-6.25 StartY=-15.3 StartZ=0 EndX=11.75 EndY=-15.3 EndZ=0
    g12: LineSegment StartX=16 StartY=0 StartZ=0 EndX=11.75 EndY=0 EndZ=0
    g13: LineSegment StartX=11.75 StartY=-15.3 StartZ=0 EndX=11.75 EndY=0 EndZ=0
    g14: LineSegment StartX=-11.75 StartY=0 StartZ=0 EndX=-11.75 EndY=1.6 EndZ=0
    g15: LineSegment StartX=11.75 StartY=0 StartZ=0 EndX=11.75 EndY=1.6 EndZ=0
    g16: LineSegment StartX=0 StartY=0 StartZ=0 EndX=0 EndY=5 EndZ=0
  constraints (47):
    c: PointOnObject(g0,g-1)
    c: Vertical(g0)
    c: Coincident(g1,g0)
    c: Horizontal(g1)
    c: Coincident(g2,g1)
    c: Vertical(g2)
    c: Coincident(g3,g2)
    c: Horizontal(g3)
    c: Coincident(g4,g3)
    c: Vertical(g4)
    c: Coincident(g5,g4)
    c: Horizontal(g5)
    c: Coincident(g6,g5)
    c: PointOnObject(g6,g-1)
    c: Vertical(g6)
    c: Coincident(g7,g0)
    c: PointOnObject(g7,g-1)
    c: Coincident(g8,g1)
    c: Coincident(g8,g4)
    c: Horizontal(g8)
    c: Coincident(g9,g7)
    c: Vertical(g9)
    c: Coincident(g10,g9)
    c: Coincident(g11,g10)
    c: Horizontal(g11)
    c: Coincident(g12,g6)
    c: PointOnObject(g12,g-1)
    c: Coincident(g13,g11)
    c: Coincident(g13,g12)
    c: Vertical(g13)
    c: Coincident(g14,g7)
    c: Coincident(g14,g1)
    c: Coincident(g15,g12)
    c: Coincident(g15,g4)
    c: Vertical(g14)
    c: Vertical(g15)
    c: Coincident(g16,g-1)
    c: PointOnObject(g16,g-2)
    c: Symmetric(g2,g3,g16)
    c: Equal(g1,g5)
    c: DistanceX(g0,g5) = 32
    c: DistanceY(g11,g3) = 20.3
    c: DistanceY(g6,g5) = 1.6
    c: DistanceY(g12,g3) = 5
    c: DistanceX(g2,g3) = 23.5
    c: DistanceY(g9,g2) = 18
    c: DistanceX(g10,g11) = 18
FEATURE [PartDesign::Pad] Pad004  label="Body_MainPad001"
  Direction = (1,1,1)
  Length = 11.6
  Length2 = 100
  Midplane = true
  Placement = pos=(0,0,0) rot=(0.57735,0.57735,0.57735;2.0944rad)
  Profile = -> Sketch037
  Type = 0
FEATURE [Sketcher::SketchObject] Sketch038
  FullyConstrained = true
  MapMode = 5
  Support = -> [XY_Plane004]
  sketch-geometry (6):
    g0: ArcOfCircle CenterX=0 CenterY=0 CenterZ=0 NormalX=0 NormalY=0 NormalZ=1 AngleXU=0 Radius=2.9 StartAngle=1.50358 EndAngle=4.7796
    g1: ArcOfCircle CenterX=13.4 CenterY=0 CenterZ=0 NormalX=0 NormalY=0 NormalZ=1 AngleXU=0 Radius=2 StartAngle=4.7796 EndAngle=7.78677
    g2: LineSegment StartX=0.194784 StartY=2.89345 StartZ=0 EndX=13.5343 EndY=1.99548 EndZ=0
    g3: LineSegment StartX=0.194775 StartY=-2.89345 StartZ=0 EndX=13.5343 EndY=-1.99548 EndZ=0
    g4: GeomPoint X=-2.9 Y=0 Z=0
    g5: GeomPoint X=15.4 Y=0 Z=0
  constraints (17):
    c: Coincident(g0,g-1)
    c: PointOnObject(g1,g-1)
    c: Coincident(g2,g0)
    c: Coincident(g2,g1)
    c: Coincident(g3,g0)
    c: Coincident(g3,g1)
    c: Tangent(g2,g0)
    c: Tangent(g0,g3)
    c: Tangent(g3,g1)
    c: Tangent(g2,g1)
    c: Diameter(g1) = 4
    c: Diameter(g0) = 5.8
    c: PointOnObject(g4,g-1)
    c: PointOnObject(g4,g0)
    c: PointOnObject(g5,g-1)
    c: PointOnObject(g5,g1)
    c: DistanceX(g4,g5) = 18.3
FEATURE [PartDesign::Pad] Pad005
  Direction = (1,1,1)
  Length = 2
  Length2 = 100
  Profile = -> Sketch038
  Type = 0
FEATURE [PartDesign::Pad] Pad006
  BaseFeature = -> Pad005
  Direction = (1,1,1)
  Length = 2.6
  Length2 = 100
  Profile = -> Sketch036
  Reversed = true
  Type = 0
FEATURE [PartDesign::Plane] DatumPlane004  label="DatumTop001"
  AttachmentOffset = pos=(0,0,5) rot=(0,0,1;0rad)
  Length = 60
  MapMode = 5
  Placement = pos=(0,0,5) rot=(0,0,1;0rad)
  ResizeMode = 0
  Support = -> [XY_Plane006]
  Width = 60
FEATURE [Sketcher::SketchObject] Sketch006
  FullyConstrained = true
  MapMode = 5
  Placement = pos=(0,0,5) rot=(0,0,1;0rad)
  Support = -> [DatumPlane004]
  sketch-geometry (6):
    g0: GeomPoint X=0 Y=-11.75 Z=0
    g1: LineSegment StartX=-3.35 StartY=-1.32667 StartZ=0 EndX=-3.35 EndY=-0.0999999 EndZ=0
    g2: LineSegment StartX=3.35 StartY=-1.32667 StartZ=0 EndX=3.35 EndY=-0.1 EndZ=0
    g3: ArcOfCircle CenterX=0 CenterY=-0.1 CenterZ=0 NormalX=0 NormalY=0 NormalZ=1 AngleXU=0 Radius=3.35 StartAngle=6.28319 EndAngle=9.42478
    g4: GeomPoint X=0 Y=3.25 Z=0
    g5: ArcOfCircle CenterX=0 CenterY=-6 CenterZ=0 NormalX=0 NormalY=0 NormalZ=1 AngleXU=0 Radius=5.75 StartAngle=2.19273 EndAngle=7.23205
  constraints (18):
    c: PointOnObject(g0,g-2)
    c: DistanceY(g0,g-1) = 11.75
    c: Vertical(g1)
    c: Vertical(g2)
    c: PointOnObject(g3,g-2)
    c: Coincident(g3,g1)
    c: Coincident(g3,g2)
    c: Tangent(g2,g3)
    c: Tangent(g1,g3)
    c: DistanceX(g1,g2) = 6.7
    c: PointOnObject(g4,g-2)
    c: PointOnObject(g4,g3)
    c: DistanceY(g0,g4) = 15
    c: Coincident(g5,g1)
    c: Coincident(g5,g2)
    c: PointOnObject(g0,g5)
    c: Diameter(g5) = 11.5
    c: PointOnObject(g5,g-2)
FEATURE [PartDesign::Pad] Pad007  label="GearRound001"
  BaseFeature = -> Pad004
  Direction = (1,1,1)
  Length = 3.5
  Length2 = 100
  Placement = pos=(0,0,0) rot=(0.57735,0.57735,0.57735;2.0944rad)
  Profile = -> Sketch006
  Type = 0
FEATURE [PartDesign::Pocket] Pocket014
  BaseFeature = -> Pad007
  Length = 5
  Length2 = 100
  Midplane = true
  Placement = pos=(0,0,0) rot=(0.57735,0.57735,0.57735;2.0944rad)
  Profile = -> Sketch035
  Type = 0
FEATURE [PartDesign::Fillet] Fillet001
  Base = -> Pocket014 [Edge27,Edge17,Edge4,Edge3]
  BaseFeature = -> Pocket014
  Placement = pos=(0,0,0) rot=(0.57735,0.57735,0.57735;2.0944rad)
  Radius = 1
  SupportTransform = false
FEATURE [PartDesign::Body] Body003  label="Servo_Arm001"
  Group = -> [Sketch038,Pad005,Sketch036,Pad006]
  Origin = -> Origin005
  Placement = pos=(0,-7,11) rot=(0,0,-1;1.5708rad)
  Tip = -> Pad006
FEATURE [PartDesign::Body] Body004  label="Servo_Body001"
  Group = -> [Sketch037,Pad004,DatumPlane004,Sketch006,Pad007,Sketch035,Pocket014,Fillet001]
  Origin = -> Origin006
  Tip = -> Fillet001
FEATURE [App::Part] Part001  label="Grove_Servo001"
  Group = -> [Body004,Body003]
  Origin = -> Origin004
  Placement = pos=(1.09e-14,89,22) rot=(0,0,1;3.14159rad)
FEATURE [PartDesign::Plane] DatumPlane005  label="Datum_PresSensWedge"
  AttachmentOffset = pos=(0,0,14) rot=(1,0,0;0.044459rad)
  Length = 80.865
  MapMode = 5
  Placement = pos=(0,0,14) rot=(1,0,0;0.044459rad)
  ResizeMode = 0
  Support = -> [XY_Plane003]
  Width = 131.177
  expr: .AttachmentOffset.Rotation.Roll = <<params>>.shieldcov_pressens_angle
  expr: .AttachmentOffset.Base.z = <<params>>.shieldcov_height + <<params>>.shieldcov_thick_top
FEATURE [Sketcher::SketchObject] Sketch039  label="Sketch_ChamfWedge"
  FullyConstrained = true
  MapMode = 5
  Placement = pos=(0,0,0) rot=(1,0,0;1.5708rad)
  Support = -> [XZ_Plane003]
  expr: Constraints[27] = <<params>>.shieldcov_height + <<params>>.shieldcov_thick_top
  expr: Constraints[26] = <<params>>.shieldcov_pressens_height
  expr: Constraints[25] = <<params>>.shieldcov_height
  expr: Constraints[24] = <<params>>.shieldcov_pressens_width
  expr: Constraints[23] = <<params>>.shieldcov_width_inner + 2 * <<params>>.shieldcov_thick_side
  sketch-geometry (11):
    g0: LineSegment StartX=-17 StartY=14 StartZ=0 EndX=-15 EndY=16 EndZ=0
    g1: LineSegment StartX=-15 StartY=16 StartZ=0 EndX=15 EndY=16 EndZ=0
    g2: LineSegment StartX=15 StartY=16 StartZ=0 EndX=17 EndY=14 EndZ=0
    g3: LineSegment StartX=17 StartY=14 StartZ=0 EndX=31.9 EndY=14 EndZ=0
    g4: LineSegment StartX=31.9 StartY=14 StartZ=0 EndX=31.9 EndY=26 EndZ=0
    g5: LineSegment StartX=31.9 StartY=26 StartZ=0 EndX=-31.9 EndY=26 EndZ=0
    g6: LineSegment StartX=-31.9 StartY=26 StartZ=0 EndX=-31.9 EndY=14 EndZ=0
    g7: LineSegment StartX=-31.9 StartY=14 StartZ=0 EndX=-17 EndY=14 EndZ=0
    g8: LineSegment StartX=-17 StartY=14 StartZ=0 EndX=17 EndY=14 EndZ=0
    g9: GeomPoint X=0 Y=14 Z=0
    g10: GeomPoint X=0 Y=16 Z=0
  constraints (28):
    c: Coincident(g1,g0)
    c: Horizontal(g1)
    c: Coincident(g2,g1)
    c: Coincident(g3,g2)
    c: Horizontal(g3)
    c: Coincident(g4,g3)
    c: Vertical(g4)
    c: Coincident(g5,g4)
    c: Horizontal(g5)
    c: Coincident(g6,g5)
    c: Vertical(g6)
    c: Coincident(g7,g6)
    c: Coincident(g7,g0)
    c: Horizontal(g7)
    c: Coincident(g8,g2)
    c: Horizontal(g8)
    c: PointOnObject(g9,g-2)
    c: PointOnObject(g10,g-2)
    c: Equal(g3,g7)
    c: Angle(g2,g8) = 0.785398
    c: Coincident(g8,g0)
    c: Symmetric(g0,g2,g9)
    c: Symmetric(g0,g1,g10)
    c: DistanceX(g6,g3) = 63.8
    c: DistanceX(g0,g1) = 30
    c: Distance(g4) = 12
    c: DistanceY(g2,g1) = 2
    c: DistanceY(g-1,g9) = 14
FEATURE [PartDesign::Pocket] Pocket015  label="Chamf_PresSensWedge"
  BaseFeature = -> Pad003
  Length = 5
  Length2 = 100
  Placement = pos=(0,0,0) rot=(1,0,0;1.5708rad)
  Profile = -> Sketch039
  Type = 1
FEATURE [Sketcher::SketchObject] Sketch040  label="Sketch_PresSensMtHoles"
  FullyConstrained = true
  MapMode = 5
  Placement = pos=(0,0,14) rot=(1,0,0;0.044459rad)
  Support = -> [DatumPlane005]
  expr: Constraints[22] = <<params>>.m2_hole_clear_diam
  expr: Constraints[16] = <<params>>.shieldcov_pressens_hole_offset
  sketch-geometry (9):
    g0: LineSegment StartX=-10 StartY=43 StartZ=0 EndX=10 EndY=43 EndZ=0
    g1: LineSegment StartX=10 StartY=43 StartZ=0 EndX=10 EndY=3 EndZ=0
    g2: LineSegment StartX=10 StartY=3 StartZ=0 EndX=-10 EndY=3 EndZ=0
    g3: LineSegment StartX=-10 StartY=3 StartZ=0 EndX=-10 EndY=43 EndZ=0
    g4: LineSegment StartX=-10 StartY=33 StartZ=0 EndX=10 EndY=33 EndZ=0
    g5: GeomPoint X=0 Y=3 Z=0
    g6: Circle CenterX=-10 CenterY=33 CenterZ=0 NormalX=0 NormalY=0 NormalZ=1 AngleXU=0 Radius=1.2
    g7: Circle CenterX=10 CenterY=33 CenterZ=0 NormalX=0 NormalY=0 NormalZ=1 AngleXU=0 Radius=1.2
    g8: Circle CenterX=0 CenterY=3 CenterZ=0 NormalX=0 NormalY=0 NormalZ=1 AngleXU=0 Radius=1.2
  constraints (23):
    c: Coincident(g0,g1)
    c: Coincident(g1,g2)
    c: Coincident(g2,g3)
    c: Coincident(g3,g0)
    c: Horizontal(g0)
    c: Horizontal(g2)
    c: Vertical(g1)
    c: Vertical(g3)
    c: PointOnObject(g4,g3)
    c: PointOnObject(g4,g1)
    c: Horizontal(g4)
    c: PointOnObject(g5,g-2)
    c: Symmetric(g2,g1,g5)
    c: DistanceY(g4,g0) = 10
    c: DistanceX(g2,g1) = 20
    c: DistanceY(g2,g0) = 40
    c: DistanceY(g-1,g5) = 3
    c: Coincident(g6,g4)
    c: Coincident(g7,g4)
    c: Coincident(g8,g5)
    c: Equal(g6,g7)
    c: Equal(g7,g8)
    c: Diameter(g8) = 2.4
FEATURE [PartDesign::Pocket] Pocket016  label="PresSens_MtHoles"
  BaseFeature = -> Pocket015
  Length = 5
  Length2 = 100
  Placement = pos=(0,0,0) rot=(1,0,0;1.5708rad)
  Profile = -> Sketch040
  Type = 1
FEATURE [Sketcher::SketchObject] Sketch041  label="Sketch_GroveCableSlot"
  FullyConstrained = true
  MapMode = 5
  Support = -> [XY_Plane003]
  expr: Constraints[22] = <<params>>.shieldcov_pressens_grovecableslot_offset
  sketch-geometry (9):
    g0: LineSegment StartX=0 StartY=49.5 StartZ=0 EndX=-2.5 EndY=47 EndZ=0
    g1: LineSegment StartX=0 StartY=49.5 StartZ=0 EndX=2.5 EndY=47 EndZ=0
    g2: LineSegment StartX=-2.5 StartY=47 StartZ=0 EndX=-2.5 EndY=37 EndZ=0
    g3: LineSegment StartX=2.5 StartY=47 StartZ=0 EndX=2.5 EndY=37 EndZ=0
    g4: LineSegment StartX=-2.5 StartY=37 StartZ=0 EndX=0 EndY=34.5 EndZ=0
    g5: LineSegment StartX=0 StartY=34.5 StartZ=0 EndX=2.5 EndY=37 EndZ=0
    g6: LineSegment StartX=-2.5 StartY=47 StartZ=0 EndX=2.5 EndY=47 EndZ=0
    g7: LineSegment StartX=-2.5 StartY=37 StartZ=0 EndX=2.5 EndY=37 EndZ=0
    g8: GeomPoint X=0 Y=42 Z=0
  constraints (23):
    c: Coincident(g1,g0)
    c: Coincident(g2,g0)
    c: Vertical(g2)
    c: Coincident(g3,g1)
    c: Vertical(g3)
    c: Coincident(g4,g2)
    c: Coincident(g5,g4)
    c: Coincident(g5,g3)
    c: Coincident(g6,g0)
    c: Coincident(g6,g1)
    c: Horizontal(g6)
    c: Coincident(g7,g2)
    c: Coincident(g7,g3)
    c: Horizontal(g7)
    c: PointOnObject(g0,g-2)
    c: PointOnObject(g4,g-2)
    c: Symmetric(g1,g2,g8)
    c: PointOnObject(g8,g-2)
    c: Angle(g0,g1) = 1.5708
    c: Angle(g5,g4) = 1.5708
    c: DistanceY(g3,g1) = 10
    c: DistanceX(g0,g1) = 5
    c: DistanceY(g-1,g8) = 42
FEATURE [PartDesign::Pocket] Pocket017  label="PresSens_GroveCableSlot"
  BaseFeature = -> Pocket016
  Length = 5
  Length2 = 100
  Placement = pos=(0,0,0) rot=(1,0,0;1.5708rad)
  Profile = -> Sketch041
  Reversed = true
  Type = 1
FEATURE [Sketcher::SketchObject] Sketch043  label="Sketch_WedgeTailCut"
  FullyConstrained = true
  MapMode = 5
  Support = -> [XY_Plane003]
  expr: Constraints[35] = <<params>>.shieldcov_leng_side
  expr: Constraints[34] = <<params>>.shieldcov_leng_tot_wtail
  expr: Constraints[33] = <<params>>.shieldcov_servotail_width
  expr: Constraints[31] = <<params>>.shieldcov_width_inner / 2
  expr: Constraints[30] = <<params>>.shieldcov_width_inner
  expr: Constraints[32] = <<params>>.shieldcov_leng_side
  expr: Constraints[26] = <<params>>.std_rad
  sketch-geometry (15):
    g0: LineSegment StartX=-9 StartY=87 StartZ=0 EndX=9 EndY=87 EndZ=0
    g1: LineSegment StartX=10.6275 StartY=86.1624 StartZ=0 EndX=29.0725 EndY=60.3376 EndZ=0
    g2: LineSegment StartX=30.7 StartY=59.5 StartZ=0 EndX=61.4 EndY=59.5 EndZ=0
    g3: LineSegment StartX=-10.6275 StartY=86.1624 StartZ=0 EndX=-29.0725 EndY=60.3376 EndZ=0
    g4: LineSegment StartX=-30.7 StartY=59.5 StartZ=0 EndX=-61.4 EndY=59.5 EndZ=0
    g5: LineSegment StartX=-61.4 StartY=59.5 StartZ=0 EndX=-61.4 EndY=119 EndZ=0
    g6: LineSegment StartX=-61.4 StartY=119 StartZ=0 EndX=61.4 EndY=119 EndZ=0
    g7: LineSegment StartX=61.4 StartY=119 StartZ=0 EndX=61.4 EndY=59.5 EndZ=0
    g8: ArcOfCircle CenterX=-9 CenterY=85 CenterZ=0 NormalX=0 NormalY=0 NormalZ=1 AngleXU=0 Radius=2 StartAngle=1.5708 EndAngle=2.52138
    g9: ArcOfCircle CenterX=9 CenterY=85 CenterZ=0 NormalX=0 NormalY=0 NormalZ=1 AngleXU=0 Radius=2 StartAngle=0.620215 EndAngle=1.5708
    g10: ArcOfCircle CenterX=30.7 CenterY=61.5 CenterZ=0 NormalX=0 NormalY=0 NormalZ=1 AngleXU=0 Radius=2 StartAngle=3.76181 EndAngle=4.71239
    g11: ArcOfCircle CenterX=-30.7 CenterY=61.5 CenterZ=0 NormalX=0 NormalY=0 NormalZ=1 AngleXU=0 Radius=2 StartAngle=4.71239 EndAngle=5.66297
    g12: GeomPoint X=0 Y=87 Z=0
    g13: GeomPoint X=0 Y=59.5 Z=0
    g14: LineSegment StartX=-29.0725 StartY=60.3376 StartZ=0 EndX=29.0725 EndY=60.3376 EndZ=0
  constraints (36):
    c: Horizontal(g0)
    c: Horizontal(g2)
    c: Horizontal(g4)
    c: Coincident(g5,g4)
    c: Vertical(g5)
    c: Coincident(g6,g5)
    c: Horizontal(g6)
    c: Coincident(g7,g6)
    c: Coincident(g7,g2)
    c: Vertical(g7)
    c: Tangent(g3,g8) = -1.5708
    c: Tangent(g0,g8) = 1.5708
    c: Tangent(g0,g9) = 1.5708
    c: Tangent(g1,g9) = 1.5708
    c: Tangent(g1,g10) = -1.5708
    c: Tangent(g2,g10) = -1.5708
    c: Tangent(g3,g11) = 1.5708
    c: Tangent(g4,g11) = 1.5708
    c: PointOnObject(g12,g-2)
    c: PointOnObject(g13,g-2)
    c: Equal(g2,g4)
    c: Symmetric(g4,g2,g13)
    c: Symmetric(g0,g0,g12)
    c: Equal(g10,g9)
    c: Equal(g9,g8)
    c: Equal(g8,g11)
    c: Radius(g9) = 2
    c: Coincident(g14,g3)
    c: Coincident(g14,g1)
    c: Horizontal(g14)
    c: DistanceX(g4,g2) = 61.4
    c: Distance(g2) = 30.7
    c: Distance(g7) = 59.5
    c: DistanceX(g0,g0) = 18
    c: DistanceY(g-1,g0) = 87
    c: DistanceY(g-1,g2) = 59.5
FEATURE [PartDesign::Pocket] Pocket018  label="Servo_WedgeTailCut"
  BaseFeature = -> Pocket017
  Length = 5
  Length2 = 100
  Midplane = true
  Placement = pos=(0,0,0) rot=(1,0,0;1.5708rad)
  Profile = -> Sketch043
  Reversed = true
  Type = 1
FEATURE [Sketcher::SketchObject] Sketch044  label="Sketch_ServoMt"
  FullyConstrained = true
  MapMode = 5
  Support = -> [XY_Plane003]
  expr: Constraints[18] = <<params>>.shieldcov_servomt_slot_offset
  expr: Constraints[19] = <<params>>.shieldcov_servomt_slot_width
  expr: Constraints[17] = <<params>>.m2_hole_clear_diam
  expr: Constraints[16] = <<params>>.shieldcov_leng_side
  expr: Constraints[15] = <<params>>.std_rad / 4
  sketch-geometry (8):
    g0: LineSegment StartX=-6.25 StartY=119 StartZ=0 EndX=6.25 EndY=119 EndZ=0
    g1: LineSegment StartX=6.25 StartY=119 StartZ=0 EndX=6.25 EndY=59.5 EndZ=0
    g2: LineSegment StartX=5.75 StartY=59 StartZ=0 EndX=-5.75 EndY=59 EndZ=0
    g3: LineSegment StartX=-6.25 StartY=59.5 StartZ=0 EndX=-6.25 EndY=119 EndZ=0
    g4: ArcOfCircle CenterX=-5.75 CenterY=59.5 CenterZ=0 NormalX=0 NormalY=0 NormalZ=1 AngleXU=0 Radius=0.5 StartAngle=3.14159 EndAngle=4.71239
    g5: ArcOfCircle CenterX=5.75 CenterY=59.5 CenterZ=0 NormalX=0 NormalY=0 NormalZ=1 AngleXU=0 Radius=0.5 StartAngle=4.71239 EndAngle=6.28319
    g6: Circle CenterX=0 CenterY=57 CenterZ=0 NormalX=0 NormalY=0 NormalZ=1 AngleXU=0 Radius=1.2
    g7: GeomPoint X=0 Y=59 Z=0
  constraints (20):
    c: Coincident(g0,g1)
    c: Coincident(g3,g0)
    c: Horizontal(g0)
    c: Horizontal(g2)
    c: Vertical(g1)
    c: Vertical(g3)
    c: Tangent(g2,g4) = 1.5708
    c: Tangent(g3,g4) = 1.5708
    c: Tangent(g2,g5) = 1.5708
    c: Tangent(g1,g5) = 1.5708
    c: PointOnObject(g6,g-2)
    c: PointOnObject(g7,g-2)
    c: Symmetric(g2,g2,g7)
    c: Equal(g5,g4)
    c: DistanceY(g6,g7) = 2
    c: Radius(g5) = 0.5
    c: Distance(g1) = 59.5
    c: Diameter(g6) = 2.4
    c: DistanceY(g-1,g6) = 57
    c: DistanceX(g3,g1) = 12.5
FEATURE [PartDesign::Pocket] Pocket019  label="Servo_SlotAndMtHole"
  BaseFeature = -> Pocket018
  Length = 5
  Length2 = 100
  Midplane = true
  Placement = pos=(0,0,0) rot=(1,0,0;1.5708rad)
  Profile = -> Sketch044
  Type = 1
FEATURE [PartDesign::Plane] DatumPlane006  label="Datum_SculptServoMt_Start"
  AttachmentOffset = pos=(0,0,-50) rot=(0,0,1;0rad)
  Length = 75.096
  MapMode = 5
  Placement = pos=(0,50,1.11e-14) rot=(1,0,0;1.5708rad)
  ResizeMode = 0
  Support = -> [XZ_Plane003]
  Width = 61.296
  expr: .AttachmentOffset.Base.z = -1 * <<params>>.shieldcov_servomt_sculpt_start
FEATURE [PartDesign::Plane] DatumPlane007  label="Datum_SculptServoMt_End"
  AttachmentOffset = pos=(0,0,-60) rot=(0,0,1;0rad)
  Length = 75.096
  MapMode = 5
  Placement = pos=(0,60,1.33e-14) rot=(1,0,0;1.5708rad)
  ResizeMode = 0
  Support = -> [XZ_Plane003]
  Width = 61.296
  expr: .AttachmentOffset.Base.z = -1 * (<<params>>.shieldcov_servomt_sculpt_start + <<params>>.shieldcov_servomt_sculpt_leng)
FEATURE [Sketcher::SketchObject] Sketch045  label="Sketch_SculptServoMt_Start"
  FullyConstrained = true
  MapMode = 5
  Placement = pos=(0,50,1.11e-14) rot=(1,0,0;1.5708rad)
  Support = -> [DatumPlane006]
  expr: Constraints[23] = <<params>>.shieldcov_width_inner + 2 * <<params>>.shieldcov_thick_side
  expr: Constraints[24] = <<params>>.shieldcov_pressens_width
  expr: Constraints[25] = <<params>>.shieldcov_height
  expr: Constraints[26] = <<params>>.shieldcov_pressens_height
  expr: Constraints[27] = <<params>>.shieldcov_height + <<params>>.shieldcov_thick_top
  sketch-geometry (11):
    g0: LineSegment StartX=-17 StartY=14 StartZ=0 EndX=-15 EndY=16 EndZ=0
    g1: LineSegment StartX=-15 StartY=16 StartZ=0 EndX=15 EndY=16 EndZ=0
    g2: LineSegment StartX=15 StartY=16 StartZ=0 EndX=17 EndY=14 EndZ=0
    g3: LineSegment StartX=17 StartY=14 StartZ=0 EndX=31.9 EndY=14 EndZ=0
    g4: LineSegment StartX=31.9 StartY=14 StartZ=0 EndX=31.9 EndY=26 EndZ=0
    g5: LineSegment StartX=31.9 StartY=26 StartZ=0 EndX=-31.9 EndY=26 EndZ=0
    g6: LineSegment StartX=-31.9 StartY=26 StartZ=0 EndX=-31.9 EndY=14 EndZ=0
    g7: LineSegment StartX=-31.9 StartY=14 StartZ=0 EndX=-17 EndY=14 EndZ=0
    g8: LineSegment StartX=-17 StartY=14 StartZ=0 EndX=17 EndY=14 EndZ=0
    g9: GeomPoint X=0 Y=14 Z=0
    g10: GeomPoint X=0 Y=16 Z=0
  constraints (28):
    c: Coincident(g1,g0)
    c: Horizontal(g1)
    c: Coincident(g2,g1)
    c: Coincident(g3,g2)
    c: Horizontal(g3)
    c: Coincident(g4,g3)
    c: Vertical(g4)
    c: Coincident(g5,g4)
    c: Horizontal(g5)
    c: Coincident(g6,g5)
    c: Vertical(g6)
    c: Coincident(g7,g6)
    c: Coincident(g7,g0)
    c: Horizontal(g7)
    c: Coincident(g8,g2)
    c: Horizontal(g8)
    c: PointOnObject(g9,g-2)
    c: PointOnObject(g10,g-2)
    c: Equal(g3,g7)
    c: Angle(g2,g8) = 0.785398
    c: Coincident(g8,g0)
    c: Symmetric(g0,g2,g9)
    c: Symmetric(g0,g1,g10)
    c: DistanceX(g6,g3) = 63.8
    c: DistanceX(g0,g1) = 30
    c: Distance(g4) = 12
    c: DistanceY(g2,g1) = 2
    c: DistanceY(g-1,g9) = 14
FEATURE [Sketcher::SketchObject] Sketch046  label="Sketch_SculptServoMt_End"
  FullyConstrained = true
  MapMode = 5
  Placement = pos=(0,60,1.33e-14) rot=(1,0,0;1.5708rad)
  Support = -> [DatumPlane007]
  expr: Constraints[27] = <<params>>.shieldcov_servotail_width
  expr: Constraints[26] = <<params>>.shieldcov_height + <<params>>.shieldcov_thick_top
  expr: Constraints[25] = <<params>>.shieldcov_pressens_height
  expr: Constraints[24] = <<params>>.shieldcov_height
  expr: Constraints[23] = <<params>>.shieldcov_width_inner + 2 * <<params>>.shieldcov_thick_side
  sketch-geometry (11):
    g0: LineSegment StartX=-9 StartY=14 StartZ=0 EndX=-7 EndY=16 EndZ=0
    g1: LineSegment StartX=-7 StartY=16 StartZ=0 EndX=7 EndY=16 EndZ=0
    g2: LineSegment StartX=7 StartY=16 StartZ=0 EndX=9 EndY=14 EndZ=0
    g3: LineSegment StartX=9 StartY=14 StartZ=0 EndX=31.9 EndY=14 EndZ=0
    g4: LineSegment StartX=31.9 StartY=14 StartZ=0 EndX=31.9 EndY=26 EndZ=0
    g5: LineSegment StartX=31.9 StartY=26 StartZ=0 EndX=-31.9 EndY=26 EndZ=0
    g6: LineSegment StartX=-31.9 StartY=26 StartZ=0 EndX=-31.9 EndY=14 EndZ=0
    g7: LineSegment StartX=-31.9 StartY=14 StartZ=0 EndX=-9 EndY=14 EndZ=0
    g8: LineSegment StartX=-9 StartY=14 StartZ=0 EndX=9 EndY=14 EndZ=0
    g9: GeomPoint X=0 Y=14 Z=0
    g10: GeomPoint X=0 Y=16 Z=0
  constraints (28):
    c: Coincident(g1,g0)
    c: Horizontal(g1)
    c: Coincident(g2,g1)
    c: Coincident(g3,g2)
    c: Horizontal(g3)
    c: Coincident(g4,g3)
    c: Vertical(g4)
    c: Coincident(g5,g4)
    c: Horizontal(g5)
    c: Coincident(g6,g5)
    c: Vertical(g6)
    c: Coincident(g7,g6)
    c: Coincident(g7,g0)
    c: Horizontal(g7)
    c: Coincident(g8,g2)
    c: Horizontal(g8)
    c: PointOnObject(g9,g-2)
    c: PointOnObject(g10,g-2)
    c: Equal(g3,g7)
    c: Angle(g2,g8) = 0.785398
    c: Coincident(g8,g0)
    c: Symmetric(g0,g2,g9)
    c: Symmetric(g0,g1,g10)
    c: DistanceX(g6,g3) = 63.8
    c: Distance(g4) = 12
    c: DistanceY(g2,g1) = 2
    c: DistanceY(g-1,g9) = 14
    c: DistanceX(g0,g2) = 18
FEATURE [Sketcher::SketchObject] Sketch047  label="Sketch_SculptServoMt_EndExt"
  FullyConstrained = true
  MapMode = 5
  Placement = pos=(0,60,1.33e-14) rot=(1,0,0;1.5708rad)
  Support = -> [DatumPlane007]
  expr: Constraints[23] = <<params>>.shieldcov_width_inner + 2 * <<params>>.shieldcov_thick_side
  expr: Constraints[24] = <<params>>.shieldcov_height
  expr: Constraints[25] = <<params>>.shieldcov_pressens_height
  expr: Constraints[26] = <<params>>.shieldcov_height + <<params>>.shieldcov_thick_top
  expr: Constraints[27] = <<params>>.shieldcov_servotail_width
  sketch-geometry (11):
    g0: LineSegment StartX=-9 StartY=14 StartZ=0 EndX=-7 EndY=16 EndZ=0
    g1: LineSegment StartX=-7 StartY=16 StartZ=0 EndX=7 EndY=16 EndZ=0
    g2: LineSegment StartX=7 StartY=16 StartZ=0 EndX=9 EndY=14 EndZ=0
    g3: LineSegment StartX=9 StartY=14 StartZ=0 EndX=31.9 EndY=14 EndZ=0
    g4: LineSegment StartX=31.9 StartY=14 StartZ=0 EndX=31.9 EndY=26 EndZ=0
    g5: LineSegment StartX=31.9 StartY=26 StartZ=0 EndX=-31.9 EndY=26 EndZ=0
    g6: LineSegment StartX=-31.9 StartY=26 StartZ=0 EndX=-31.9 EndY=14 EndZ=0
    g7: LineSegment StartX=-31.9 StartY=14 StartZ=0 EndX=-9 EndY=14 EndZ=0
    g8: LineSegment StartX=-9 StartY=14 StartZ=0 EndX=9 EndY=14 EndZ=0
    g9: GeomPoint X=0 Y=14 Z=0
    g10: GeomPoint X=0 Y=16 Z=0
  constraints (28):
    c: Coincident(g1,g0)
    c: Horizontal(g1)
    c: Coincident(g2,g1)
    c: Coincident(g3,g2)
    c: Horizontal(g3)
    c: Coincident(g4,g3)
    c: Vertical(g4)
    c: Coincident(g5,g4)
    c: Horizontal(g5)
    c: Coincident(g6,g5)
    c: Vertical(g6)
    c: Coincident(g7,g6)
    c: Coincident(g7,g0)
    c: Horizontal(g7)
    c: Coincident(g8,g2)
    c: Horizontal(g8)
    c: PointOnObject(g9,g-2)
    c: PointOnObject(g10,g-2)
    c: Equal(g3,g7)
    c: Angle(g2,g8) = 0.785398
    c: Coincident(g8,g0)
    c: Symmetric(g0,g2,g9)
    c: Symmetric(g0,g1,g10)
    c: DistanceX(g6,g3) = 63.8
    c: Distance(g4) = 12
    c: DistanceY(g2,g1) = 2
    c: DistanceY(g-1,g9) = 14
    c: DistanceX(g0,g2) = 18
FEATURE [PartDesign::SubtractiveLoft] SubtractiveLoft001  label="SubtractiveLoft_AngledChamf"
  BaseFeature = -> Pocket019
  Closed = false
  Placement = pos=(0,0,0) rot=(1,0,0;1.5708rad)
  Profile = -> Sketch045
  Ruled = false
  Sections = -> [Sketch046]
FEATURE [PartDesign::Pocket] Pocket020  label="Pocket_ServoSlotStraightChamf"
  BaseFeature = -> SubtractiveLoft001
  Length = 5
  Length2 = 100
  Placement = pos=(0,0,0) rot=(1,0,0;1.5708rad)
  Profile = -> Sketch047
  Type = 1
FEATURE [Sketcher::SketchObject] Sketch048  label="Sketch_ServoPlateClear"
  FullyConstrained = true
  MapMode = 5
  Placement = pos=(0,0,0) rot=(0.57735,0.57735,0.57735;2.0944rad)
  Support = -> [YZ_Plane003]
  expr: Constraints[11] = <<params>>.shieldcov_height + <<params>>.shieldcov_thick_top
  expr: Constraints[10] = <<params>>.shieldcov_pressens_height
  expr: Constraints[9] = <<params>>.shieldcov_servoplate_ext_leng + 0.3mm
  expr: Constraints[8] = <<params>>.shieldcov_leng_tot_wtail
  sketch-geometry (4):
    g0: LineSegment StartX=87 StartY=16 StartZ=0 EndX=82.7 EndY=16 EndZ=0
    g1: LineSegment StartX=82.7 StartY=16 StartZ=0 EndX=82.7 EndY=14 EndZ=0
    g2: LineSegment StartX=82.7 StartY=14 StartZ=0 EndX=87 EndY=14 EndZ=0
    g3: LineSegment StartX=87 StartY=14 StartZ=0 EndX=87 EndY=16 EndZ=0
  constraints (12):
    c: Coincident(g0,g1)
    c: Coincident(g1,g2)
    c: Coincident(g2,g3)
    c: Coincident(g3,g0)
    c: Horizontal(g0)
    c: Horizontal(g2)
    c: Vertical(g1)
    c: Vertical(g3)
    c: DistanceX(g-1,g2) = 87
    c: DistanceX(g0,g0) = 4.3
    c: DistanceY(g2,g0) = 2
    c: DistanceY(g-1,g1) = 14
FEATURE [PartDesign::Pocket] Pocket021  label="Pocket_ClearServoMtPlate"
  BaseFeature = -> Pocket020
  Length = 5
  Length2 = 100
  Midplane = true
  Placement = pos=(0,0,0) rot=(1,0,0;1.5708rad)
  Profile = -> Sketch048
  Type = 1
FEATURE [Sketcher::SketchObject] Sketch049  label="Sketch_MainExt"
  FullyConstrained = true
  MapMode = 5
  Placement = pos=(0,0,0) rot=(1,0,0;1.5708rad)
  Support = -> [XZ_Plane007]
  expr: Constraints[23] = <<params>>.shieldcov_servotail_width
  expr: Constraints[22] = <<params>>.shieldcov_servoplate_inner_width
  expr: Constraints[21] = <<params>>.shieldcov_pressens_height
  expr: Constraints[20] = <<params>>.shieldcov_thick_top
  sketch-geometry (10):
    g0: LineSegment StartX=-6 StartY=0 StartZ=0 EndX=6 EndY=0 EndZ=0
    g1: LineSegment StartX=6 StartY=0 StartZ=0 EndX=6 EndY=2 EndZ=0
    g2: LineSegment StartX=6 StartY=2 StartZ=0 EndX=9 EndY=2 EndZ=0
    g3: LineSegment StartX=-6 StartY=0 StartZ=0 EndX=-6 EndY=2 EndZ=0
    g4: LineSegment StartX=-6 StartY=2 StartZ=0 EndX=-9 EndY=2 EndZ=0
    g5: LineSegment StartX=-9 StartY=2 StartZ=0 EndX=-7 EndY=4 EndZ=0
    g6: LineSegment StartX=-7 StartY=4 StartZ=0 EndX=7 EndY=4 EndZ=0
    g7: LineSegment StartX=7 StartY=4 StartZ=0 EndX=9 EndY=2 EndZ=0
    g8: LineSegment StartX=-6 StartY=2 StartZ=0 EndX=6 EndY=2 EndZ=0
    g9: GeomPoint X=0 Y=4 Z=0
  constraints (26):
    c: Horizontal(g0)
    c: Coincident(g1,g0)
    c: Vertical(g1)
    c: Coincident(g2,g1)
    c: Horizontal(g2)
    c: Coincident(g3,g0)
    c: Vertical(g3)
    c: Coincident(g4,g3)
    c: Horizontal(g4)
    c: Coincident(g5,g4)
    c: Coincident(g6,g5)
    c: Horizontal(g6)
    c: Coincident(g7,g6)
    c: Coincident(g7,g2)
    c: Coincident(g8,g3)
    c: Coincident(g8,g1)
    c: Horizontal(g8)
    c: Symmetric(g0,g0,g-1)
    c: Angle(g7,g2) = 0.785398
    c: Angle(g4,g5) = 0.785398
    c: DistanceY(g0,g1) = 2
    c: DistanceY(g1,g6) = 2
    c: DistanceX(g0,g0) = 12
    c: DistanceX(g4,g2) = 18
    c: PointOnObject(g9,g-2)
    c: Symmetric(g5,g6,g9)
FEATURE [PartDesign::Pad] Pad008  label="MainExt"
  Direction = (1,1,1)
  Length = 4
  Length2 = 100
  Midplane = true
  Placement = pos=(0,0,0) rot=(1,0,0;1.5708rad)
  Profile = -> Sketch049
  Type = 0
  expr: Length = <<params>>.shieldcov_servoplate_ext_leng
FEATURE [Sketcher::SketchObject] Sketch050
  FullyConstrained = true
  MapMode = 5
  Support = -> [XY_Plane007]
  expr: Constraints[1] = <<params>>.m2_hole_clear_diam - 0.1mm
  sketch-geometry (1):
    g0: Circle CenterX=0 CenterY=0 CenterZ=0 NormalX=0 NormalY=0 NormalZ=1 AngleXU=0 Radius=1.15
  constraints (2):
    c: Coincident(g0,g-1)
    c: Diameter(g0) = 2.3
FEATURE [PartDesign::Pocket] Pocket022  label="MtHole"
  BaseFeature = -> Pad008
  Length = 5
  Length2 = 100
  Placement = pos=(0,0,0) rot=(1,0,0;1.5708rad)
  Profile = -> Sketch050
  Reversed = true
  Type = 1
FEATURE [PartDesign::Body] Body005  label="PB3D_Triplate_Top_ServoPlate"
  Group = -> [Sketch049,Pad008,Sketch050,Pocket022]
  Origin = -> Origin007
  Placement = pos=(0,103,17) rot=(0,0,1;0rad)
  Tip = -> Pocket022
FEATURE [Sketcher::SketchObject] Sketch051  label="Sketch_TrimSideClips"
  FullyConstrained = true
  MapMode = 5
  Placement = pos=(0,0,0) rot=(0.57735,0.57735,0.57735;2.0944rad)
  Support = -> [YZ_Plane003]
  expr: Constraints[39] = <<params>>.shieldcov_clip_leng
  expr: Constraints[38] = <<params>>.shieldcov_clip_leng
  expr: Constraints[29] = <<params>>.shieldcov_clip_cut_height
  expr: Constraints[31] = <<params>>.shieldcov_leng_side
  expr: Constraints[21] = <<params>>.shieldcov_clip_hook_width
  expr: Constraints[23] = <<params>>.shieldcov_clip_cut_height
  expr: Constraints[22] = <<params>>.shieldcov_height
  sketch-geometry (15):
    g0: LineSegment StartX=0 StartY=-1.6 StartZ=0 EndX=10.4 EndY=-1.6 EndZ=0
    g1: LineSegment StartX=10.4 StartY=-1.6 StartZ=0 EndX=14.4 EndY=2.4 EndZ=0
    g2: LineSegment StartX=14.4 StartY=2.4 StartZ=0 EndX=42.7 EndY=2.4 EndZ=0
    g3: LineSegment StartX=42.7 StartY=2.4 StartZ=0 EndX=46.7 EndY=-1.6 EndZ=0
    g4: LineSegment StartX=46.7 StartY=-1.6 StartZ=0 EndX=55.5 EndY=-1.6 EndZ=0
    g5: LineSegment StartX=55.5 StartY=-1.6 StartZ=0 EndX=59.5 EndY=2.4 EndZ=0
    g6: LineSegment StartX=63.5 StartY=-13.6 StartZ=0 EndX=0 EndY=-13.6 EndZ=0
    g7: LineSegment StartX=0 StartY=-13.6 StartZ=0 EndX=0 EndY=-1.6 EndZ=0
    g8: LineSegment StartX=10.4 StartY=-1.6 StartZ=0 EndX=46.7 EndY=-1.6 EndZ=0
    g9: LineSegment StartX=42.7 StartY=2.4 StartZ=0 EndX=59.5 EndY=2.4 EndZ=0
    g10: LineSegment StartX=59.5 StartY=2.4 StartZ=0 EndX=63.5 EndY=2.4 EndZ=0
    g11: LineSegment StartX=63.5 StartY=2.4 StartZ=0 EndX=63.5 EndY=-13.6 EndZ=0
    g12: GeomPoint X=12 Y=0 Z=0
    g13: GeomPoint X=45.1 Y=0 Z=0
    g14: GeomPoint X=57.1 Y=0 Z=0
  constraints (40):
    c: PointOnObject(g0,g-2)
    c: Horizontal(g0)
    c: Coincident(g1,g0)
    c: Coincident(g2,g1)
    c: Horizontal(g2)
    c: Coincident(g3,g2)
    c: Coincident(g4,g3)
    c: Horizontal(g4)
    c: Coincident(g5,g4)
    c: PointOnObject(g6,g-2)
    c: Horizontal(g6)
    c: Coincident(g7,g6)
    c: Coincident(g7,g0)
    c: Coincident(g8,g0)
    c: Coincident(g8,g3)
    c: Horizontal(g8)
    c: Angle(g8,g1) = 0.785398
    c: Angle(g3,g8) = 0.785398
    c: Coincident(g9,g2)
    c: Coincident(g9,g5)
    c: Horizontal(g9)
    c: DistanceY(g0,g-1) = 1.6
    c: DistanceY(g6,g0) = 12
    c: DistanceY(g4,g5) = 4
    c: Coincident(g10,g5)
    c: Horizontal(g10)
    c: Coincident(g11,g10)
    c: Vertical(g11)
    c: Coincident(g6,g11)
    c: Distance(g10) = 4
    c: Angle(g9,g5) = 0.785398
    c: DistanceX(g-1,g5) = 59.5
    c: PointOnObject(g12,g1)
    c: PointOnObject(g12,g-1)
    c: PointOnObject(g13,g-1)
    c: PointOnObject(g14,g-1)
    c: PointOnObject(g13,g3)
    c: PointOnObject(g14,g5)
    c: DistanceX(g13,g14) = 12
    c: DistanceX(g-1,g12) = 12
FEATURE [PartDesign::Pocket] Pocket023  label="TrimSideClips"
  BaseFeature = -> Pocket021
  Length = 5
  Length2 = 100
  Midplane = true
  Placement = pos=(0,0,0) rot=(1,0,0;1.5708rad)
  Profile = -> Sketch051
  Type = 1
FEATURE [Sketcher::SketchObject] Sketch052
  FullyConstrained = true
  MapMode = 5
  Support = -> [XY_Plane003]
  expr: Constraints[61] = <<params>>.shieldcov_clip_leng
  expr: Constraints[60] = <<params>>.shieldcov_clip_leng
  expr: Constraints[63] = <<params>>.shieldcov_clip_loc_back
  expr: Constraints[58] = <<params>>.shieldcov_width_inner
  expr: Constraints[55] = <<params>>.shieldcov_clip_hook_width
  expr: Constraints[59] = <<params>>.shieldcov_clip_leng
  sketch-geometry (25):
    g0: LineSegment StartX=-29.1 StartY=10.4 StartZ=0 EndX=29.1 EndY=10.4 EndZ=0
    g1: LineSegment StartX=29.1 StartY=10.4 StartZ=0 EndX=30.7 EndY=12 EndZ=0
    g2: LineSegment StartX=30.7 StartY=12 StartZ=0 EndX=30.7 EndY=45.1 EndZ=0
    g3: LineSegment StartX=30.7 StartY=45.1 StartZ=0 EndX=29.1 EndY=46.7 EndZ=0
    g4: LineSegment StartX=29.1 StartY=46.7 StartZ=0 EndX=29.1 EndY=55.5 EndZ=0
    g5: LineSegment StartX=29.1 StartY=55.5 StartZ=0 EndX=30.7 EndY=57.1 EndZ=0
    g6: LineSegment StartX=30.7 StartY=57.1 StartZ=0 EndX=30.7 EndY=69.1 EndZ=0
    g7: LineSegment StartX=30.7 StartY=69.1 StartZ=0 EndX=-30.7 EndY=69.1 EndZ=0
    g8: LineSegment StartX=-29.1 StartY=10.4 StartZ=0 EndX=-30.7 EndY=12 EndZ=0
    g9: LineSegment StartX=-30.7 StartY=12 StartZ=0 EndX=-30.7 EndY=45.1 EndZ=0
    g10: LineSegment StartX=-30.7 StartY=45.1 StartZ=0 EndX=-29.1 EndY=46.7 EndZ=0
    g11: LineSegment StartX=-29.1 StartY=46.7 StartZ=0 EndX=-29.1 EndY=55.5 EndZ=0
    g12: LineSegment StartX=-29.1 StartY=55.5 StartZ=0 EndX=-30.7 EndY=57.1 EndZ=0
    g13: LineSegment StartX=-30.7 StartY=57.1 StartZ=0 EndX=-30.7 EndY=69.1 EndZ=0
    g14: LineSegment StartX=-30.7 StartY=57.1 StartZ=0 EndX=-30.7 EndY=45.1 EndZ=0
    g15: LineSegment StartX=-29.1 StartY=46.7 StartZ=0 EndX=-29.1 EndY=10.4 EndZ=0
    g16: LineSegment StartX=30.7 StartY=45.1 StartZ=0 EndX=30.7 EndY=57.1 EndZ=0
    g17: LineSegment StartX=29.1 StartY=55.5 StartZ=0 EndX=29.1 EndY=69.1 EndZ=0
    g18: LineSegment StartX=-29.1 StartY=55.5 StartZ=0 EndX=-29.1 EndY=69.1 EndZ=0
    g19: LineSegment StartX=29.1 StartY=46.7 StartZ=0 EndX=29.1 EndY=10.4 EndZ=0
    g20: LineSegment StartX=-29.1 StartY=46.7 StartZ=0 EndX=29.1 EndY=46.7 EndZ=0
    g21: LineSegment StartX=-29.1 StartY=55.5 StartZ=0 EndX=29.1 EndY=55.5 EndZ=0
    g22: LineSegment StartX=-30.7 StartY=12 StartZ=0 EndX=30.7 EndY=12 EndZ=0
    g23: GeomPoint X=0 Y=10.4 Z=0
    g24: GeomPoint X=30.7 Y=51.1 Z=0
  constraints (64):
    c: Horizontal(g0)
    c: Coincident(g1,g0)
    c: Coincident(g2,g1)
    c: Vertical(g2)
    c: Coincident(g3,g2)
    c: Coincident(g4,g3)
    c: Vertical(g4)
    c: Coincident(g5,g4)
    c: Coincident(g6,g5)
    c: Vertical(g6)
    c: Coincident(g7,g6)
    c: Horizontal(g7)
    c: Coincident(g8,g0)
    c: Coincident(g9,g8)
    c: Vertical(g9)
    c: Coincident(g10,g9)
    c: Coincident(g11,g10)
    c: Vertical(g11)
    c: Coincident(g12,g11)
    c: Coincident(g13,g12)
    c: Vertical(g13)
    c: Coincident(g7,g13)
    c: Coincident(g14,g12)
    c: Coincident(g14,g9)
    c: Vertical(g14)
    c: Coincident(g15,g10)
    c: Coincident(g15,g0)
    c: Vertical(g15)
    c: Coincident(g16,g2)
    c: Coincident(g16,g5)
    c: Vertical(g16)
    c: Coincident(g17,g4)
    c: PointOnObject(g17,g7)
    c: Vertical(g17)
    c: Coincident(g18,g11)
    c: PointOnObject(g18,g7)
    c: Vertical(g18)
    c: Coincident(g19,g3)
    c: Coincident(g19,g0)
    c: Vertical(g19)
    c: Angle(g15,g8) = 0.785398
    c: Angle(g1,g19) = 0.785398
    c: Angle(g19,g3) = 0.785398
    c: Angle(g10,g15) = 0.785398
    c: Angle(g5,g17) = 0.785398
    c: Angle(g18,g12) = 0.785398
    c: Coincident(g20,g10)
    c: Coincident(g20,g3)
    c: Coincident(g21,g11)
    c: Coincident(g21,g4)
    c: Coincident(g22,g8)
    c: Coincident(g22,g1)
    c: Horizontal(g22)
    c: Horizontal(g21)
    c: Horizontal(g20)
    c: DistanceX(g0,g1) = 1.6
    c: PointOnObject(g23,g-2)
    c: Symmetric(g0,g0,g23)
    c: DistanceX(g8,g1) = 61.4
    c: Distance(g6) = 12
    c: DistanceY(g-1,g1) = 12
    c: DistanceY(g2,g5) = 12
    c: Symmetric(g5,g2,g24)
    c: DistanceY(g-1,g24) = 51.1
FEATURE [PartDesign::Pocket] Pocket024  label="CutClipsForPrinting"
  BaseFeature = -> Pocket023
  Length = 5
  Length2 = 100
  Placement = pos=(0,0,0) rot=(1,0,0;1.5708rad)
  Profile = -> Sketch052
  Type = 1
FEATURE [PartDesign::Body] Body002  label="PB3D_Triplate_Top_ShieldCover"
  Group = -> [Sketch033,Pad002,Sketch034,Pad003,DatumPlane005,Sketch039,Pocket015,Sketch040,Pocket016,Sketch041,Pocket017,Sketch043,Pocket018,Sketch044,Pocket019,DatumPlane007,Sketch045,DatumPlane006,Sketch046,Sketch047,SubtractiveLoft001,Pocket020,Sketch048,Pocket021,Sketch051,Pocket023,Sketch052,Pocket024]
  Origin = -> Origin003
  Placement = pos=(0,18,5) rot=(0,0,1;0rad)
  Tip = -> Pocket024
FEATURE [Sketcher::SketchObject] Sketch053  label="Sketch_ClipMounts"
  FullyConstrained = true
  MapMode = 5
  Placement = pos=(0,0,3) rot=(0,0,1;0rad)
  Support = -> [DatumPlane]
  expr: Constraints[60] = <<params>>.shieldcov_clip_leng + 2 * <<params>>.shieldcov_tol
  expr: Constraints[61] = <<params>>.rail_width
  expr: Constraints[62] = <<params>>.ardcut_width + 2 * (<<params>>.rail_width - <<params>>.rail_clip_mt_width)
  expr: Constraints[64] = Spreadsheet.rail_clip_mt_loc_front
  expr: Constraints[66] = <<params>>.rail_clip_mt_loc_back
  sketch-geometry (27):
    g0: LineSegment StartX=31.5 StartY=30.2 StartZ=0 EndX=28.5 EndY=30.2 EndZ=0
    g1: LineSegment StartX=28.5 StartY=30.2 StartZ=0 EndX=28.5 EndY=17.8 EndZ=0
    g2: LineSegment StartX=28.5 StartY=17.8 StartZ=0 EndX=31.5 EndY=17.8 EndZ=0
    g3: LineSegment StartX=31.5 StartY=17.8 StartZ=0 EndX=31.5 EndY=30.2 EndZ=0
    g4: LineSegment StartX=-31.5 StartY=30.2 StartZ=0 EndX=-28.5 EndY=30.2 EndZ=0
    g5: LineSegment StartX=-28.5 StartY=30.2 StartZ=0 EndX=-28.5 EndY=17.8 EndZ=0
    g6: LineSegment StartX=-28.5 StartY=17.8 StartZ=0 EndX=-31.5 EndY=17.8 EndZ=0
    g7: LineSegment StartX=-31.5 StartY=17.8 StartZ=0 EndX=-31.5 EndY=30.2 EndZ=0
    g8: LineSegment StartX=31.5 StartY=75.3 StartZ=0 EndX=28.5 EndY=75.3 EndZ=0
    g9: LineSegment StartX=28.5 StartY=75.3 StartZ=0 EndX=28.5 EndY=62.9 EndZ=0
    g10: LineSegment StartX=28.5 StartY=62.9 StartZ=0 EndX=31.5 EndY=62.9 EndZ=0
    g11: LineSegment StartX=31.5 StartY=62.9 StartZ=0 EndX=31.5 EndY=75.3 EndZ=0
    g12: LineSegment StartX=-31.5 StartY=75.3 StartZ=0 EndX=-28.5 EndY=75.3 EndZ=0
    g13: LineSegment StartX=-28.5 StartY=75.3 StartZ=0 EndX=-28.5 EndY=62.9 EndZ=0
    g14: LineSegment StartX=-28.5 StartY=62.9 StartZ=0 EndX=-31.5 EndY=62.9 EndZ=0
    g15: LineSegment StartX=-31.5 StartY=62.9 StartZ=0 EndX=-31.5 EndY=75.3 EndZ=0
    g16: LineSegment StartX=-28.5 StartY=62.9 StartZ=0 EndX=28.5 EndY=62.9 EndZ=0
    g17: LineSegment StartX=28.5 StartY=62.9 StartZ=0 EndX=28.5 EndY=30.2 EndZ=0
    g18: LineSegment StartX=31.5 StartY=62.9 StartZ=0 EndX=31.5 EndY=30.2 EndZ=0
    g19: LineSegment StartX=28.5 StartY=30.2 StartZ=0 EndX=-28.5 EndY=30.2 EndZ=0
    g20: LineSegment StartX=-28.5 StartY=17.8 StartZ=0 EndX=28.5 EndY=17.8 EndZ=0
    g21: LineSegment StartX=28.5 StartY=75.3 StartZ=0 EndX=-28.5 EndY=75.3 EndZ=0
    g22: LineSegment StartX=-28.5 StartY=62.9 StartZ=0 EndX=-28.5 EndY=30.2 EndZ=0
    g23: LineSegment StartX=-31.5 StartY=30.2 StartZ=0 EndX=-31.5 EndY=62.9 EndZ=0
    g24: GeomPoint X=0 Y=17.8 Z=0
    g25: GeomPoint X=31.5 Y=24 Z=0
    g26: GeomPoint X=31.5 Y=69.1 Z=0
  constraints (67):
    c: Coincident(g0,g1)
    c: Coincident(g1,g2)
    c: Coincident(g2,g3)
    c: Coincident(g3,g0)
    c: Horizontal(g0)
    c: Horizontal(g2)
    c: Vertical(g1)
    c: Vertical(g3)
    c: Coincident(g4,g5)
    c: Coincident(g5,g6)
    c: Coincident(g6,g7)
    c: Coincident(g7,g4)
    c: Horizontal(g4)
    c: Horizontal(g6)
    c: Vertical(g5)
    c: Vertical(g7)
    c: Coincident(g8,g9)
    c: Coincident(g9,g10)
    c: Coincident(g10,g11)
    c: Coincident(g11,g8)
    c: Horizontal(g8)
    c: Horizontal(g10)
    c: Vertical(g9)
    c: Vertical(g11)
    c: Coincident(g12,g13)
    c: Coincident(g13,g14)
    c: Coincident(g14,g15)
    c: Coincident(g15,g12)
    c: Horizontal(g12)
    c: Horizontal(g14)
    c: Vertical(g13)
    c: Vertical(g15)
    c: Coincident(g16,g13)
    c: Coincident(g16,g9)
    c: Horizontal(g16)
    c: Coincident(g17,g9)
    c: Coincident(g17,g0)
    c: Vertical(g17)
    c: Coincident(g18,g10)
    c: Coincident(g18,g0)
    c: Vertical(g18)
    c: Coincident(g19,g0)
    c: Coincident(g19,g4)
    c: Horizontal(g19)
    c: Coincident(g20,g5)
    c: Coincident(g20,g1)
    c: Horizontal(g20)
    c: Coincident(g21,g8)
    c: Coincident(g21,g12)
    c: Horizontal(g21)
    c: Coincident(g22,g13)
    c: Coincident(g22,g4)
    c: Coincident(g23,g4)
    c: Coincident(g23,g14)
    c: Vertical(g22)
    c: Vertical(g23)
    c: PointOnObject(g24,g-2)
    c: Symmetric(g5,g1,g24)
    c: Equal(g8,g12)
    c: Equal(g9,g5)
    c: DistanceY(g1,g0) = 12.4
    c: DistanceX(g1,g2) = 3
    c: DistanceX(g5,g1) = 57
    c: Symmetric(g2,g0,g25)
    c: DistanceY(g-1,g25) = 24
    c: Symmetric(g10,g8,g26)
    c: DistanceY(g-1,g26) = 69.1
FEATURE [PartDesign::Pocket] Pocket025  label="ClipMountSlots"
  BaseFeature = -> Pocket004
  Length = 2.75
  Length2 = 100
  Profile = -> Sketch053
  Reversed = true
  Type = 0
  expr: Length = <<params>>.rail_clip_mt_height
FEATURE [PartDesign::Plane] DatumPlane008  label="Datum_AngSpeakerMt"
  AttachmentOffset = pos=(0,0,3.8) rot=(1,0,0;0.488692rad)
  Length = 93.37
  MapMode = 5
  Placement = pos=(0,0,3.8) rot=(1,0,0;0.488692rad)
  ResizeMode = 0
  Support = -> [XY_Plane002]
  Width = 84.1568
  expr: .AttachmentOffset.Rotation.Roll = <<params>>.rail_front_angle
  expr: .AttachmentOffset.Base.z = <<params>>.front_vert_edge + <<params>>.coverfront_tol + <<params>>.coverfront_wall_thick
FEATURE [Sketcher::SketchObject] Sketch054  label="Sketch_SpeakerMtHoles"
  FullyConstrained = true
  MapMode = 5
  Placement = pos=(0,-2e-16,3.8) rot=(1,0,0;0.488692rad)
  Support = -> [DatumPlane008]
  expr: Constraints[15] = <<params>>.frontcover_speaker_mt_offset
  expr: Constraints[22] = <<params>>.m2_hole_clear_diam
  sketch-geometry (22):
    g0: LineSegment StartX=-20 StartY=23 StartZ=0 EndX=20 EndY=23 EndZ=0
    g1: LineSegment StartX=20 StartY=23 StartZ=0 EndX=20 EndY=3 EndZ=0
    g2: LineSegment StartX=20 StartY=3 StartZ=0 EndX=-20 EndY=3 EndZ=0
    g3: LineSegment StartX=-20 StartY=3 StartZ=0 EndX=-20 EndY=23 EndZ=0
    g4: GeomPoint X=0 Y=3 Z=0
    g5: LineSegment StartX=10 StartY=23 StartZ=0 EndX=10 EndY=3 EndZ=0
    g6: Circle CenterX=-20 CenterY=13 CenterZ=0 NormalX=0 NormalY=0 NormalZ=1 AngleXU=0 Radius=1.2
    g7: Circle CenterX=10 CenterY=3 CenterZ=0 NormalX=0 NormalY=0 NormalZ=1 AngleXU=0 Radius=1.2
    g8: Circle CenterX=10 CenterY=23 CenterZ=0 NormalX=0 NormalY=0 NormalZ=1 AngleXU=0 Radius=1.2
    g9: LineSegment StartX=18 StartY=18 StartZ=0 EndX=20.25 EndY=20.25 EndZ=0
    g10: GeomPoint X=20 Y=13 Z=0
    g11: LineSegment StartX=20.25 StartY=20.25 StartZ=0 EndX=22.5 EndY=18 EndZ=0
    g12: LineSegment StartX=18 StartY=18 StartZ=0 EndX=18 EndY=8 EndZ=0
    g13: LineSegment StartX=22.5 StartY=18 StartZ=0 EndX=22.5 EndY=8 EndZ=0
    g14: LineSegment StartX=18 StartY=8 StartZ=0 EndX=20.25 EndY=5.75 EndZ=0
    g15: LineSegment StartX=20.25 StartY=5.75 StartZ=0 EndX=22.5 EndY=8 EndZ=0
    g16: LineSegment StartX=18 StartY=18 StartZ=0 EndX=22.5 EndY=18 EndZ=0
    g17: LineSegment StartX=18 StartY=8 StartZ=0 EndX=22.5 EndY=8 EndZ=0
    g18: GeomPoint X=18 Y=13 Z=0
    g19: LineSegment StartX=20.25 StartY=20.25 StartZ=0 EndX=20.25 EndY=5.75 EndZ=0
    g20: GeomPoint X=20.25 Y=18 Z=0
    g21: LineSegment StartX=18 StartY=13 StartZ=0 EndX=20 EndY=13 EndZ=0
  constraints (52):
    c: Coincident(g0,g1)
    c: Coincident(g1,g2)
    c: Coincident(g2,g3)
    c: Coincident(g3,g0)
    c: Horizontal(g0)
    c: Horizontal(g2)
    c: Vertical(g1)
    c: Vertical(g3)
    c: PointOnObject(g4,g-2)
    c: Symmetric(g2,g1,g4)
    c: PointOnObject(g5,g0)
    c: PointOnObject(g5,g2)
    c: Vertical(g5)
    c: DistanceX(g4,g5) = 10
    c: DistanceX(g0,g0) = 40
    c: DistanceY(g-1,g4) = 3
    c: DistanceY(g1,g0) = 20
    c: Coincident(g7,g5)
    c: Coincident(g8,g5)
    c: Equal(g8,g7)
    c: Equal(g7,g6)
    c: Symmetric(g2,g0,g6)
    c: Diameter(g8) = 2.4
    c: Symmetric(g0,g1,g10)
    c: Coincident(g11,g9)
    c: Coincident(g12,g9)
    c: Vertical(g12)
    c: Coincident(g13,g11)
    c: Vertical(g13)
    c: Coincident(g14,g12)
    c: Coincident(g15,g14)
    c: Coincident(g15,g13)
    c: Coincident(g16,g9)
    c: Coincident(g16,g11)
    c: Horizontal(g16)
    c: Coincident(g17,g12)
    c: Coincident(g17,g13)
    c: Horizontal(g17)
    c: Angle(g9,g11) = 1.5708
    c: Angle(g15,g14) = 1.5708
    c: Symmetric(g9,g12,g18)
    c: Coincident(g19,g9)
    c: Vertical(g19)
    c: Coincident(g19,g14)
    c: PointOnObject(g20,g19)
    c: Symmetric(g9,g11,g20)
    c: DistanceY(g13,g11) = 10
    c: DistanceX(g9,g11) = 4.5
    c: DistanceX(g18,g10) = 2
    c: Coincident(g21,g18)
    c: Coincident(g21,g10)
    c: Horizontal(g21)
FEATURE [PartDesign::Pocket] Pocket026  label="SpeakerMtHoles"
  BaseFeature = -> Pocket006
  Length = 5
  Length2 = 100
  Placement = pos=(0,0,0) rot=(1,0,0;1.5708rad)
  Profile = -> Sketch054
  Type = 1
FEATURE [PartDesign::Plane] DatumPlane009  label="Datum_TopOfFeet"
  AttachmentOffset = pos=(0,0,2) rot=(0,0,1;0rad)
  Length = 91.3862
  MapMode = 5
  Placement = pos=(0,0,2) rot=(0,0,1;0rad)
  ResizeMode = 0
  Support = -> [XY_Plane002]
  Width = 64.7862
  expr: .AttachmentOffset.Base.z = <<params>>.coverfront_foot_height
FEATURE [Sketcher::SketchObject] Sketch055  label="Sketch_CheckBoltHeadClear"
  FullyConstrained = true
  MapMode = 5
  Placement = pos=(0,0,2) rot=(0,0,1;0rad)
  Support = -> [DatumPlane009]
  expr: Constraints[8] = <<params>>.m2_head_clear_diam + 0.5mm
  expr: Constraints[4] = Spreadsheet.coverfront_outer_foot_width - 2 * Spreadsheet.coverfront_hole_offset_width
  expr: Constraints[3] = Spreadsheet.coverfront_leng - Spreadsheet.coverfront_hole_offset_leng
  sketch-geometry (4):
    g0: LineSegment StartX=-35.8 StartY=23 StartZ=0 EndX=35.8 EndY=23 EndZ=0
    g1: GeomPoint X=0 Y=23 Z=0
    g2: Circle CenterX=35.8 CenterY=23 CenterZ=0 NormalX=0 NormalY=0 NormalZ=1 AngleXU=0 Radius=2.35
    g3: Circle CenterX=-35.8 CenterY=23 CenterZ=0 NormalX=0 NormalY=0 NormalZ=1 AngleXU=0 Radius=2.35
  constraints (9):
    c: Horizontal(g0)
    c: PointOnObject(g1,g-2)
    c: Symmetric(g0,g0,g1)
    c: DistanceY(g-1,g1) = 23
    c: DistanceX(g0,g0) = 71.6
    c: Coincident(g2,g0)
    c: Coincident(g3,g0)
    c: Equal(g2,g3)
    c: Diameter(g2) = 4.7
FEATURE [PartDesign::Pocket] Pocket027  label="MtBoltHeadClear"
  BaseFeature = -> Pocket026
  Length = 5
  Length2 = 100
  Placement = pos=(0,0,0) rot=(1,0,0;1.5708rad)
  Profile = -> Sketch055
  Reversed = true
  Type = 1
FEATURE [PartDesign::Body] Body001  label="PB3D_TriPlate_Top_FrontCover"
  Group = -> [DatumPlane003,Sketch028,Sketch029,AdditiveLoft001,Sketch030,Pad001,Sketch031,Pocket005,Sketch032,Pocket006,DatumPlane008,Sketch054,Pocket026,DatumPlane009,Sketch055,Pocket027]
  Origin = -> Origin002
  Placement = pos=(0,-9,3) rot=(0,0,1;0rad)
  Tip = -> Pocket027
FEATURE [Sketcher::SketchObject] Sketch056  label="Sketch_EarMtHoles"
  FullyConstrained = true
  MapMode = 5
  Support = -> [XY_Plane001]
  expr: Constraints[9] = <<params>>.m2_hole_clear_diam
  expr: Constraints[5] = <<params>>.ear_mt_holes_loc
  expr: Constraints[4] = <<params>>.ear_mt_hole_spacing
  sketch-geometry (4):
    g0: LineSegment StartX=-41 StartY=-20 StartZ=0 EndX=41 EndY=-20 EndZ=0
    g1: LineSegment StartX=0 StartY=0 StartZ=0 EndX=0 EndY=-20 EndZ=0
    g2: Circle CenterX=-41 CenterY=-20 CenterZ=0 NormalX=0 NormalY=0 NormalZ=1 AngleXU=0 Radius=1.2
    g3: Circle CenterX=41 CenterY=-20 CenterZ=0 NormalX=0 NormalY=0 NormalZ=1 AngleXU=0 Radius=1.2
  constraints (10):
    c: Horizontal(g0)
    c: Coincident(g1,g-1)
    c: PointOnObject(g1,g-2)
    c: Symmetric(g0,g0,g1)
    c: DistanceX(g0,g0) = 82
    c: DistanceY(g1,g-1) = 20
    c: Coincident(g2,g0)
    c: Coincident(g3,g0)
    c: Equal(g3,g2)
    c: Diameter(g3) = 2.4
FEATURE [PartDesign::Pocket] Pocket028  label="Ear_HoleMt"
  BaseFeature = -> Pocket025
  Length = 5
  Length2 = 100
  Profile = -> Sketch056
  Reversed = true
  Type = 1
FEATURE [Sketcher::SketchObject] Sketch057  label="Sketch_FrontCoverMtHoles"
  FullyConstrained = true
  MapMode = 5
  Support = -> [XY_Plane001]
  expr: Constraints[4] = <<params>>.coverfront_leng - <<params>>.coverfront_hole_offset_leng - <<params>>.plate_to_frontcov_offset_y
  expr: Constraints[5] = <<params>>.coverfront_outer_foot_width - 2 * <<params>>.coverfront_hole_offset_width
  expr: Constraints[9] = <<params>>.m2_hole_clear_diam
  sketch-geometry (4):
    g0: LineSegment StartX=-35.8 StartY=14 StartZ=0 EndX=35.8 EndY=14 EndZ=0
    g1: LineSegment StartX=0 StartY=0 StartZ=0 EndX=0 EndY=14 EndZ=0
    g2: Circle CenterX=-35.8 CenterY=14 CenterZ=0 NormalX=0 NormalY=0 NormalZ=1 AngleXU=0 Radius=1.2
    g3: Circle CenterX=35.8 CenterY=14 CenterZ=0 NormalX=0 NormalY=0 NormalZ=1 AngleXU=0 Radius=1.2
  constraints (10):
    c: Horizontal(g0)
    c: Coincident(g1,g-1)
    c: PointOnObject(g1,g-2)
    c: Symmetric(g0,g0,g1)
    c: DistanceY(g-1,g1) = 14
    c: DistanceX(g0,g0) = 71.6
    c: Coincident(g2,g0)
    c: Coincident(g3,g0)
    c: Equal(g2,g3)
    c: Diameter(g3) = 2.4
FEATURE [PartDesign::Pocket] Pocket029  label="FrontCover_HoleMt"
  BaseFeature = -> Pocket028
  Length = 5
  Length2 = 100
  Profile = -> Sketch057
  Reversed = true
  Type = 1
FEATURE [Sketcher::SketchObject] Sketch058  label="Sketch_TouchSensMount001"
  FullyConstrained = true
  MapMode = 5
  Support = -> [XY_Plane001]
  expr: Constraints[64] = <<params>>.sens_touch_offset_leng
  expr: Constraints[56] = <<params>>.std_rad / 2
  expr: Constraints[21] = <<params>>.m2_hole_clear_diam
  expr: Constraints[144] = <<params>>.m2_nut_clear_flat
  sketch-geometry (56):
    g0: LineSegment StartX=-20 StartY=-15 StartZ=0 EndX=20 EndY=-15 EndZ=0
    g1: LineSegment StartX=20 StartY=-15 StartZ=0 EndX=20 EndY=-35 EndZ=0
    g2: LineSegment StartX=20 StartY=-35 StartZ=0 EndX=-20 EndY=-35 EndZ=0
    g3: LineSegment StartX=-20 StartY=-35 StartZ=0 EndX=-20 EndY=-15 EndZ=0
    g4: LineSegment StartX=0 StartY=0 StartZ=0 EndX=0 EndY=-15 EndZ=0
    g5: Circle CenterX=20 CenterY=-15 CenterZ=0 NormalX=0 NormalY=0 NormalZ=1 AngleXU=0 Radius=1.2
    g6: Circle CenterX=20 CenterY=-35 CenterZ=0 NormalX=0 NormalY=0 NormalZ=1 AngleXU=0 Radius=1.2
    g7: Circle CenterX=-20 CenterY=-35 CenterZ=0 NormalX=0 NormalY=0 NormalZ=1 AngleXU=0 Radius=1.2
    g8: Circle CenterX=-20 CenterY=-15 CenterZ=0 NormalX=0 NormalY=0 NormalZ=1 AngleXU=0 Radius=1.2
    g9: GeomPoint X=-3e-16 Y=-25 Z=0
    g10: LineSegment StartX=-31 StartY=-14.5 StartZ=0 EndX=31 EndY=-14.5 EndZ=0
    g11: LineSegment StartX=31 StartY=-14.5 StartZ=0 EndX=31 EndY=-35.5 EndZ=0
    g12: LineSegment StartX=31 StartY=-35.5 StartZ=0 EndX=-31 EndY=-35.5 EndZ=0
    g13: LineSegment StartX=-31 StartY=-35.5 StartZ=0 EndX=-31 EndY=-14.5 EndZ=0
    g14: Circle CenterX=-31 CenterY=-14.5 CenterZ=0 NormalX=0 NormalY=0 NormalZ=1 AngleXU=0 Radius=2.5
    g15: Circle CenterX=31 CenterY=-14.5 CenterZ=0 NormalX=0 NormalY=0 NormalZ=1 AngleXU=0 Radius=2.5
    g16: Circle CenterX=31 CenterY=-35.5 CenterZ=0 NormalX=0 NormalY=0 NormalZ=1 AngleXU=0 Radius=2.5
    g17: Circle CenterX=-31 CenterY=-35.5 CenterZ=0 NormalX=0 NormalY=0 NormalZ=1 AngleXU=0 Radius=2.5
    g18: LineSegment StartX=21 StartY=-18.5 StartZ=0 EndX=34 EndY=-18.5 EndZ=0
    g19: LineSegment StartX=35 StartY=-19.5 StartZ=0 EndX=35 EndY=-30.5 EndZ=0
    g20: LineSegment StartX=34 StartY=-31.5 StartZ=0 EndX=21 EndY=-31.5 EndZ=0
    g21: LineSegment StartX=20 StartY=-30.5 StartZ=0 EndX=20 EndY=-19.5 EndZ=0
    g22: ArcOfCircle CenterX=21 CenterY=-19.5 CenterZ=0 NormalX=0 NormalY=0 NormalZ=1 AngleXU=0 Radius=1 StartAngle=1.5708 EndAngle=3.14159
    g23: ArcOfCircle CenterX=34 CenterY=-19.5 CenterZ=0 NormalX=0 NormalY=0 NormalZ=1 AngleXU=0 Radius=1 StartAngle=0 EndAngle=1.5708
    g24: ArcOfCircle CenterX=34 CenterY=-30.5 CenterZ=0 NormalX=0 NormalY=0 NormalZ=1 AngleXU=0 Radius=1 StartAngle=4.71239 EndAngle=6.28319
    g25: ArcOfCircle CenterX=21 CenterY=-30.5 CenterZ=0 NormalX=0 NormalY=0 NormalZ=1 AngleXU=0 Radius=1 StartAngle=3.14159 EndAngle=4.71239
    g26: GeomPoint X=20 Y=-25 Z=0
    g27: LineSegment StartX=-3e-16 StartY=-25 StartZ=0 EndX=20 EndY=-25 EndZ=0
    g28: LineSegment StartX=-22.4826 StartY=-15 StartZ=0 EndX=-21.2413 EndY=-17.15 EndZ=0
    g29: LineSegment StartX=-21.2413 StartY=-17.15 StartZ=0 EndX=-18.7587 EndY=-17.15 EndZ=0
    g30: LineSegment StartX=-18.7587 StartY=-17.15 StartZ=0 EndX=-17.5174 EndY=-15 EndZ=0
    g31: LineSegment StartX=-17.5174 StartY=-15 StartZ=0 EndX=-18.7587 EndY=-12.85 EndZ=0
    g32: LineSegment StartX=-18.7587 StartY=-12.85 StartZ=0 EndX=-21.2413 EndY=-12.85 EndZ=0
    g33: LineSegment StartX=-21.2413 StartY=-12.85 StartZ=0 EndX=-22.4826 EndY=-15 EndZ=0
    g34: Circle CenterX=-20 CenterY=-15 CenterZ=0 NormalX=0 NormalY=0 NormalZ=1 AngleXU=0 Radius=2.48261
    g35: LineSegment StartX=-22.4826 StartY=-35 StartZ=0 EndX=-21.2413 EndY=-37.15 EndZ=0
    g36: LineSegment StartX=-21.2413 StartY=-37.15 StartZ=0 EndX=-18.7587 EndY=-37.15 EndZ=0
    g37: LineSegment StartX=-18.7587 StartY=-37.15 StartZ=0 EndX=-17.5174 EndY=-35 EndZ=0
    g38: LineSegment StartX=-17.5174 StartY=-35 StartZ=0 EndX=-18.7587 EndY=-32.85 EndZ=0
    g39: LineSegment StartX=-18.7587 StartY=-32.85 StartZ=0 EndX=-21.2413 EndY=-32.85 EndZ=0
    g40: LineSegment StartX=-21.2413 StartY=-32.85 StartZ=0 EndX=-22.4826 EndY=-35 EndZ=0
    g41: Circle CenterX=-20 CenterY=-35 CenterZ=0 NormalX=0 NormalY=0 NormalZ=1 AngleXU=0 Radius=2.48261
    g42: LineSegment StartX=22.4826 StartY=-35 StartZ=0 EndX=21.2413 EndY=-32.85 EndZ=0
    g43: LineSegment StartX=21.2413 StartY=-32.85 StartZ=0 EndX=18.7587 EndY=-32.85 EndZ=0
    g44: LineSegment StartX=18.7587 StartY=-32.85 StartZ=0 EndX=17.5174 EndY=-35 EndZ=0
    g45: LineSegment StartX=17.5174 StartY=-35 StartZ=0 EndX=18.7587 EndY=-37.15 EndZ=0
    g46: LineSegment StartX=18.7587 StartY=-37.15 StartZ=0 EndX=21.2413 EndY=-37.15 EndZ=0
    g47: LineSegment StartX=21.2413 StartY=-37.15 StartZ=0 EndX=22.4826 EndY=-35 EndZ=0
    g48: Circle CenterX=20 CenterY=-35 CenterZ=0 NormalX=0 NormalY=0 NormalZ=1 AngleXU=0 Radius=2.48261
    g49: LineSegment StartX=22.4826 StartY=-15 StartZ=0 EndX=21.2413 EndY=-12.85 EndZ=0
    g50: LineSegment StartX=21.2413 StartY=-12.85 StartZ=0 EndX=18.7587 EndY=-12.85 EndZ=0
    g51: LineSegment StartX=18.7587 StartY=-12.85 StartZ=0 EndX=17.5174 EndY=-15 EndZ=0
    g52: LineSegment StartX=17.5174 StartY=-15 StartZ=0 EndX=18.7587 EndY=-17.15 EndZ=0
    g53: LineSegment StartX=18.7587 StartY=-17.15 StartZ=0 EndX=21.2413 EndY=-17.15 EndZ=0
    g54: LineSegment StartX=21.2413 StartY=-17.15 StartZ=0 EndX=22.4826 EndY=-15 EndZ=0
    g55: Circle CenterX=20 CenterY=-15 CenterZ=0 NormalX=0 NormalY=0 NormalZ=1 AngleXU=0 Radius=2.48261
  constraints (129):
    c: Coincident(g0,g1)
    c: Coincident(g1,g2)
    c: Coincident(g2,g3)
    c: Coincident(g3,g0)
    c: Horizontal(g0)
    c: Horizontal(g2)
    c: Vertical(g1)
    c: Vertical(g3)
    c: Coincident(g4,g-1)
    c: PointOnObject(g4,g-2)
    c: Symmetric(g0,g0,g4)
    c: Distance(g1) = 20
    c: Distance(g0) = 40
    c: Coincident(g5,g0)
    c: Coincident(g6,g1)
    c: Coincident(g7,g2)
    c: Coincident(g8,g0)
    c: Symmetric(g5,g7,g9)
    c: Equal(g5,g8)
    c: Equal(g8,g7)
    c: Equal(g7,g6)
    c: Diameter(g5) = 2.4
    c: Coincident(g10,g11)
    c: Coincident(g11,g12)
    c: Coincident(g12,g13)
    c: Coincident(g13,g10)
    c: Horizontal(g10)
    c: Horizontal(g12)
    c: Vertical(g11)
    c: Vertical(g13)
    c: Symmetric(g12,g10,g9)
    c: Distance(g10) = 62
    c: Distance(g11) = 21
    c: Coincident(g14,g10)
    c: Coincident(g15,g10)
    c: Coincident(g16,g11)
    c: Coincident(g17,g12)
    c: Equal(g15,g16)
    c: Equal(g16,g17)
    c: Equal(g17,g14)
    c: Diameter(g15) = 5
    c: Horizontal(g18)
    c: Horizontal(g20)
    c: Vertical(g19)
    c: Vertical(g21)
    c: Tangent(g21,g22) = 1.5708
    c: Tangent(g18,g22) = 1.5708
    c: Tangent(g18,g23) = 1.5708
    c: Tangent(g19,g23) = 1.5708
    c: Tangent(g19,g24) = 1.5708
    c: Tangent(g20,g24) = 1.5708
    c: Tangent(g20,g25) = 1.5708
    c: Tangent(g21,g25) = 1.5708
    c: Equal(g24,g23)
    c: Equal(g24,g25)
    c: Equal(g25,g22)
    c: Radius(g23) = 1
    c: DistanceX(g21,g19) = 15
    c: DistanceY(g20,g18) = 13
    c: Symmetric(g21,g21,g26)
    c: Coincident(g27,g9)
    c: Coincident(g27,g26)
    c: Horizontal(g27)
    c: Distance(g27) = 20
    c: DistanceY(g9,g-1) = 25
    c: Coincident(g28,g29)
    c: Coincident(g29,g30)
    c: Coincident(g30,g31)
    c: Coincident(g31,g32)
    c: Coincident(g32,g33)
    c: Coincident(g33,g28)
    c: Equal(g28, g29-g33) x5
    c: PointOnObject(g28,g34)
    c: PointOnObject(g29,g34)
    c: PointOnObject(g30,g34)
    c: PointOnObject(g31,g34)
    c: PointOnObject(g32,g34)
    c: PointOnObject(g33,g34)
    c: Coincident(g34,g0)
    c: Coincident(g35,g36)
    c: Coincident(g36,g37)
    c: Coincident(g37,g38)
    c: Coincident(g38,g39)
    c: Coincident(g39,g40)
    c: Coincident(g40,g35)
    c: Equal(g35, g36-g40) x5
    c: PointOnObject(g35,g41)
    c: PointOnObject(g36,g41)
    c: PointOnObject(g37,g41)
    c: PointOnObject(g38,g41)
    c: PointOnObject(g39,g41)
    c: PointOnObject(g40,g41)
    c: Coincident(g41,g2)
    c: Coincident(g42,g43)
    c: Coincident(g43,g44)
    c: Coincident(g44,g45)
    c: Coincident(g45,g46)
    c: Coincident(g46,g47)
    c: Coincident(g47,g42)
    c: Equal(g42, g43-g47) x5
    c: PointOnObject(g42,g48)
    c: PointOnObject(g43,g48)
    c: PointOnObject(g44,g48)
    c: PointOnObject(g45,g48)
    c: PointOnObject(g46,g48)
    c: PointOnObject(g47,g48)
    c: Coincident(g48,g1)
    c: Coincident(g49,g50)
    c: Coincident(g50,g51)
    c: Coincident(g51,g52)
    c: Coincident(g52,g53)
    c: Coincident(g53,g54)
    c: Coincident(g54,g49)
    c: Equal(g49, g50-g54) x5
    c: PointOnObject(g49,g55)
    c: PointOnObject(g50,g55)
    c: PointOnObject(g51,g55)
    c: PointOnObject(g52,g55)
    c: PointOnObject(g53,g55)
    c: PointOnObject(g54,g55)
    c: Coincident(g55,g0)
    c: Horizontal(g32)
    c: Horizontal(g39)
    c: Horizontal(g43)
    c: Horizontal(g50)
    c: Equal(g34,g55)
    c: Equal(g55,g48)
    c: Equal(g48,g41)
    c: DistanceY(g29,g31) = 4.3
FEATURE [PartDesign::Pocket] Pocket030  label="TouchSens_HexMt"
  BaseFeature = -> Pocket029
  Length = 1.5
  Length2 = 100
  Profile = -> Sketch058
  Reversed = true
  Type = 0
  expr: Length = <<params>>.plate_thick / 2
FEATURE [Sketcher::SketchObject] Sketch059  label="Sketch_FrontCoverMtHoles001"
  FullyConstrained = true
  MapMode = 5
  Support = -> [XY_Plane001]
  expr: Constraints[9] = <<params>>.m2_hole_clear_diam
  expr: Constraints[5] = <<params>>.coverfront_outer_foot_width - 2 * <<params>>.coverfront_hole_offset_width
  expr: Constraints[4] = <<params>>.coverfront_leng - <<params>>.coverfront_hole_offset_leng - <<params>>.plate_to_frontcov_offset_y
  expr: Constraints[49] = <<params>>.m2_nut_clear_flat
  sketch-geometry (18):
    g0: LineSegment StartX=-35.8 StartY=14 StartZ=0 EndX=35.8 EndY=14 EndZ=0
    g1: LineSegment StartX=0 StartY=0 StartZ=0 EndX=0 EndY=14 EndZ=0
    g2: Circle CenterX=-35.8 CenterY=14 CenterZ=0 NormalX=0 NormalY=0 NormalZ=1 AngleXU=0 Radius=1.2
    g3: Circle CenterX=35.8 CenterY=14 CenterZ=0 NormalX=0 NormalY=0 NormalZ=1 AngleXU=0 Radius=1.2
    g4: LineSegment StartX=-38.2826 StartY=14 StartZ=0 EndX=-37.0413 EndY=11.85 EndZ=0
    g5: LineSegment StartX=-37.0413 StartY=11.85 StartZ=0 EndX=-34.5587 EndY=11.85 EndZ=0
    g6: LineSegment StartX=-34.5587 StartY=11.85 StartZ=0 EndX=-33.3174 EndY=14 EndZ=0
    g7: LineSegment StartX=-33.3174 StartY=14 StartZ=0 EndX=-34.5587 EndY=16.15 EndZ=0
    g8: LineSegment StartX=-34.5587 StartY=16.15 StartZ=0 EndX=-37.0413 EndY=16.15 EndZ=0
    g9: LineSegment StartX=-37.0413 StartY=16.15 StartZ=0 EndX=-38.2826 EndY=14 EndZ=0
    g10: Circle CenterX=-35.8 CenterY=14 CenterZ=0 NormalX=0 NormalY=0 NormalZ=1 AngleXU=0 Radius=2.48261
    g11: LineSegment StartX=38.2826 StartY=14 StartZ=0 EndX=37.0413 EndY=16.15 EndZ=0
    g12: LineSegment StartX=37.0413 StartY=16.15 StartZ=0 EndX=34.5587 EndY=16.15 EndZ=0
    g13: LineSegment StartX=34.5587 StartY=16.15 StartZ=0 EndX=33.3174 EndY=14 EndZ=0
    g14: LineSegment StartX=33.3174 StartY=14 StartZ=0 EndX=34.5587 EndY=11.85 EndZ=0
    g15: LineSegment StartX=34.5587 StartY=11.85 StartZ=0 EndX=37.0413 EndY=11.85 EndZ=0
    g16: LineSegment StartX=37.0413 StartY=11.85 StartZ=0 EndX=38.2826 EndY=14 EndZ=0
    g17: Circle CenterX=35.8 CenterY=14 CenterZ=0 NormalX=0 NormalY=0 NormalZ=1 AngleXU=0 Radius=2.48261
  constraints (42):
    c: Horizontal(g0)
    c: Coincident(g1,g-1)
    c: PointOnObject(g1,g-2)
    c: Symmetric(g0,g0,g1)
    c: DistanceY(g-1,g1) = 14
    c: DistanceX(g0,g0) = 71.6
    c: Coincident(g2,g0)
    c: Coincident(g3,g0)
    c: Equal(g2,g3)
    c: Diameter(g3) = 2.4
    c: Coincident(g4,g5)
    c: Coincident(g5,g6)
    c: Coincident(g6,g7)
    c: Coincident(g7,g8)
    c: Coincident(g8,g9)
    c: Coincident(g9,g4)
    c: Equal(g4, g5-g9) x5
    c: PointOnObject(g4,g10)
    c: PointOnObject(g5,g10)
    c: PointOnObject(g6,g10)
    c: PointOnObject(g7,g10)
    c: PointOnObject(g8,g10)
    c: PointOnObject(g9,g10)
    c: Coincident(g10,g0)
    c: Coincident(g11,g12)
    c: Coincident(g12,g13)
    c: Coincident(g13,g14)
    c: Coincident(g14,g15)
    c: Coincident(g15,g16)
    c: Coincident(g16,g11)
    c: Equal(g11, g12-g16) x5
    c: PointOnObject(g11,g17)
    c: PointOnObject(g12,g17)
    c: PointOnObject(g13,g17)
    c: PointOnObject(g14,g17)
    c: PointOnObject(g15,g17)
    c: PointOnObject(g16,g17)
    c: Coincident(g17,g0)
    c: Equal(g10,g17)
    c: Horizontal(g8)
    c: Horizontal(g12)
    c: DistanceY(g5,g7) = 4.3
FEATURE [PartDesign::Pocket] Pocket031  label="FrontCover_HexMt"
  BaseFeature = -> Pocket030
  Length = 1.5
  Length2 = 100
  Profile = -> Sketch059
  Reversed = true
  Type = 0
  expr: Length = <<params>>.plate_thick / 2
FEATURE [Sketcher::SketchObject] Sketch060  label="Sketch_EarMtHoles001"
  FullyConstrained = true
  MapMode = 5
  Support = -> [XY_Plane001]
  expr: Constraints[4] = <<params>>.ear_mt_hole_spacing
  expr: Constraints[5] = <<params>>.ear_mt_holes_loc
  expr: Constraints[9] = <<params>>.m2_hole_clear_diam
  expr: Constraints[49] = <<params>>.m2_nut_clear_flat
  sketch-geometry (19):
    g0: LineSegment StartX=-41 StartY=-20 StartZ=0 EndX=41 EndY=-20 EndZ=0
    g1: LineSegment StartX=0 StartY=0 StartZ=0 EndX=0 EndY=-20 EndZ=0
    g2: Circle CenterX=-41 CenterY=-20 CenterZ=0 NormalX=0 NormalY=0 NormalZ=1 AngleXU=0 Radius=1.2
    g3: Circle CenterX=41 CenterY=-20 CenterZ=0 NormalX=0 NormalY=0 NormalZ=1 AngleXU=0 Radius=1.2
    g4: LineSegment StartX=-43.4826 StartY=-20 StartZ=0 EndX=-42.2413 EndY=-22.15 EndZ=0
    g5: LineSegment StartX=-42.2413 StartY=-22.15 StartZ=0 EndX=-39.7587 EndY=-22.15 EndZ=0
    g6: LineSegment StartX=-39.7587 StartY=-22.15 StartZ=0 EndX=-38.5174 EndY=-20 EndZ=0
    g7: LineSegment StartX=-38.5174 StartY=-20 StartZ=0 EndX=-39.7587 EndY=-17.85 EndZ=0
    g8: LineSegment StartX=-39.7587 StartY=-17.85 StartZ=0 EndX=-42.2413 EndY=-17.85 EndZ=0
    g9: LineSegment StartX=-42.2413 StartY=-17.85 StartZ=0 EndX=-43.4826 EndY=-20 EndZ=0
    g10: Circle CenterX=-41 CenterY=-20 CenterZ=0 NormalX=0 NormalY=0 NormalZ=1 AngleXU=0 Radius=2.48261
    g11: LineSegment StartX=43.4826 StartY=-20 StartZ=0 EndX=42.2413 EndY=-17.85 EndZ=0
    g12: LineSegment StartX=42.2413 StartY=-17.85 StartZ=0 EndX=39.7587 EndY=-17.85 EndZ=0
    g13: LineSegment StartX=39.7587 StartY=-17.85 StartZ=0 EndX=38.5174 EndY=-20 EndZ=0
    g14: LineSegment StartX=38.5174 StartY=-20 StartZ=0 EndX=39.7587 EndY=-22.15 EndZ=0
    g15: LineSegment StartX=39.7587 StartY=-22.15 StartZ=0 EndX=42.2413 EndY=-22.15 EndZ=0
    g16: LineSegment StartX=42.2413 StartY=-22.15 StartZ=0 EndX=43.4826 EndY=-20 EndZ=0
    g17: Circle CenterX=41 CenterY=-20 CenterZ=0 NormalX=0 NormalY=0 NormalZ=1 AngleXU=0 Radius=2.48261
    g18: LineSegment StartX=42.2413 StartY=-17.85 StartZ=0 EndX=42.2413 EndY=-22.15 EndZ=0
  constraints (44):
    c: Horizontal(g0)
    c: Coincident(g1,g-1)
    c: PointOnObject(g1,g-2)
    c: Symmetric(g0,g0,g1)
    c: DistanceX(g0,g0) = 82
    c: DistanceY(g1,g-1) = 20
    c: Coincident(g2,g0)
    c: Coincident(g3,g0)
    c: Equal(g3,g2)
    c: Diameter(g3) = 2.4
    c: Coincident(g4,g5)
    c: Coincident(g5,g6)
    c: Coincident(g6,g7)
    c: Coincident(g7,g8)
    c: Coincident(g8,g9)
    c: Coincident(g9,g4)
    c: Equal(g4, g5-g9) x5
    c: PointOnObject(g4,g10)
    c: PointOnObject(g5,g10)
    c: PointOnObject(g6,g10)
    c: PointOnObject(g7,g10)
    c: PointOnObject(g8,g10)
    c: PointOnObject(g9,g10)
    c: Coincident(g10,g0)
    c: Coincident(g11,g12)
    c: Coincident(g12,g13)
    c: Coincident(g13,g14)
    c: Coincident(g14,g15)
    c: Coincident(g15,g16)
    c: Coincident(g16,g11)
    c: Equal(g11, g12-g16) x5
    c: PointOnObject(g11,g17)
    c: PointOnObject(g12,g17)
    c: PointOnObject(g13,g17)
    c: PointOnObject(g14,g17)
    c: PointOnObject(g15,g17)
    c: PointOnObject(g16,g17)
    c: Coincident(g17,g0)
    c: Equal(g17,g10)
    c: Coincident(g18,g11)
    c: Coincident(g18,g15)
    c: Distance(g18) = 4.3
    c: Horizontal(g12)
    c: Horizontal(g8)
FEATURE [PartDesign::Pocket] Pocket032  label="Ear_HexMt"
  BaseFeature = -> Pocket031
  Length = 1.5
  Length2 = 100
  Profile = -> Sketch060
  Reversed = true
  Type = 0
  expr: Length = <<params>>.plate_thick / 2
FEATURE [Sketcher::SketchObject] Sketch061  label="Sketch_EarMtHoles002"
  FullyConstrained = true
  MapMode = 5
  Support = -> [XY_Plane001]
  expr: Constraints[4] = <<params>>.ear_mt_hole_spacing
  expr: Constraints[5] = <<params>>.ear_mt_holes_loc
  expr: Constraints[9] = <<params>>.m2_hole_clear_diam
  expr: Constraints[55] = <<params>>.ear_cable_slot_offset_width
  expr: Constraints[46] = <<params>>.std_rad / 4
  expr: Constraints[53] = <<params>>.ear_cable_slot_offset
  sketch-geometry (24):
    g0: LineSegment StartX=-41 StartY=-20 StartZ=0 EndX=41 EndY=-20 EndZ=0
    g1: LineSegment StartX=0 StartY=0 StartZ=0 EndX=0 EndY=-20 EndZ=0
    g2: Circle CenterX=-41 CenterY=-20 CenterZ=0 NormalX=0 NormalY=0 NormalZ=1 AngleXU=0 Radius=1.2
    g3: Circle CenterX=41 CenterY=-20 CenterZ=0 NormalX=0 NormalY=0 NormalZ=1 AngleXU=0 Radius=1.2
    g4: LineSegment StartX=-53.5 StartY=-22.4 StartZ=0 EndX=-44.5 EndY=-22.4 EndZ=0
    g5: LineSegment StartX=-44 StartY=-22.9 StartZ=0 EndX=-44 EndY=-26.4 EndZ=0
    g6: LineSegment StartX=-44.5 StartY=-26.9 StartZ=0 EndX=-53.5 EndY=-26.9 EndZ=0
    g7: LineSegment StartX=-54 StartY=-26.4 StartZ=0 EndX=-54 EndY=-22.9 EndZ=0
    g8: LineSegment StartX=44.5 StartY=-22.4 StartZ=0 EndX=53.5 EndY=-22.4 EndZ=0
    g9: LineSegment StartX=54 StartY=-22.9 StartZ=0 EndX=54 EndY=-26.4 EndZ=0
    g10: LineSegment StartX=53.5 StartY=-26.9 StartZ=0 EndX=44.5 EndY=-26.9 EndZ=0
    g11: LineSegment StartX=44 StartY=-26.4 StartZ=0 EndX=44 EndY=-22.9 EndZ=0
    g12: ArcOfCircle CenterX=-44.5 CenterY=-22.9 CenterZ=0 NormalX=0 NormalY=0 NormalZ=1 AngleXU=0 Radius=0.5 StartAngle=3.1e-15 EndAngle=1.5708
    g13: ArcOfCircle CenterX=-44.5 CenterY=-26.4 CenterZ=0 NormalX=0 NormalY=0 NormalZ=1 AngleXU=0 Radius=0.5 StartAngle=4.71239 EndAngle=6.28319
    g14: ArcOfCircle CenterX=-53.5 CenterY=-26.4 CenterZ=0 NormalX=0 NormalY=0 NormalZ=1 AngleXU=0 Radius=0.5 StartAngle=3.14159 EndAngle=4.71239
    g15: ArcOfCircle CenterX=-53.5 CenterY=-22.9 CenterZ=0 NormalX=0 NormalY=0 NormalZ=1 AngleXU=0 Radius=0.5 StartAngle=1.5708 EndAngle=3.14159
    g16: ArcOfCircle CenterX=44.5 CenterY=-22.9 CenterZ=0 NormalX=0 NormalY=0 NormalZ=1 AngleXU=0 Radius=0.5 StartAngle=1.5708 EndAngle=3.14159
    g17: ArcOfCircle CenterX=44.5 CenterY=-26.4 CenterZ=0 NormalX=0 NormalY=0 NormalZ=1 AngleXU=0 Radius=0.5 StartAngle=3.14159 EndAngle=4.71239
    g18: ArcOfCircle CenterX=53.5 CenterY=-26.4 CenterZ=0 NormalX=0 NormalY=0 NormalZ=1 AngleXU=0 Radius=0.5 StartAngle=4.71239 EndAngle=6.28319
    g19: ArcOfCircle CenterX=53.5 CenterY=-22.9 CenterZ=0 NormalX=0 NormalY=0 NormalZ=1 AngleXU=0 Radius=0.5 StartAngle=4e-16 EndAngle=1.5708
    g20: LineSegment StartX=-44.5 StartY=-26.9 StartZ=0 EndX=44.5 EndY=-26.9 EndZ=0
    g21: GeomPoint X=0 Y=-26.9 Z=0
    g22: LineSegment StartX=-44 StartY=-22.9 StartZ=0 EndX=44 EndY=-22.9 EndZ=0
    g23: GeomPoint X=49 Y=-24.65 Z=0
  constraints (56):
    c: Horizontal(g0)
    c: Coincident(g1,g-1)
    c: PointOnObject(g1,g-2)
    c: Symmetric(g0,g0,g1)
    c: DistanceX(g0,g0) = 82
    c: DistanceY(g1,g-1) = 20
    c: Coincident(g2,g0)
    c: Coincident(g3,g0)
    c: Equal(g3,g2)
    c: Diameter(g3) = 2.4
    c: Horizontal(g4)
    c: Horizontal(g6)
    c: Vertical(g5)
    c: Vertical(g7)
    c: Horizontal(g8)
    c: Horizontal(g10)
    c: Vertical(g9)
    c: Vertical(g11)
    c: Tangent(g4,g12) = 1.5708
    c: Tangent(g5,g12) = 1.5708
    c: Tangent(g5,g13) = 1.5708
    c: Tangent(g6,g13) = 1.5708
    c: Tangent(g6,g14) = 1.5708
    c: Tangent(g7,g14) = 1.5708
    c: Tangent(g7,g15) = 1.5708
    c: Tangent(g4,g15) = 1.5708
    c: Tangent(g8,g16) = 1.5708
    c: Tangent(g11,g16) = 1.5708
    c: Tangent(g11,g17) = 1.5708
    c: Tangent(g10,g17) = 1.5708
    c: Tangent(g10,g18) = 1.5708
    c: Tangent(g9,g18) = 1.5708
    c: Tangent(g9,g19) = 1.5708
    c: Tangent(g8,g19) = 1.5708
    c: Equal(g12,g15)
    c: Equal(g13,g12)
    c: Equal(g13,g14)
    c: Equal(g12,g16)
    c: Equal(g16,g19)
    c: Equal(g19,g18)
    c: Equal(g18,g17)
    c: Coincident(g20,g6)
    c: Coincident(g20,g10)
    c: Horizontal(g20)
    c: PointOnObject(g21,g-2)
    c: Symmetric(g6,g10,g21)
    c: Radius(g19) = 0.5
    c: DistanceX(g11,g9) = 10
    c: DistanceY(g10,g8) = 4.5
    c: Coincident(g22,g5)
    c: Coincident(g22,g11)
    c: Horizontal(g22)
    c: Equal(g8,g4)
    c: DistanceY(g8,g3) = 2.4
    c: Symmetric(g19,g17,g23)
    c: DistanceX(g3,g23) = 8
FEATURE [PartDesign::Pocket] Pocket033  label="Ear_CableSlot"
  BaseFeature = -> Pocket032
  Length = 5
  Length2 = 100
  Profile = -> Sketch061
  Reversed = true
  Type = 1
FEATURE [Sketcher::SketchObject] Sketch062  label="Sketch_ShellTopHeadSunk"
  FullyConstrained = true
  MapMode = 5
  Placement = pos=(0,0,3) rot=(0,0,1;0rad)
  Support = -> [DatumPlane]
  expr: Constraints[145] = <<params>>.top_brack_front_leng - <<params>>.shell_topbrack_hole_offset
  expr: Constraints[133] = <<params>>.m2_head_clear_diam
  expr: Constraints[90] = <<params>>.shell_topbrack_hole_offset
  expr: Constraints[23] = <<params>>.std_rad
  expr: Constraints[61] = <<params>>.wheel_well_clearance
  expr: Constraints[30] = <<params>>.back_vert_edge
  expr: Constraints[31] = <<params>>.std_rad
  expr: Constraints[12] = <<params>>.plate_length
  expr: Constraints[29] = <<params>>.front_vert_edge
  expr: Constraints[32] = <<params>>.front_diameter
  expr: Constraints[85] = <<params>>.shell_topbrack_hole_offset + <<params>>.std_rad
  expr: Constraints[13] = <<params>>.tail_rad
  expr: Constraints[83] = <<params>>.shell_overhang_leng + <<params>>.shell_topbrack_width - <<params>>.shell_topbrack_hole_offset
  expr: Constraints[14] = <<params>>.tail_width
  expr: Constraints[41] = <<params>>.plate_width
  expr: Constraints[59] = <<params>>.std_rad
  expr: Constraints[82] = <<params>>.shell_overhang_leng + <<params>>.shell_topbrack_width - <<params>>.shell_topbrack_hole_offset
  expr: Constraints[84] = <<params>>.m2_hole_clear_diam
  expr: Constraints[86] = <<params>>.shell_topbrack_width * 2 - <<params>>.std_rad - <<params>>.shell_topbrack_hole_offset
  sketch-geometry (61):
    g0: ArcOfCircle CenterX=0 CenterY=52.6846 CenterZ=0 NormalX=0 NormalY=0 NormalZ=1 AngleXU=0 Radius=112.5 StartAngle=3.96017 EndAngle=5.4646
    g1: LineSegment StartX=-77.1162 StartY=42.1781 StartZ=0 EndX=-29.0404 EndY=108.13 EndZ=0
    g2: LineSegment StartX=-25 StartY=110.185 StartZ=0 EndX=25 EndY=110.185 EndZ=0
    g3: LineSegment StartX=29.0404 StartY=108.13 StartZ=0 EndX=77.1162 EndY=42.1781 EndZ=0
    g4: LineSegment StartX=0 StartY=0 StartZ=0 EndX=0 EndY=110.185 EndZ=0
    g5: ArcOfCircle CenterX=-25 CenterY=105.185 CenterZ=0 NormalX=0 NormalY=0 NormalZ=1 AngleXU=0 Radius=5 StartAngle=1.5708 EndAngle=2.5117
    g6: ArcOfCircle CenterX=25 CenterY=105.185 CenterZ=0 NormalX=0 NormalY=0 NormalZ=1 AngleXU=0 Radius=5 StartAngle=0.629894 EndAngle=1.5708
    g7: GeomPoint X=0 Y=-59.8154 Z=0
    g8: LineSegment StartX=77.5 StartY=26 StartZ=0 EndX=77.5 EndY=41 EndZ=0
    g9: LineSegment StartX=77.5 StartY=-26 StartZ=0 EndX=77.5 EndY=-28 EndZ=0
    g10: LineSegment StartX=-77.5 StartY=26 StartZ=0 EndX=-77.5 EndY=41 EndZ=0
    g11: ArcOfCircle CenterX=75.5 CenterY=-28 CenterZ=0 NormalX=0 NormalY=0 NormalZ=1 AngleXU=0 Radius=2 StartAngle=5.4646 EndAngle=6.28319
    g12: ArcOfCircle CenterX=-75.5 CenterY=-28 CenterZ=0 NormalX=0 NormalY=0 NormalZ=1 AngleXU=0 Radius=2 StartAngle=3.1416 EndAngle=3.96017
    g13: ArcOfCircle CenterX=75.5 CenterY=41 CenterZ=0 NormalX=0 NormalY=0 NormalZ=1 AngleXU=0 Radius=2 StartAngle=1e-16 EndAngle=0.629894
    g14: ArcOfCircle CenterX=-75.5 CenterY=41 CenterZ=0 NormalX=0 NormalY=0 NormalZ=1 AngleXU=0 Radius=2 StartAngle=2.5117 EndAngle=3.14159
    g15: GeomPoint X=77.5 Y=0 Z=0
    g16: GeomPoint X=-77.5 Y=0 Z=0
    g17: LineSegment StartX=-77.5 StartY=-28 StartZ=0 EndX=-77.5 EndY=-26 EndZ=0
    g18: LineSegment StartX=-77.5 StartY=26 StartZ=0 EndX=-77.5 EndY=24 EndZ=0
    g19: LineSegment StartX=-77.5 StartY=24 StartZ=0 EndX=-77.5 EndY=-24 EndZ=0
    g20: LineSegment StartX=-77.5 StartY=-26 StartZ=0 EndX=-77.5 EndY=-24 EndZ=0
    g21: LineSegment StartX=77.5 StartY=26 StartZ=0 EndX=77.5 EndY=24 EndZ=0
    g22: LineSegment StartX=77.5 StartY=24 StartZ=0 EndX=77.5 EndY=-24 EndZ=0
    g23: LineSegment StartX=77.5 StartY=-24 StartZ=0 EndX=77.5 EndY=-26 EndZ=0
    g24: Circle CenterX=16.5 CenterY=92.6846 CenterZ=0 NormalX=0 NormalY=0 NormalZ=1 AngleXU=0 Radius=1.2
    g25: Circle CenterX=60 CenterY=31.5 CenterZ=0 NormalX=0 NormalY=0 NormalZ=1 AngleXU=0 Radius=1.2
    g26: Circle CenterX=-60 CenterY=31.5 CenterZ=0 NormalX=0 NormalY=0 NormalZ=1 AngleXU=0 Radius=1.2
    g27: Circle CenterX=-60 CenterY=-21.5 CenterZ=0 NormalX=0 NormalY=0 NormalZ=1 AngleXU=0 Radius=1.2
    g28: Circle CenterX=60 CenterY=-21.5 CenterZ=0 NormalX=0 NormalY=0 NormalZ=1 AngleXU=0 Radius=1.2
    g29: LineSegment StartX=-60 StartY=-21.5 StartZ=0 EndX=60 EndY=-21.5 EndZ=0
    g30: LineSegment StartX=-60 StartY=31.5 StartZ=0 EndX=60 EndY=31.5 EndZ=0
    g31: LineSegment StartX=-16.5 StartY=92.6846 StartZ=0 EndX=16.5 EndY=92.6846 EndZ=0
    g32: GeomPoint X=0 Y=92.6846 Z=0
    g33: GeomPoint X=0 Y=31.5 Z=0
    g34: GeomPoint X=0 Y=-21.5 Z=0
    g35: LineSegment StartX=-60 StartY=31.5 StartZ=0 EndX=-60 EndY=-21.5 EndZ=0
    g36: Circle CenterX=3.5 CenterY=92.6846 CenterZ=0 NormalX=0 NormalY=0 NormalZ=1 AngleXU=0 Radius=1.2
    g37: ArcOfCircle CenterX=3.5 CenterY=92.6846 CenterZ=0 NormalX=0 NormalY=0 NormalZ=1 AngleXU=0 Radius=2.1 StartAngle=3.14159 EndAngle=6.28319
    g38: ArcOfCircle CenterX=3.5 CenterY=110.185 CenterZ=0 NormalX=0 NormalY=0 NormalZ=1 AngleXU=0 Radius=2.1 StartAngle=1.2e-15 EndAngle=3.14159
    g39: LineSegment StartX=5.6 StartY=92.6846 StartZ=0 EndX=5.6 EndY=110.185 EndZ=0
    g40: LineSegment StartX=1.4 StartY=92.6846 StartZ=0 EndX=1.4 EndY=110.185 EndZ=0
    g41: ArcOfCircle CenterX=16.5 CenterY=92.6846 CenterZ=0 NormalX=0 NormalY=0 NormalZ=1 AngleXU=0 Radius=2.1 StartAngle=3.14159 EndAngle=6.28319
    g42: ArcOfCircle CenterX=16.5 CenterY=110.185 CenterZ=0 NormalX=0 NormalY=0 NormalZ=1 AngleXU=0 Radius=2.1 StartAngle=1e-15 EndAngle=3.14159
    g43: LineSegment StartX=18.6 StartY=92.6846 StartZ=0 EndX=18.6 EndY=110.185 EndZ=0
    g44: LineSegment StartX=14.4 StartY=92.6846 StartZ=0 EndX=14.4 EndY=110.185 EndZ=0
    g45: ArcOfCircle CenterX=60 CenterY=-21.5 CenterZ=0 NormalX=0 NormalY=0 NormalZ=1 AngleXU=0 Radius=2.1 StartAngle=1.5708 EndAngle=4.71239
    g46: ArcOfCircle CenterX=77.5 CenterY=-21.5 CenterZ=0 NormalX=0 NormalY=0 NormalZ=1 AngleXU=0 Radius=2.1 StartAngle=4.71239 EndAngle=7.85398
    g47: LineSegment StartX=60 StartY=-23.6 StartZ=0 EndX=77.5 EndY=-23.6 EndZ=0
    g48: LineSegment StartX=60 StartY=-19.4 StartZ=0 EndX=77.5 EndY=-19.4 EndZ=0
    g49: ArcOfCircle CenterX=60 CenterY=31.5 CenterZ=0 NormalX=0 NormalY=0 NormalZ=1 AngleXU=0 Radius=2.1 StartAngle=1.5708 EndAngle=4.71239
    g50: ArcOfCircle CenterX=77.5 CenterY=31.5 CenterZ=0 NormalX=0 NormalY=0 NormalZ=1 AngleXU=0 Radius=2.1 StartAngle=4.71239 EndAngle=7.85398
    g51: LineSegment StartX=60 StartY=29.4 StartZ=0 EndX=77.5 EndY=29.4 EndZ=0
    g52: LineSegment StartX=60 StartY=33.6 StartZ=0 EndX=77.5 EndY=33.6 EndZ=0
    g53: ArcOfCircle CenterX=-60 CenterY=31.5 CenterZ=0 NormalX=0 NormalY=0 NormalZ=1 AngleXU=0 Radius=2.1 StartAngle=4.71239 EndAngle=7.85398
    g54: ArcOfCircle CenterX=-77.5 CenterY=31.5 CenterZ=0 NormalX=0 NormalY=0 NormalZ=1 AngleXU=0 Radius=2.1 StartAngle=1.5708 EndAngle=4.71239
    g55: LineSegment StartX=-60 StartY=33.6 StartZ=0 EndX=-77.5 EndY=33.6 EndZ=0
    g56: LineSegment StartX=-60 StartY=29.4 StartZ=0 EndX=-77.5 EndY=29.4 EndZ=0
    g57: ArcOfCircle CenterX=-60 CenterY=-21.5 CenterZ=0 NormalX=0 NormalY=0 NormalZ=1 AngleXU=0 Radius=2.1 StartAngle=4.71239 EndAngle=7.85398
    g58: ArcOfCircle CenterX=-77.5 CenterY=-21.5 CenterZ=0 NormalX=0 NormalY=0 NormalZ=1 AngleXU=0 Radius=2.1 StartAngle=1.5708 EndAngle=4.71239
    g59: LineSegment StartX=-60 StartY=-19.4 StartZ=0 EndX=-77.5 EndY=-19.4 EndZ=0
    g60: LineSegment StartX=-60 StartY=-23.6 StartZ=0 EndX=-77.5 EndY=-23.6 EndZ=0
  constraints (146):
    c: PointOnObject(g0,g-2)
    c: Horizontal(g2)
    c: Coincident(g4,g-1)
    c: PointOnObject(g4,g-2)
    c: Tangent(g1,g5) = 1.5708
    c: Tangent(g2,g5) = 1.5708
    c: Tangent(g2,g6) = 1.5708
    c: Tangent(g3,g6) = 1.5708
    c: Equal(g6,g5)
    c: Symmetric(g2,g2,g4)
    c: PointOnObject(g7,g-2)
    c: PointOnObject(g7,g0)
    c: DistanceY(g7,g2) = 170
    c: Radius(g6) = 5
    c: DistanceX(g2,g2) = 50
    c: Vertical(g8)
    c: Vertical(g9)
    c: Vertical(g10)
    c: Equal(g1,g3)
    c: Tangent(g0,g11) = -1.5708
    c: Tangent(g9,g11) = 1.5708
    c: Tangent(g0,g12) = -1.5708
    c: Equal(g11,g12)
    c: Radius(g11) = 2
    c: Tangent(g8,g13) = -1.5708
    c: Tangent(g3,g13) = 1.5708
    c: Tangent(g1,g14) = 1.5708
    c: Tangent(g10,g14) = 1.5708
    c: Equal(g13,g14)
    c: DistanceY(g9,g9) = 2
    c: DistanceY(g8,g8) = 15
    c: Radius(g13) = 2
    c: Diameter(g0) = 225
    c: PointOnObject(g15,g-1)
    c: PointOnObject(g16,g-1)
    c: Symmetric(g10,g17,g16)
    c: Symmetric(g8,g9,g15)
    c: Coincident(g17,g12)
    c: Vertical(g17)
    c: Equal(g10,g8)
    c: Equal(g9,g17)
    c: DistanceX(g12,g9) = 155
    c: Coincident(g18,g10)
    c: Vertical(g18)
    c: Coincident(g19,g18)
    c: Vertical(g19)
    c: Coincident(g20,g17)
    c: Vertical(g20)
    c: Equal(g20,g18)
    c: Coincident(g19,g20)
    c: Tangent(g12,g17)
    c: Coincident(g21,g8)
    c: Vertical(g21)
    c: Coincident(g22,g21)
    c: Vertical(g22)
    c: Coincident(g23,g22)
    c: Coincident(g23,g9)
    c: Equal(g23,g21)
    c: Vertical(g23)
    c: DistanceY(g21,g8) = 2
    c: Equal(g18,g21)
    c: DistanceY(g22,g21) = 48
    c: Coincident(g29,g27)
    c: Coincident(g29,g28)
    c: Horizontal(g29)
    c: Coincident(g30,g26)
    c: Coincident(g30,g25)
    c: Horizontal(g30)
    c: Equal(g27,g28)
    c: Equal(g28,g25)
    c: Equal(g25,g24)
    c: Equal(g25,g26)
    c: Coincident(g31,g24)
    c: Horizontal(g31)
    c: PointOnObject(g32,g4)
    c: PointOnObject(g33,g4)
    c: PointOnObject(g34,g-2)
    c: Symmetric(g26,g25,g33)
    c: Symmetric(g27,g28,g34)
    c: Coincident(g35,g26)
    c: Coincident(g35,g27)
    c: Vertical(g35)
    c: DistanceX(g25,g8) = 17.5
    c: DistanceY(g24,g2) = 17.5
    c: Diameter(g28) = 2.4
    c: DistanceY(g8,g25) = 5.5
    c: DistanceX(g24,g2) = 8.5
    c: Symmetric(g31,g24,g32)
    c: PointOnObject(g36,g31)
    c: Equal(g24,g36)
    c: DistanceX(g32,g36) = 3.5
    c: Tangent(g37,g40) = 1.5708
    c: Tangent(g37,g39) = -1.5708
    c: Tangent(g39,g38) = -1.5708
    c: Tangent(g40,g38) = 1.5708
    c: Vertical(g39)
    c: Equal(g37,g38)
    c: Coincident(g37,g36)
    c: Tangent(g41,g44) = 1.5708
    c: Tangent(g41,g43) = -1.5708
    c: Tangent(g43,g42) = -1.5708
    c: Tangent(g44,g42) = 1.5708
    c: Vertical(g43)
    c: Equal(g41,g42)
    c: Coincident(g41,g24)
    c: Tangent(g45,g48) = 1.5708
    c: Tangent(g45,g47) = -1.5708
    c: Tangent(g47,g46) = -1.5708
    c: Tangent(g48,g46) = 1.5708
    c: Horizontal(g47)
    c: Equal(g45,g46)
    c: Coincident(g45,g28)
    c: Tangent(g49,g52) = 1.5708
    c: Tangent(g49,g51) = -1.5708
    c: Tangent(g51,g50) = -1.5708
    c: Tangent(g52,g50) = 1.5708
    c: Horizontal(g51)
    c: Equal(g49,g50)
    c: Coincident(g49,g25)
    c: Tangent(g53,g56) = 1.5708
    c: Tangent(g53,g55) = -1.5708
    c: Tangent(g55,g54) = -1.5708
    c: Tangent(g56,g54) = 1.5708
    c: Horizontal(g55)
    c: Equal(g53,g54)
    c: Coincident(g53,g26)
    c: Tangent(g57,g60) = 1.5708
    c: Tangent(g57,g59) = -1.5708
    c: Tangent(g59,g58) = -1.5708
    c: Tangent(g60,g58) = 1.5708
    c: Horizontal(g59)
    c: Equal(g57,g58)
    c: Coincident(g57,g27)
    c: Diameter(g49) = 4.2
    c: Equal(g49,g45)
    c: Equal(g45,g57)
    c: Equal(g57,g53)
    c: Equal(g37,g53)
    c: Equal(g37,g41)
    c: PointOnObject(g38,g2)
    c: PointOnObject(g42,g2)
    c: PointOnObject(g50,g8)
    c: PointOnObject(g46,g22)
    c: PointOnObject(g58,g19)
    c: PointOnObject(g54,g10)
    c: DistanceY(g9,g45) = 6.5
FEATURE [PartDesign::Pocket] Pocket034  label="Pocket_HeadSunkSlot"
  BaseFeature = -> Pocket033
  Length = 1.5
  Length2 = 100
  Profile = -> Sketch062
  Type = 0
  expr: Length = <<params>>.plate_thick / 2
FEATURE [Sketcher::SketchObject] Sketch063  label="Sketch_GrMtHoles"
  FullyConstrained = true
  MapMode = 5
  Support = -> [XY_Plane001]
  expr: Constraints[60] = <<params>>.m2_hole_clear_diam
  expr: Constraints[53] = <<params>>.grmt1_w_offset
  expr: Constraints[52] = <<params>>.grmt1_l_offset
  expr: Constraints[51] = <<params>>.grmt2_l_offset
  expr: Constraints[50] = <<params>>.grmt2_w_offset
  sketch-geometry (28):
    g0: LineSegment StartX=32 StartY=51 StartZ=0 EndX=52 EndY=51 EndZ=0
    g1: LineSegment StartX=52 StartY=51 StartZ=0 EndX=52 EndY=31 EndZ=0
    g2: LineSegment StartX=52 StartY=31 StartZ=0 EndX=32 EndY=31 EndZ=0
    g3: LineSegment StartX=32 StartY=31 StartZ=0 EndX=32 EndY=51 EndZ=0
    g4: LineSegment StartX=41 StartY=28 StartZ=0 EndX=61 EndY=28 EndZ=0
    g5: LineSegment StartX=61 StartY=28 StartZ=0 EndX=61 EndY=8 EndZ=0
    g6: LineSegment StartX=61 StartY=8 StartZ=0 EndX=41 EndY=8 EndZ=0
    g7: LineSegment StartX=41 StartY=8 StartZ=0 EndX=41 EndY=28 EndZ=0
    g8: LineSegment StartX=-61 StartY=28 StartZ=0 EndX=-41 EndY=28 EndZ=0
    g9: LineSegment StartX=-41 StartY=28 StartZ=0 EndX=-41 EndY=8 EndZ=0
    g10: LineSegment StartX=-41 StartY=8 StartZ=0 EndX=-61 EndY=8 EndZ=0
    g11: LineSegment StartX=-61 StartY=8 StartZ=0 EndX=-61 EndY=28 EndZ=0
    g12: LineSegment StartX=-52 StartY=51 StartZ=0 EndX=-32 EndY=51 EndZ=0
    g13: LineSegment StartX=-32 StartY=51 StartZ=0 EndX=-32 EndY=31 EndZ=0
    g14: LineSegment StartX=-32 StartY=31 StartZ=0 EndX=-52 EndY=31 EndZ=0
    g15: LineSegment StartX=-52 StartY=31 StartZ=0 EndX=-52 EndY=51 EndZ=0
    g16: LineSegment StartX=-41 StartY=8 StartZ=0 EndX=41 EndY=8 EndZ=0
    g17: LineSegment StartX=-32 StartY=31 StartZ=0 EndX=32 EndY=31 EndZ=0
    g18: GeomPoint X=0 Y=31 Z=0
    g19: GeomPoint X=-2e-16 Y=8 Z=0
    g20: Circle CenterX=42 CenterY=51 CenterZ=0 NormalX=0 NormalY=0 NormalZ=1 AngleXU=0 Radius=1.2
    g21: Circle CenterX=42 CenterY=31 CenterZ=0 NormalX=0 NormalY=0 NormalZ=1 AngleXU=0 Radius=1.2
    g22: Circle CenterX=51 CenterY=28 CenterZ=0 NormalX=0 NormalY=0 NormalZ=1 AngleXU=0 Radius=1.2
    g23: Circle CenterX=51 CenterY=8 CenterZ=0 NormalX=0 NormalY=0 NormalZ=1 AngleXU=0 Radius=1.2
    g24: Circle CenterX=-42 CenterY=51 CenterZ=0 NormalX=0 NormalY=0 NormalZ=1 AngleXU=0 Radius=1.2
    g25: Circle CenterX=-51 CenterY=28 CenterZ=0 NormalX=0 NormalY=0 NormalZ=1 AngleXU=0 Radius=1.2
    g26: Circle CenterX=-51 CenterY=8 CenterZ=0 NormalX=0 NormalY=0 NormalZ=1 AngleXU=0 Radius=1.2
    g27: Circle CenterX=-42 CenterY=31 CenterZ=0 NormalX=0 NormalY=0 NormalZ=1 AngleXU=0 Radius=1.2
  constraints (70):
    c: Coincident(g0,g1)
    c: Coincident(g1,g2)
    c: Coincident(g2,g3)
    c: Coincident(g3,g0)
    c: Horizontal(g0)
    c: Horizontal(g2)
    c: Vertical(g1)
    c: Vertical(g3)
    c: Coincident(g4,g5)
    c: Coincident(g5,g6)
    c: Coincident(g6,g7)
    c: Coincident(g7,g4)
    c: Horizontal(g4)
    c: Horizontal(g6)
    c: Vertical(g5)
    c: Vertical(g7)
    c: Coincident(g8,g9)
    c: Coincident(g9,g10)
    c: Coincident(g10,g11)
    c: Coincident(g11,g8)
    c: Horizontal(g8)
    c: Horizontal(g10)
    c: Vertical(g9)
    c: Vertical(g11)
    c: Coincident(g12,g13)
    c: Coincident(g13,g14)
    c: Coincident(g14,g15)
    c: Coincident(g15,g12)
    c: Horizontal(g12)
    c: Horizontal(g14)
    c: Vertical(g13)
    c: Vertical(g15)
    c: Equal(g12,g15)
    c: Equal(g8,g11)
    c: Equal(g0,g1)
    c: Equal(g4,g5)
    c: Equal(g4,g1)
    c: Equal(g8,g12)
    c: Equal(g12,g0)
    c: Distance(g0) = 20
    c: Coincident(g16,g9)
    c: Coincident(g16,g6)
    c: Coincident(g17,g13)
    c: Coincident(g17,g2)
    c: Horizontal(g17)
    c: PointOnObject(g18,g-2)
    c: PointOnObject(g19,g-2)
    c: Horizontal(g16)
    c: Symmetric(g13,g2,g18)
    c: Symmetric(g9,g6,g19)
    c: DistanceX(g-1,g6) = 41
    c: DistanceY(g-1,g6) = 8
    c: DistanceY(g-1,g2) = 31
    c: DistanceX(g-1,g2) = 32
    c: Equal(g20,g21)
    c: Equal(g20,g22)
    c: Equal(g20,g23)
    c: Equal(g24,g27)
    c: Equal(g25,g26)
    c: Equal(g24,g20)
    c: Diameter(g20) = 2.4
    c: Equal(g25,g24)
    c: Symmetric(g0,g0,g20)
    c: Symmetric(g2,g1,g21)
    c: Symmetric(g4,g4,g22)
    c: Symmetric(g6,g5,g23)
    c: Symmetric(g12,g12,g24)
    c: Symmetric(g14,g13,g27)
    c: Symmetric(g8,g8,g25)
    c: Symmetric(g10,g9,g26)
FEATURE [PartDesign::Pocket] Pocket035  label="Pocket_GrMtHoles"
  BaseFeature = -> Pocket034
  Length = 5
  Length2 = 100
  Midplane = true
  Profile = -> Sketch063
  Type = 1
FEATURE [Sketcher::SketchObject] Sketch064  label="Sketch_GrMtHexSunk"
  FullyConstrained = true
  MapMode = 5
  Support = -> [XY_Plane001]
  expr: Constraints[229] = <<params>>.m2_nut_clear_flat
  expr: Constraints[50] = <<params>>.grmt2_w_offset
  expr: Constraints[51] = <<params>>.grmt2_l_offset
  expr: Constraints[52] = <<params>>.grmt1_l_offset
  expr: Constraints[53] = <<params>>.grmt1_w_offset
  expr: Constraints[60] = <<params>>.m2_hole_clear_diam
  sketch-geometry (84):
    g0: LineSegment StartX=32 StartY=51 StartZ=0 EndX=52 EndY=51 EndZ=0
    g1: LineSegment StartX=52 StartY=51 StartZ=0 EndX=52 EndY=31 EndZ=0
    g2: LineSegment StartX=52 StartY=31 StartZ=0 EndX=32 EndY=31 EndZ=0
    g3: LineSegment StartX=32 StartY=31 StartZ=0 EndX=32 EndY=51 EndZ=0
    g4: LineSegment StartX=41 StartY=28 StartZ=0 EndX=61 EndY=28 EndZ=0
    g5: LineSegment StartX=61 StartY=28 StartZ=0 EndX=61 EndY=8 EndZ=0
    g6: LineSegment StartX=61 StartY=8 StartZ=0 EndX=41 EndY=8 EndZ=0
    g7: LineSegment StartX=41 StartY=8 StartZ=0 EndX=41 EndY=28 EndZ=0
    g8: LineSegment StartX=-61 StartY=28 StartZ=0 EndX=-41 EndY=28 EndZ=0
    g9: LineSegment StartX=-41 StartY=28 StartZ=0 EndX=-41 EndY=8 EndZ=0
    g10: LineSegment StartX=-41 StartY=8 StartZ=0 EndX=-61 EndY=8 EndZ=0
    g11: LineSegment StartX=-61 StartY=8 StartZ=0 EndX=-61 EndY=28 EndZ=0
    g12: LineSegment StartX=-52 StartY=51 StartZ=0 EndX=-32 EndY=51 EndZ=0
    g13: LineSegment StartX=-32 StartY=51 StartZ=0 EndX=-32 EndY=31 EndZ=0
    g14: LineSegment StartX=-32 StartY=31 StartZ=0 EndX=-52 EndY=31 EndZ=0
    g15: LineSegment StartX=-52 StartY=31 StartZ=0 EndX=-52 EndY=51 EndZ=0
    g16: LineSegment StartX=-41 StartY=8 StartZ=0 EndX=41 EndY=8 EndZ=0
    g17: LineSegment StartX=-32 StartY=31 StartZ=0 EndX=32 EndY=31 EndZ=0
    g18: GeomPoint X=0 Y=31 Z=0
    g19: GeomPoint X=0 Y=8 Z=0
    g20: Circle CenterX=42 CenterY=51 CenterZ=0 NormalX=0 NormalY=0 NormalZ=1 AngleXU=0 Radius=1.2
    g21: Circle CenterX=42 CenterY=31 CenterZ=0 NormalX=0 NormalY=0 NormalZ=1 AngleXU=0 Radius=1.2
    g22: Circle CenterX=51 CenterY=28 CenterZ=0 NormalX=0 NormalY=0 NormalZ=1 AngleXU=0 Radius=1.2
    g23: Circle CenterX=51 CenterY=8 CenterZ=0 NormalX=0 NormalY=0 NormalZ=1 AngleXU=0 Radius=1.2
    g24: Circle CenterX=-42 CenterY=51 CenterZ=0 NormalX=0 NormalY=0 NormalZ=1 AngleXU=0 Radius=1.2
    g25: Circle CenterX=-51 CenterY=28 CenterZ=0 NormalX=0 NormalY=0 NormalZ=1 AngleXU=0 Radius=1.2
    g26: Circle CenterX=-51 CenterY=8 CenterZ=0 NormalX=0 NormalY=0 NormalZ=1 AngleXU=0 Radius=1.2
    g27: Circle CenterX=-42 CenterY=31 CenterZ=0 NormalX=0 NormalY=0 NormalZ=1 AngleXU=0 Radius=1.2
    g28: LineSegment StartX=44.4826 StartY=51 StartZ=0 EndX=43.2413 EndY=53.15 EndZ=0
    g29: LineSegment StartX=43.2413 StartY=53.15 StartZ=0 EndX=40.7587 EndY=53.15 EndZ=0
    g30: LineSegment StartX=40.7587 StartY=53.15 StartZ=0 EndX=39.5174 EndY=51 EndZ=0
    g31: LineSegment StartX=39.5174 StartY=51 StartZ=0 EndX=40.7587 EndY=48.85 EndZ=0
    g32: LineSegment StartX=40.7587 StartY=48.85 StartZ=0 EndX=43.2413 EndY=48.85 EndZ=0
    g33: LineSegment StartX=43.2413 StartY=48.85 StartZ=0 EndX=44.4826 EndY=51 EndZ=0
    g34: Circle CenterX=42 CenterY=51 CenterZ=0 NormalX=0 NormalY=0 NormalZ=1 AngleXU=0 Radius=2.48261
    g35: LineSegment StartX=44.4826 StartY=31 StartZ=0 EndX=43.2413 EndY=33.15 EndZ=0
    g36: LineSegment StartX=43.2413 StartY=33.15 StartZ=0 EndX=40.7587 EndY=33.15 EndZ=0
    g37: LineSegment StartX=40.7587 StartY=33.15 StartZ=0 EndX=39.5174 EndY=31 EndZ=0
    g38: LineSegment StartX=39.5174 StartY=31 StartZ=0 EndX=40.7587 EndY=28.85 EndZ=0
    g39: LineSegment StartX=40.7587 StartY=28.85 StartZ=0 EndX=43.2413 EndY=28.85 EndZ=0
    g40: LineSegment StartX=43.2413 StartY=28.85 StartZ=0 EndX=44.4826 EndY=31 EndZ=0
    g41: Circle CenterX=42 CenterY=31 CenterZ=0 NormalX=0 NormalY=0 NormalZ=1 AngleXU=0 Radius=2.48261
    g42: LineSegment StartX=53.4826 StartY=28 StartZ=0 EndX=52.2413 EndY=30.15 EndZ=0
    g43: LineSegment StartX=52.2413 StartY=30.15 StartZ=0 EndX=49.7587 EndY=30.15 EndZ=0
    g44: LineSegment StartX=49.7587 StartY=30.15 StartZ=0 EndX=48.5174 EndY=28 EndZ=0
    g45: LineSegment StartX=48.5174 StartY=28 StartZ=0 EndX=49.7587 EndY=25.85 EndZ=0
    g46: LineSegment StartX=49.7587 StartY=25.85 StartZ=0 EndX=52.2413 EndY=25.85 EndZ=0
    g47: LineSegment StartX=52.2413 StartY=25.85 StartZ=0 EndX=53.4826 EndY=28 EndZ=0
    g48: Circle CenterX=51 CenterY=28 CenterZ=0 NormalX=0 NormalY=0 NormalZ=1 AngleXU=0 Radius=2.48261
    g49: LineSegment StartX=53.4826 StartY=8 StartZ=0 EndX=52.2413 EndY=10.15 EndZ=0
    g50: LineSegment StartX=52.2413 StartY=10.15 StartZ=0 EndX=49.7587 EndY=10.15 EndZ=0
    g51: LineSegment StartX=49.7587 StartY=10.15 StartZ=0 EndX=48.5174 EndY=8 EndZ=0
    g52: LineSegment StartX=48.5174 StartY=8 StartZ=0 EndX=49.7587 EndY=5.85 EndZ=0
    g53: LineSegment StartX=49.7587 StartY=5.85 StartZ=0 EndX=52.2413 EndY=5.85 EndZ=0
    g54: LineSegment StartX=52.2413 StartY=5.85 StartZ=0 EndX=53.4826 EndY=8 EndZ=0
    g55: Circle CenterX=51 CenterY=8 CenterZ=0 NormalX=0 NormalY=0 NormalZ=1 AngleXU=0 Radius=2.48261
    g56: LineSegment StartX=-48.5174 StartY=8 StartZ=0 EndX=-49.7587 EndY=10.15 EndZ=0
    g57: LineSegment StartX=-49.7587 StartY=10.15 StartZ=0 EndX=-52.2413 EndY=10.15 EndZ=0
    g58: LineSegment StartX=-52.2413 StartY=10.15 StartZ=0 EndX=-53.4826 EndY=8 EndZ=0
    g59: LineSegment StartX=-53.4826 StartY=8 StartZ=0 EndX=-52.2413 EndY=5.85 EndZ=0
    g60: LineSegment StartX=-52.2413 StartY=5.85 StartZ=0 EndX=-49.7587 EndY=5.85 EndZ=0
    g61: LineSegment StartX=-49.7587 StartY=5.85 StartZ=0 EndX=-48.5174 EndY=8 EndZ=0
    g62: Circle CenterX=-51 CenterY=8 CenterZ=0 NormalX=0 NormalY=0 NormalZ=1 AngleXU=0 Radius=2.48261
    g63: LineSegment StartX=-48.5174 StartY=28 StartZ=0 EndX=-49.7587 EndY=30.15 EndZ=0
    g64: LineSegment StartX=-49.7587 StartY=30.15 StartZ=0 EndX=-52.2413 EndY=30.15 EndZ=0
    g65: LineSegment StartX=-52.2413 StartY=30.15 StartZ=0 EndX=-53.4826 EndY=28 EndZ=0
    g66: LineSegment StartX=-53.4826 StartY=28 StartZ=0 EndX=-52.2413 EndY=25.85 EndZ=0
    g67: LineSegment StartX=-52.2413 StartY=25.85 StartZ=0 EndX=-49.7587 EndY=25.85 EndZ=0
    g68: LineSegment StartX=-49.7587 StartY=25.85 StartZ=0 EndX=-48.5174 EndY=28 EndZ=0
    g69: Circle CenterX=-51 CenterY=28 CenterZ=0 NormalX=0 NormalY=0 NormalZ=1 AngleXU=0 Radius=2.48261
    g70: LineSegment StartX=-39.5174 StartY=31 StartZ=0 EndX=-40.7587 EndY=33.15 EndZ=0
    g71: LineSegment StartX=-40.7587 StartY=33.15 StartZ=0 EndX=-43.2413 EndY=33.15 EndZ=0
    g72: LineSegment StartX=-43.2413 StartY=33.15 StartZ=0 EndX=-44.4826 EndY=31 EndZ=0
    g73: LineSegment StartX=-44.4826 StartY=31 StartZ=0 EndX=-43.2413 EndY=28.85 EndZ=0
    g74: LineSegment StartX=-43.2413 StartY=28.85 StartZ=0 EndX=-40.7587 EndY=28.85 EndZ=0
    g75: LineSegment StartX=-40.7587 StartY=28.85 StartZ=0 EndX=-39.5174 EndY=31 EndZ=0
    g76: Circle CenterX=-42 CenterY=31 CenterZ=0 NormalX=0 NormalY=0 NormalZ=1 AngleXU=0 Radius=2.48261
    g77: LineSegment StartX=-39.5174 StartY=51 StartZ=0 EndX=-40.7587 EndY=53.15 EndZ=0
    g78: LineSegment StartX=-40.7587 StartY=53.15 StartZ=0 EndX=-43.2413 EndY=53.15 EndZ=0
    g79: LineSegment StartX=-43.2413 StartY=53.15 StartZ=0 EndX=-44.4826 EndY=51 EndZ=0
    g80: LineSegment StartX=-44.4826 StartY=51 StartZ=0 EndX=-43.2413 EndY=48.85 EndZ=0
    g81: LineSegment StartX=-43.2413 StartY=48.85 StartZ=0 EndX=-40.7587 EndY=48.85 EndZ=0
    g82: LineSegment StartX=-40.7587 StartY=48.85 StartZ=0 EndX=-39.5174 EndY=51 EndZ=0
    g83: Circle CenterX=-42 CenterY=51 CenterZ=0 NormalX=0 NormalY=0 NormalZ=1 AngleXU=0 Radius=2.48261
  constraints (198):
    c: Coincident(g0,g1)
    c: Coincident(g1,g2)
    c: Coincident(g2,g3)
    c: Coincident(g3,g0)
    c: Horizontal(g0)
    c: Horizontal(g2)
    c: Vertical(g1)
    c: Vertical(g3)
    c: Coincident(g4,g5)
    c: Coincident(g5,g6)
    c: Coincident(g6,g7)
    c: Coincident(g7,g4)
    c: Horizontal(g4)
    c: Horizontal(g6)
    c: Vertical(g5)
    c: Vertical(g7)
    c: Coincident(g8,g9)
    c: Coincident(g9,g10)
    c: Coincident(g10,g11)
    c: Coincident(g11,g8)
    c: Horizontal(g8)
    c: Horizontal(g10)
    c: Vertical(g9)
    c: Vertical(g11)
    c: Coincident(g12,g13)
    c: Coincident(g13,g14)
    c: Coincident(g14,g15)
    c: Coincident(g15,g12)
    c: Horizontal(g12)
    c: Horizontal(g14)
    c: Vertical(g13)
    c: Vertical(g15)
    c: Equal(g12,g15)
    c: Equal(g8,g11)
    c: Equal(g0,g1)
    c: Equal(g4,g5)
    c: Equal(g4,g1)
    c: Equal(g8,g12)
    c: Equal(g12,g0)
    c: Distance(g0) = 20
    c: Coincident(g16,g9)
    c: Coincident(g16,g6)
    c: Coincident(g17,g13)
    c: Coincident(g17,g2)
    c: Horizontal(g17)
    c: PointOnObject(g18,g-2)
    c: PointOnObject(g19,g-2)
    c: Horizontal(g16)
    c: Symmetric(g13,g2,g18)
    c: Symmetric(g9,g6,g19)
    c: DistanceX(g-1,g6) = 41
    c: DistanceY(g-1,g6) = 8
    c: DistanceY(g-1,g2) = 31
    c: DistanceX(g-1,g2) = 32
    c: Equal(g20,g21)
    c: Equal(g20,g22)
    c: Equal(g20,g23)
    c: Equal(g24,g27)
    c: Equal(g25,g26)
    c: Equal(g24,g20)
    c: Diameter(g20) = 2.4
    c: Equal(g25,g24)
    c: Symmetric(g0,g0,g20)
    c: Symmetric(g2,g1,g21)
    c: Symmetric(g4,g4,g22)
    c: Symmetric(g6,g5,g23)
    c: Symmetric(g12,g12,g24)
    c: Symmetric(g14,g13,g27)
    c: Symmetric(g8,g8,g25)
    c: Symmetric(g10,g9,g26)
    c: Coincident(g28,g29)
    c: Coincident(g29,g30)
    c: Coincident(g30,g31)
    c: Coincident(g31,g32)
    c: Coincident(g32,g33)
    c: Coincident(g33,g28)
    c: Equal(g28, g29-g33) x5
    c: PointOnObject(g28,g34)
    c: PointOnObject(g29,g34)
    c: PointOnObject(g30,g34)
    c: PointOnObject(g31,g34)
    c: PointOnObject(g32,g34)
    c: PointOnObject(g33,g34)
    c: Coincident(g34,g20)
    c: PointOnObject(g33,g0)
    c: Coincident(g35,g36)
    c: Coincident(g36,g37)
    c: Coincident(g37,g38)
    c: Coincident(g38,g39)
    c: Coincident(g39,g40)
    c: Coincident(g40,g35)
    c: Equal(g35, g36-g40) x5
    c: PointOnObject(g35,g41)
    c: PointOnObject(g36,g41)
    c: PointOnObject(g37,g41)
    c: PointOnObject(g38,g41)
    c: PointOnObject(g39,g41)
    c: PointOnObject(g40,g41)
    c: Coincident(g41,g21)
    c: PointOnObject(g40,g2)
    c: Coincident(g42,g43)
    c: Coincident(g43,g44)
    c: Coincident(g44,g45)
    c: Coincident(g45,g46)
    c: Coincident(g46,g47)
    c: Coincident(g47,g42)
    c: Equal(g42, g43-g47) x5
    c: PointOnObject(g42,g48)
    c: PointOnObject(g43,g48)
    c: PointOnObject(g44,g48)
    c: PointOnObject(g45,g48)
    c: PointOnObject(g46,g48)
    c: PointOnObject(g47,g48)
    c: Coincident(g48,g22)
    c: PointOnObject(g47,g4)
    c: Coincident(g49,g50)
    c: Coincident(g50,g51)
    c: Coincident(g51,g52)
    c: Coincident(g52,g53)
    c: Coincident(g53,g54)
    c: Coincident(g54,g49)
    c: Equal(g49, g50-g54) x5
    c: PointOnObject(g49,g55)
    c: PointOnObject(g50,g55)
    c: PointOnObject(g51,g55)
    c: PointOnObject(g52,g55)
    c: PointOnObject(g53,g55)
    c: PointOnObject(g54,g55)
    c: Coincident(g55,g23)
    c: PointOnObject(g54,g6)
    c: Coincident(g56,g57)
    c: Coincident(g57,g58)
    c: Coincident(g58,g59)
    c: Coincident(g59,g60)
    c: Coincident(g60,g61)
    c: Coincident(g61,g56)
    c: Equal(g56, g57-g61) x5
    c: PointOnObject(g56,g62)
    c: PointOnObject(g57,g62)
    c: PointOnObject(g58,g62)
    c: PointOnObject(g59,g62)
    c: PointOnObject(g60,g62)
    c: PointOnObject(g61,g62)
    c: Coincident(g62,g26)
    c: PointOnObject(g61,g10)
    c: Coincident(g63,g64)
    c: Coincident(g64,g65)
    c: Coincident(g65,g66)
    c: Coincident(g66,g67)
    c: Coincident(g67,g68)
    c: Coincident(g68,g63)
    c: Equal(g63, g64-g68) x5
    c: PointOnObject(g63,g69)
    c: PointOnObject(g64,g69)
    c: PointOnObject(g65,g69)
    c: PointOnObject(g66,g69)
    c: PointOnObject(g67,g69)
    c: PointOnObject(g68,g69)
    c: Coincident(g69,g25)
    c: PointOnObject(g68,g8)
    c: Coincident(g70,g71)
    c: Coincident(g71,g72)
    c: Coincident(g72,g73)
    c: Coincident(g73,g74)
    c: Coincident(g74,g75)
    c: Coincident(g75,g70)
    c: Equal(g70, g71-g75) x5
    c: PointOnObject(g70,g76)
    c: PointOnObject(g71,g76)
    c: PointOnObject(g72,g76)
    c: PointOnObject(g73,g76)
    c: PointOnObject(g74,g76)
    c: PointOnObject(g75,g76)
    c: Coincident(g76,g27)
    c: PointOnObject(g75,g14)
    c: Coincident(g77,g78)
    c: Coincident(g78,g79)
    c: Coincident(g79,g80)
    c: Coincident(g80,g81)
    c: Coincident(g81,g82)
    c: Coincident(g82,g77)
    c: Equal(g77, g78-g82) x5
    c: PointOnObject(g77,g83)
    c: PointOnObject(g78,g83)
    c: PointOnObject(g79,g83)
    c: PointOnObject(g80,g83)
    c: PointOnObject(g81,g83)
    c: PointOnObject(g82,g83)
    c: Coincident(g83,g24)
    c: PointOnObject(g82,g12)
    c: Equal(g83,g34)
    c: Equal(g41,g34)
    c: Equal(g48,g34)
    c: Equal(g55,g34)
    c: Equal(g83,g76)
    c: Equal(g83,g69)
    c: Equal(g62,g83)
    c: DistanceY(g31,g29) = 4.3
FEATURE [PartDesign::Pocket] Pocket036  label="Pocket_GrMtHexSunk"
  BaseFeature = -> Pocket035
  Length = 1.5
  Length2 = 100
  Profile = -> Sketch064
  Reversed = true
  Type = 0
  expr: Length = <<params>>.top_thickness / 2
FEATURE [Sketcher::SketchObject] Sketch065  label="Sketch_GrMtCableSlot"
  FullyConstrained = true
  MapMode = 5
  Support = -> [XY_Plane001]
  expr: Constraints[42] = <<params>>.grmt_cable_slot_l_offset
  expr: Constraints[36] = <<params>>.grmt_cable_slot_w_offset
  expr: Constraints[19] = 1
  sketch-geometry (18):
    g0: LineSegment StartX=34 StartY=29 StartZ=0 EndX=37 EndY=29 EndZ=0
    g1: LineSegment StartX=38 StartY=28 StartZ=0 EndX=38 EndY=20 EndZ=0
    g2: LineSegment StartX=37 StartY=19 StartZ=0 EndX=34 EndY=19 EndZ=0
    g3: LineSegment StartX=33 StartY=20 StartZ=0 EndX=33 EndY=28 EndZ=0
    g4: LineSegment StartX=-37 StartY=29 StartZ=0 EndX=-34 EndY=29 EndZ=0
    g5: LineSegment StartX=-33 StartY=28 StartZ=0 EndX=-33 EndY=20 EndZ=0
    g6: LineSegment StartX=-34 StartY=19 StartZ=0 EndX=-37 EndY=19 EndZ=0
    g7: LineSegment StartX=-38 StartY=20 StartZ=0 EndX=-38 EndY=28 EndZ=0
    g8: ArcOfCircle CenterX=-37 CenterY=28 CenterZ=0 NormalX=0 NormalY=0 NormalZ=1 AngleXU=0 Radius=1 StartAngle=1.5708 EndAngle=3.14159
    g9: ArcOfCircle CenterX=-34 CenterY=28 CenterZ=0 NormalX=0 NormalY=0 NormalZ=1 AngleXU=0 Radius=1 StartAngle=-3.6e-15 EndAngle=1.5708
    g10: ArcOfCircle CenterX=-34 CenterY=20 CenterZ=0 NormalX=0 NormalY=0 NormalZ=1 AngleXU=0 Radius=1 StartAngle=4.71239 EndAngle=6.28319
    g11: ArcOfCircle CenterX=-37 CenterY=20 CenterZ=0 NormalX=0 NormalY=0 NormalZ=1 AngleXU=0 Radius=1 StartAngle=3.14159 EndAngle=4.71239
    g12: ArcOfCircle CenterX=34 CenterY=28 CenterZ=0 NormalX=0 NormalY=0 NormalZ=1 AngleXU=0 Radius=1 StartAngle=1.5708 EndAngle=3.14159
    g13: ArcOfCircle CenterX=37 CenterY=28 CenterZ=0 NormalX=0 NormalY=0 NormalZ=1 AngleXU=0 Radius=1 StartAngle=-1.8e-15 EndAngle=1.5708
    g14: ArcOfCircle CenterX=34 CenterY=20 CenterZ=0 NormalX=0 NormalY=0 NormalZ=1 AngleXU=0 Radius=1 StartAngle=3.14159 EndAngle=4.71239
    g15: ArcOfCircle CenterX=37 CenterY=20 CenterZ=0 NormalX=0 NormalY=0 NormalZ=1 AngleXU=0 Radius=1 StartAngle=4.71239 EndAngle=6.28319
    g16: LineSegment StartX=-33 StartY=20 StartZ=0 EndX=33 EndY=20 EndZ=0
    g17: GeomPoint X=0 Y=20 Z=0
  constraints (43):
    c: Horizontal(g0)
    c: Horizontal(g2)
    c: Vertical(g1)
    c: Vertical(g3)
    c: Horizontal(g4)
    c: Horizontal(g6)
    c: Vertical(g5)
    c: Vertical(g7)
    c: Tangent(g7,g8) = 1.5708
    c: Tangent(g4,g8) = 1.5708
    c: Tangent(g4,g9) = 1.5708
    c: Tangent(g5,g9) = 1.5708
    c: Tangent(g5,g10) = 1.5708
    c: Tangent(g6,g10) = 1.5708
    c: Tangent(g6,g11) = 1.5708
    c: Tangent(g7,g11) = 1.5708
    c: Equal(g8,g9)
    c: Equal(g9,g10)
    c: Equal(g10,g11)
    c: Radius(g9) = 1
    c: DistanceX(g7,g5) = 5
    c: DistanceY(g6,g4) = 10
    c: Tangent(g3,g12) = 1.5708
    c: Tangent(g0,g12) = 1.5708
    c: Tangent(g0,g13) = 1.5708
    c: Tangent(g1,g13) = 1.5708
    c: Tangent(g3,g14) = 1.5708
    c: Tangent(g2,g14) = 1.5708
    c: Tangent(g1,g15) = 1.5708
    c: Tangent(g2,g15) = 1.5708
    c: Equal(g8,g12)
    c: Equal(g12,g13)
    c: Equal(g13,g14)
    c: Equal(g15,g14)
    c: Equal(g0,g4)
    c: Equal(g3,g5)
    c: DistanceX(g5,g-1) = 33
    c: Coincident(g16,g5)
    c: Coincident(g16,g3)
    c: Horizontal(g16)
    c: PointOnObject(g17,g-2)
    c: Symmetric(g5,g3,g17)
    c: DistanceY(g-1,g6) = 19
FEATURE [PartDesign::Pocket] Pocket037  label="Pocket_GrMtCableSlot"
  BaseFeature = -> Pocket036
  Length = 5
  Length2 = 100
  Profile = -> Sketch065
  Reversed = true
  Type = 1
FEATURE [PartDesign::Chamfer] Chamfer
  Angle = 45
  Base = -> Pocket037 [Edge304,Edge245,Edge351,Edge453,Edge386,Edge43,Edge16,Edge90,Edge66,Edge115]
  BaseFeature = -> Pocket037
  ChamferType = 0
  FlipDirection = false
  Size = 0.8
  Size2 = 1
  SupportTransform = false
FEATURE [PartDesign::Body] Body  label="PB3D_TriPlate_TopPlate"
  Group = -> [Sketch014,Sketch015,DatumPlane,Sketch016,AdditiveLoft,Sketch,Sketch021,Sketch022,Pad,Sketch023,DatumPlane001,Sketch024,SubtractiveLoft,Pocket,Pocket001,Sketch025,Pocket002,Sketch026,Pocket003,DatumPlane002,Sketch027,Pocket004,Sketch053,Pocket025,Sketch056,Pocket028,Sketch057,Pocket029,Sketch058,Pocket030,Sketch059,Pocket031,Sketch060,Pocket032,Sketch061,Pocket033,Sketch062,Pocket034,Sketch063,+6 more]
  Origin = -> Origin001
  Tip = -> Chamfer
FEATURE [App::Part] Part  label="PB3D_TriPlate_Top_Part"
  Group = -> [Body,Body001,Body002,Body005]
  Origin = -> Origin
FEATURE [Mesh::Feature] Mesh  label="PB3D_TriPlate_TopPlate (Meshed)"
